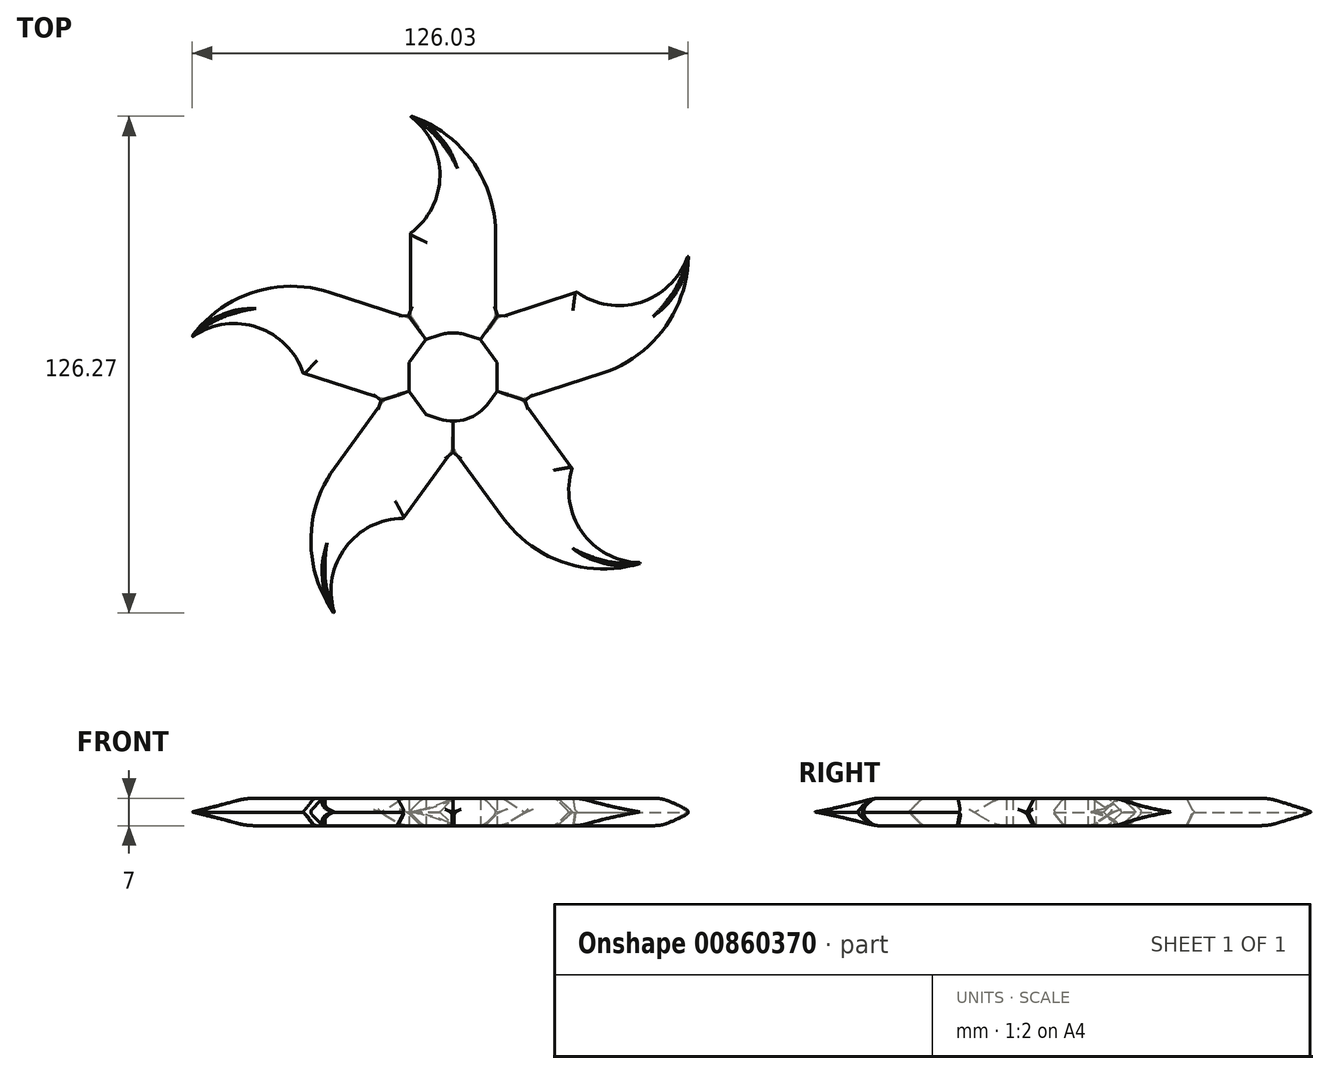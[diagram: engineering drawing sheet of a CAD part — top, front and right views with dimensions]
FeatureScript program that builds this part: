
annotation { "Feature Type Name" : "Feature", "Feature Type Description" : "" }
export const myFeature = defineFeature(function(context is Context, id is Id, definition is map)
    precondition{}
    {
        {
            var Q0;
            Q0=qCreatedBy(makeId("Top.planeOp"),FACE);
            var sketch = newSketch(context, id + "F0", { "sketchPlane" : qUnion([Q0])});
            skCircle(sketch, "E0", {"center": v(0, 0) * mm, "radius": 11.2 * mm});
            skLineSegment(sketch, "E1", {"start": v(-11.2, 36.37) * mm, "end": v(-11.2, 15.42) * mm});
            skLineSegment(sketch, "E2", {"start": v(11.2, 36.37) * mm, "end": v(11.2, 15.42) * mm});
            skLineSegment(sketch, "E3.1.0", {"start": v(-38.05, 0.59) * mm, "end": v(-18.12, -5.89) * mm});
            skLineSegment(sketch, "E3.2.0", {"start": v(-12.32, -36) * mm, "end": v(0, -19.05) * mm});
            skLineSegment(sketch, "E3.3.0", {"start": v(30.44, -22.84) * mm, "end": v(18.12, -5.89) * mm});
            skLineSegment(sketch, "E3.4.0", {"start": v(31.13, 21.9) * mm, "end": v(11.2, 15.42) * mm});
            skLineSegment(sketch, "E4.1.0", {"start": v(-31.13, 21.9) * mm, "end": v(-11.2, 15.42) * mm});
            skLineSegment(sketch, "E4.2.0", {"start": v(-30.44, -22.84) * mm, "end": v(-18.12, -5.89) * mm});
            skLineSegment(sketch, "E4.3.0", {"start": v(12.32, -36) * mm, "end": v(0, -19.05) * mm});
            skLineSegment(sketch, "E4.4.0", {"start": v(38.05, 0.59) * mm, "end": v(18.12, -5.89) * mm});
            skArc(sketch, "E5", {"start": v(11.2, 36.37) * mm, "mid": v(4.51, 55.95) * mm, "end": v(-12.75, 67.34) * mm});
            skArc(sketch, "E6", {"start": v(-11.2, 36.37) * mm, "mid": v(-3.43, 52.28) * mm, "end": v(-12.75, 67.34) * mm});
            skArc(sketch, "E7.1.0", {"start": v(-38.05, 0.59) * mm, "mid": v(-50.78, 12.9) * mm, "end": v(-67.98, 8.68) * mm});
            skArc(sketch, "E7.1.1", {"start": v(-31.13, 21.9) * mm, "mid": v(-51.81, 21.58) * mm, "end": v(-67.98, 8.68) * mm});
            skArc(sketch, "E7.2.0", {"start": v(-12.32, -36) * mm, "mid": v(-27.95, -44.32) * mm, "end": v(-29.26, -61.97) * mm});
            skArc(sketch, "E7.2.1", {"start": v(-30.44, -22.84) * mm, "mid": v(-36.53, -42.6) * mm, "end": v(-29.26, -61.97) * mm});
            skArc(sketch, "E7.3.0", {"start": v(30.44, -22.84) * mm, "mid": v(33.5, -40.28) * mm, "end": v(49.9, -46.98) * mm});
            skArc(sketch, "E7.3.1", {"start": v(12.32, -36) * mm, "mid": v(29.23, -47.91) * mm, "end": v(49.9, -46.98) * mm});
            skArc(sketch, "E7.4.0", {"start": v(31.13, 21.9) * mm, "mid": v(48.66, 19.42) * mm, "end": v(60.1, 32.94) * mm});
            skArc(sketch, "E7.4.1", {"start": v(38.05, 0.59) * mm, "mid": v(54.6, 13) * mm, "end": v(60.1, 32.94) * mm});
            skLineSegment(sketch, "E8.trimOffspring", {"start": v(11.2, 3.64) * mm, "end": v(11.2, -3.64) * mm});
            skLineSegment(sketch, "E9.trimOffspring", {"start": v(-6.92, -9.53) * mm, "end": v(-3.46, -10.65) * mm});
            skLineSegment(sketch, "E10.trimOffspring", {"start": v(0, 11.78) * mm, "end": v(-6.92, 9.53) * mm});
            skLineSegment(sketch, "E11.trimOffspring", {"start": v(3.46, 10.65) * mm, "end": v(6.92, 9.53) * mm});
            skLineSegment(sketch, "E12.trimOffspring", {"start": v(-11.2, 3.64) * mm, "end": v(-11.2, -3.64) * mm});
            skLineSegment(sketch, "E13.trimOffspring", {"start": v(-11.2, 3.64) * mm, "end": v(-6.92, 9.53) * mm});
            skLineSegment(sketch, "E14.trimOffspring", {"start": v(-6.92, -9.53) * mm, "end": v(-11.2, -3.64) * mm});
            skLineSegment(sketch, "E15.trimOffspring", {"start": v(11.2, 3.64) * mm, "end": v(6.92, 9.53) * mm});
            skLineSegment(sketch, "E16.trimOffspring", {"start": v(9.06, -6.58) * mm, "end": v(11.2, -3.64) * mm});
            skSolve(sketch);
        }
        {
            var Q0;
            Q0=makeQuery(id+"F0.imprint","IMPRINT",FACE,{"disambiguationData":[TD([[makeQuery(id+"F0.imprint","IMPRINT",EDGE,{"derivedFrom":sQuery(id+"F0.wireOp",EDGE,"E1")}),1.0]])]});
            extrude(context, id + "F1", {"entities" : qUnion([Q0]), "depth" : 7 * mm, "offsetDistance" : 25 * mm});
        }
        {
            var Q0;
            Q0=makeQuery(id+"F1.opExtrude","CAP_EDGE",EDGE,{"disambiguationData":[OSD([sQuery(id+"F0.wireOp",EDGE,"E5")])],"isStart":false});
            var Q1;
            Q1=makeQuery(id+"F1.opExtrude","CAP_EDGE",EDGE,{"disambiguationData":[OSD([sQuery(id+"F0.wireOp",EDGE,"E2")])],"isStart":false});
            var Q2;
            Q2=makeQuery(id+"F1.opExtrude","CAP_EDGE",EDGE,{"disambiguationData":[OSD([sQuery(id+"F0.wireOp",EDGE,"E6")])],"isStart":false});
            var Q3;
            Q3=makeQuery(id+"F1.opExtrude","CAP_EDGE",EDGE,{"disambiguationData":[OSD([sQuery(id+"F0.wireOp",EDGE,"E1")])],"isStart":false});
            var Q4;
            Q4=makeQuery(id+"F1.opExtrude","CAP_EDGE",EDGE,{"disambiguationData":[OSD([sQuery(id+"F0.wireOp",EDGE,"E3.4.0")])],"isStart":false});
            var Q5;
            Q5=makeQuery(id+"F1.opExtrude","CAP_EDGE",EDGE,{"disambiguationData":[OSD([sQuery(id+"F0.wireOp",EDGE,"E7.4.0")])],"isStart":false});
            var Q6;
            Q6=makeQuery(id+"F1.opExtrude","CAP_EDGE",EDGE,{"disambiguationData":[OSD([sQuery(id+"F0.wireOp",EDGE,"E7.4.1")])],"isStart":false});
            var Q7;
            Q7=makeQuery(id+"F1.opExtrude","CAP_EDGE",EDGE,{"disambiguationData":[OSD([sQuery(id+"F0.wireOp",EDGE,"E4.4.0")])],"isStart":false});
            var Q8;
            Q8=makeQuery(id+"F1.opExtrude","CAP_EDGE",EDGE,{"disambiguationData":[OSD([sQuery(id+"F0.wireOp",EDGE,"E3.3.0")])],"isStart":false});
            var Q9;
            Q9=makeQuery(id+"F1.opExtrude","CAP_EDGE",EDGE,{"disambiguationData":[OSD([sQuery(id+"F0.wireOp",EDGE,"E7.3.0")])],"isStart":false});
            var Q10;
            Q10=makeQuery(id+"F1.opExtrude","CAP_EDGE",EDGE,{"disambiguationData":[OSD([sQuery(id+"F0.wireOp",EDGE,"E7.3.1")])],"isStart":false});
            var Q11;
            Q11=makeQuery(id+"F1.opExtrude","CAP_EDGE",EDGE,{"disambiguationData":[OSD([sQuery(id+"F0.wireOp",EDGE,"E4.3.0")])],"isStart":false});
            var Q12;
            Q12=makeQuery(id+"F1.opExtrude","CAP_EDGE",EDGE,{"disambiguationData":[OSD([sQuery(id+"F0.wireOp",EDGE,"E4.1.0")])],"isStart":false});
            var Q13;
            Q13=makeQuery(id+"F1.opExtrude","CAP_EDGE",EDGE,{"disambiguationData":[OSD([sQuery(id+"F0.wireOp",EDGE,"E7.1.1")])],"isStart":false});
            var Q14;
            Q14=makeQuery(id+"F1.opExtrude","CAP_EDGE",EDGE,{"disambiguationData":[OSD([sQuery(id+"F0.wireOp",EDGE,"E7.1.0")])],"isStart":false});
            var Q15;
            Q15=makeQuery(id+"F1.opExtrude","CAP_EDGE",EDGE,{"disambiguationData":[OSD([sQuery(id+"F0.wireOp",EDGE,"E3.1.0")])],"isStart":false});
            var Q16;
            Q16=makeQuery(id+"F1.opExtrude","CAP_EDGE",EDGE,{"disambiguationData":[OSD([sQuery(id+"F0.wireOp",EDGE,"E4.2.0")])],"isStart":false});
            var Q17;
            Q17=makeQuery(id+"F1.opExtrude","CAP_EDGE",EDGE,{"disambiguationData":[OSD([sQuery(id+"F0.wireOp",EDGE,"E7.2.1")])],"isStart":false});
            var Q18;
            Q18=makeQuery(id+"F1.opExtrude","CAP_EDGE",EDGE,{"disambiguationData":[OSD([sQuery(id+"F0.wireOp",EDGE,"E3.2.0")])],"isStart":false});
            var Q19;
            Q19=makeQuery(id+"F1.opExtrude","CAP_EDGE",EDGE,{"disambiguationData":[OSD([sQuery(id+"F0.wireOp",EDGE,"E7.2.0")])],"isStart":false});
            chamfer(context, id + "F2", {"entities" : qUnion([Q0, Q1, Q2, Q3, Q4, Q5, Q6, Q7, Q8, Q9, Q10, Q11, Q12, Q13, Q14, Q15, Q16, Q17, Q18, Q19]), "width" : 3.5 * mm, "tangentPropagation" : true});
        }
        {
            var Q0;
            Q0=makeQuery(id+"F1.opExtrude","CAP_EDGE",EDGE,{"disambiguationData":[OSD([sQuery(id+"F0.wireOp",EDGE,"E7.2.0")])],"isStart":true});
            var Q1;
            Q1=makeQuery(id+"F1.opExtrude","CAP_EDGE",EDGE,{"disambiguationData":[OSD([sQuery(id+"F0.wireOp",EDGE,"E7.2.1")])],"isStart":true});
            var Q2;
            Q2=makeQuery(id+"F1.opExtrude","CAP_EDGE",EDGE,{"disambiguationData":[OSD([sQuery(id+"F0.wireOp",EDGE,"E4.2.0")])],"isStart":true});
            var Q3;
            Q3=makeQuery(id+"F1.opExtrude","CAP_EDGE",EDGE,{"disambiguationData":[OSD([sQuery(id+"F0.wireOp",EDGE,"E3.2.0")])],"isStart":true});
            var Q4;
            Q4=makeQuery(id+"F1.opExtrude","CAP_EDGE",EDGE,{"disambiguationData":[OSD([sQuery(id+"F0.wireOp",EDGE,"E7.3.1")])],"isStart":true});
            var Q5;
            Q5=makeQuery(id+"F1.opExtrude","CAP_EDGE",EDGE,{"disambiguationData":[OSD([sQuery(id+"F0.wireOp",EDGE,"E4.3.0")])],"isStart":true});
            var Q6;
            Q6=makeQuery(id+"F1.opExtrude","CAP_EDGE",EDGE,{"disambiguationData":[OSD([sQuery(id+"F0.wireOp",EDGE,"E7.3.0")])],"isStart":true});
            var Q7;
            Q7=makeQuery(id+"F1.opExtrude","CAP_EDGE",EDGE,{"disambiguationData":[OSD([sQuery(id+"F0.wireOp",EDGE,"E3.3.0")])],"isStart":true});
            var Q8;
            Q8=makeQuery(id+"F1.opExtrude","CAP_EDGE",EDGE,{"disambiguationData":[OSD([sQuery(id+"F0.wireOp",EDGE,"E3.1.0")])],"isStart":true});
            var Q9;
            Q9=makeQuery(id+"F1.opExtrude","CAP_EDGE",EDGE,{"disambiguationData":[OSD([sQuery(id+"F0.wireOp",EDGE,"E7.1.0")])],"isStart":true});
            var Q10;
            Q10=makeQuery(id+"F1.opExtrude","CAP_EDGE",EDGE,{"disambiguationData":[OSD([sQuery(id+"F0.wireOp",EDGE,"E7.1.1")])],"isStart":true});
            var Q11;
            Q11=makeQuery(id+"F1.opExtrude","CAP_EDGE",EDGE,{"disambiguationData":[OSD([sQuery(id+"F0.wireOp",EDGE,"E4.1.0")])],"isStart":true});
            var Q12;
            Q12=makeQuery(id+"F1.opExtrude","CAP_EDGE",EDGE,{"disambiguationData":[OSD([sQuery(id+"F0.wireOp",EDGE,"E1")])],"isStart":true});
            var Q13;
            Q13=makeQuery(id+"F1.opExtrude","CAP_EDGE",EDGE,{"disambiguationData":[OSD([sQuery(id+"F0.wireOp",EDGE,"E6")])],"isStart":true});
            var Q14;
            Q14=makeQuery(id+"F1.opExtrude","CAP_EDGE",EDGE,{"disambiguationData":[OSD([sQuery(id+"F0.wireOp",EDGE,"E5")])],"isStart":true});
            var Q15;
            Q15=makeQuery(id+"F1.opExtrude","CAP_EDGE",EDGE,{"disambiguationData":[OSD([sQuery(id+"F0.wireOp",EDGE,"E2")])],"isStart":true});
            var Q16;
            Q16=makeQuery(id+"F1.opExtrude","CAP_EDGE",EDGE,{"disambiguationData":[OSD([sQuery(id+"F0.wireOp",EDGE,"E3.4.0")])],"isStart":true});
            var Q17;
            Q17=makeQuery(id+"F1.opExtrude","CAP_EDGE",EDGE,{"disambiguationData":[OSD([sQuery(id+"F0.wireOp",EDGE,"E7.4.0")])],"isStart":true});
            var Q18;
            Q18=makeQuery(id+"F1.opExtrude","CAP_EDGE",EDGE,{"disambiguationData":[OSD([sQuery(id+"F0.wireOp",EDGE,"E7.4.1")])],"isStart":true});
            var Q19;
            Q19=makeQuery(id+"F1.opExtrude","CAP_EDGE",EDGE,{"disambiguationData":[OSD([sQuery(id+"F0.wireOp",EDGE,"E4.4.0")])],"isStart":true});
            chamfer(context, id + "F3", {"entities" : qUnion([Q0, Q1, Q2, Q3, Q4, Q5, Q6, Q7, Q8, Q9, Q10, Q11, Q12, Q13, Q14, Q15, Q16, Q17, Q18, Q19]), "width" : 3.5 * mm, "tangentPropagation" : true});
        }
        {
            var Q0;
            {var subQ0=sQuery(id+"F0.wireOp",EDGE,"E7.2.0");Q0=makeQuery(id+"F3.opChamfer","BLEND_EDGE",EDGE,{"blendedFrom":[makeQuery(id+"F1.opExtrude","CAP_EDGE",EDGE,{"disambiguationData":[OSD([subQ0])],"isStart":true}),makeQuery(id+"F1.opExtrude","CAP_FACE",FACE,{"disambiguationData":[OSD([sQuery(id+"F0.wireOp",EDGE,"E0"),sQuery(id+"F0.wireOp",EDGE,"E1"),sQuery(id+"F0.wireOp",EDGE,"E2"),sQuery(id+"F0.wireOp",EDGE,"E3.1.0"),sQuery(id+"F0.wireOp",EDGE,"E3.2.0"),sQuery(id+"F0.wireOp",EDGE,"E3.3.0"),sQuery(id+"F0.wireOp",EDGE,"E3.4.0"),sQuery(id+"F0.wireOp",EDGE,"E4.1.0"),sQuery(id+"F0.wireOp",EDGE,"E4.2.0"),sQuery(id+"F0.wireOp",EDGE,"E4.3.0"),sQuery(id+"F0.wireOp",EDGE,"E4.4.0"),sQuery(id+"F0.wireOp",EDGE,"E5"),sQuery(id+"F0.wireOp",EDGE,"E6"),sQuery(id+"F0.wireOp",EDGE,"E7.1.0"),sQuery(id+"F0.wireOp",EDGE,"E7.1.1"),subQ0,sQuery(id+"F0.wireOp",EDGE,"E7.2.1"),sQuery(id+"F0.wireOp",EDGE,"E7.3.0"),sQuery(id+"F0.wireOp",EDGE,"E7.3.1"),sQuery(id+"F0.wireOp",EDGE,"E7.4.0"),sQuery(id+"F0.wireOp",EDGE,"E7.4.1"),sQuery(id+"F0.wireOp",EDGE,"E8.trimOffspring"),sQuery(id+"F0.wireOp",EDGE,"E9.trimOffspring"),sQuery(id+"F0.wireOp",EDGE,"E10.trimOffspring"),sQuery(id+"F0.wireOp",EDGE,"E11.trimOffspring"),sQuery(id+"F0.wireOp",EDGE,"E12.trimOffspring"),sQuery(id+"F0.wireOp",EDGE,"E13.trimOffspring"),sQuery(id+"F0.wireOp",EDGE,"E14.trimOffspring"),sQuery(id+"F0.wireOp",EDGE,"E15.trimOffspring"),sQuery(id+"F0.wireOp",EDGE,"E16.trimOffspring")])],"isStart":true})],"blendedInto":[makeQuery(id+"F1.opExtrude","CAP_FACE",FACE,{"disambiguationData":[OSD([sQuery(id+"F0.wireOp",EDGE,"E0"),sQuery(id+"F0.wireOp",EDGE,"E1"),sQuery(id+"F0.wireOp",EDGE,"E2"),sQuery(id+"F0.wireOp",EDGE,"E3.1.0"),sQuery(id+"F0.wireOp",EDGE,"E3.2.0"),sQuery(id+"F0.wireOp",EDGE,"E3.3.0"),sQuery(id+"F0.wireOp",EDGE,"E3.4.0"),sQuery(id+"F0.wireOp",EDGE,"E4.1.0"),sQuery(id+"F0.wireOp",EDGE,"E4.2.0"),sQuery(id+"F0.wireOp",EDGE,"E4.3.0"),sQuery(id+"F0.wireOp",EDGE,"E4.4.0"),sQuery(id+"F0.wireOp",EDGE,"E5"),sQuery(id+"F0.wireOp",EDGE,"E6"),sQuery(id+"F0.wireOp",EDGE,"E7.1.0"),sQuery(id+"F0.wireOp",EDGE,"E7.1.1"),subQ0,sQuery(id+"F0.wireOp",EDGE,"E7.2.1"),sQuery(id+"F0.wireOp",EDGE,"E7.3.0"),sQuery(id+"F0.wireOp",EDGE,"E7.3.1"),sQuery(id+"F0.wireOp",EDGE,"E7.4.0"),sQuery(id+"F0.wireOp",EDGE,"E7.4.1"),sQuery(id+"F0.wireOp",EDGE,"E8.trimOffspring"),sQuery(id+"F0.wireOp",EDGE,"E9.trimOffspring"),sQuery(id+"F0.wireOp",EDGE,"E10.trimOffspring"),sQuery(id+"F0.wireOp",EDGE,"E11.trimOffspring"),sQuery(id+"F0.wireOp",EDGE,"E12.trimOffspring"),sQuery(id+"F0.wireOp",EDGE,"E13.trimOffspring"),sQuery(id+"F0.wireOp",EDGE,"E14.trimOffspring"),sQuery(id+"F0.wireOp",EDGE,"E15.trimOffspring"),sQuery(id+"F0.wireOp",EDGE,"E16.trimOffspring")])],"isStart":true})]});}
            var Q1;
            {var subQ0=sQuery(id+"F0.wireOp",EDGE,"E7.2.1");Q1=makeQuery(id+"F3.opChamfer","BLEND_EDGE",EDGE,{"blendedFrom":[makeQuery(id+"F1.opExtrude","CAP_EDGE",EDGE,{"disambiguationData":[OSD([subQ0])],"isStart":true}),makeQuery(id+"F1.opExtrude","CAP_FACE",FACE,{"disambiguationData":[OSD([sQuery(id+"F0.wireOp",EDGE,"E0"),sQuery(id+"F0.wireOp",EDGE,"E1"),sQuery(id+"F0.wireOp",EDGE,"E2"),sQuery(id+"F0.wireOp",EDGE,"E3.1.0"),sQuery(id+"F0.wireOp",EDGE,"E3.2.0"),sQuery(id+"F0.wireOp",EDGE,"E3.3.0"),sQuery(id+"F0.wireOp",EDGE,"E3.4.0"),sQuery(id+"F0.wireOp",EDGE,"E4.1.0"),sQuery(id+"F0.wireOp",EDGE,"E4.2.0"),sQuery(id+"F0.wireOp",EDGE,"E4.3.0"),sQuery(id+"F0.wireOp",EDGE,"E4.4.0"),sQuery(id+"F0.wireOp",EDGE,"E5"),sQuery(id+"F0.wireOp",EDGE,"E6"),sQuery(id+"F0.wireOp",EDGE,"E7.1.0"),sQuery(id+"F0.wireOp",EDGE,"E7.1.1"),sQuery(id+"F0.wireOp",EDGE,"E7.2.0"),subQ0,sQuery(id+"F0.wireOp",EDGE,"E7.3.0"),sQuery(id+"F0.wireOp",EDGE,"E7.3.1"),sQuery(id+"F0.wireOp",EDGE,"E7.4.0"),sQuery(id+"F0.wireOp",EDGE,"E7.4.1"),sQuery(id+"F0.wireOp",EDGE,"E8.trimOffspring"),sQuery(id+"F0.wireOp",EDGE,"E9.trimOffspring"),sQuery(id+"F0.wireOp",EDGE,"E10.trimOffspring"),sQuery(id+"F0.wireOp",EDGE,"E11.trimOffspring"),sQuery(id+"F0.wireOp",EDGE,"E12.trimOffspring"),sQuery(id+"F0.wireOp",EDGE,"E13.trimOffspring"),sQuery(id+"F0.wireOp",EDGE,"E14.trimOffspring"),sQuery(id+"F0.wireOp",EDGE,"E15.trimOffspring"),sQuery(id+"F0.wireOp",EDGE,"E16.trimOffspring")])],"isStart":true})],"blendedInto":[makeQuery(id+"F1.opExtrude","CAP_FACE",FACE,{"disambiguationData":[OSD([sQuery(id+"F0.wireOp",EDGE,"E0"),sQuery(id+"F0.wireOp",EDGE,"E1"),sQuery(id+"F0.wireOp",EDGE,"E2"),sQuery(id+"F0.wireOp",EDGE,"E3.1.0"),sQuery(id+"F0.wireOp",EDGE,"E3.2.0"),sQuery(id+"F0.wireOp",EDGE,"E3.3.0"),sQuery(id+"F0.wireOp",EDGE,"E3.4.0"),sQuery(id+"F0.wireOp",EDGE,"E4.1.0"),sQuery(id+"F0.wireOp",EDGE,"E4.2.0"),sQuery(id+"F0.wireOp",EDGE,"E4.3.0"),sQuery(id+"F0.wireOp",EDGE,"E4.4.0"),sQuery(id+"F0.wireOp",EDGE,"E5"),sQuery(id+"F0.wireOp",EDGE,"E6"),sQuery(id+"F0.wireOp",EDGE,"E7.1.0"),sQuery(id+"F0.wireOp",EDGE,"E7.1.1"),sQuery(id+"F0.wireOp",EDGE,"E7.2.0"),subQ0,sQuery(id+"F0.wireOp",EDGE,"E7.3.0"),sQuery(id+"F0.wireOp",EDGE,"E7.3.1"),sQuery(id+"F0.wireOp",EDGE,"E7.4.0"),sQuery(id+"F0.wireOp",EDGE,"E7.4.1"),sQuery(id+"F0.wireOp",EDGE,"E8.trimOffspring"),sQuery(id+"F0.wireOp",EDGE,"E9.trimOffspring"),sQuery(id+"F0.wireOp",EDGE,"E10.trimOffspring"),sQuery(id+"F0.wireOp",EDGE,"E11.trimOffspring"),sQuery(id+"F0.wireOp",EDGE,"E12.trimOffspring"),sQuery(id+"F0.wireOp",EDGE,"E13.trimOffspring"),sQuery(id+"F0.wireOp",EDGE,"E14.trimOffspring"),sQuery(id+"F0.wireOp",EDGE,"E15.trimOffspring"),sQuery(id+"F0.wireOp",EDGE,"E16.trimOffspring")])],"isStart":true})]});}
            var Q2;
            {var subQ0=sQuery(id+"F0.wireOp",EDGE,"E4.2.0");Q2=makeQuery(id+"F3.opChamfer","BLEND_EDGE",EDGE,{"blendedFrom":[makeQuery(id+"F1.opExtrude","CAP_EDGE",EDGE,{"disambiguationData":[OSD([subQ0])],"isStart":true}),makeQuery(id+"F1.opExtrude","CAP_FACE",FACE,{"disambiguationData":[OSD([sQuery(id+"F0.wireOp",EDGE,"E0"),sQuery(id+"F0.wireOp",EDGE,"E1"),sQuery(id+"F0.wireOp",EDGE,"E2"),sQuery(id+"F0.wireOp",EDGE,"E3.1.0"),sQuery(id+"F0.wireOp",EDGE,"E3.2.0"),sQuery(id+"F0.wireOp",EDGE,"E3.3.0"),sQuery(id+"F0.wireOp",EDGE,"E3.4.0"),sQuery(id+"F0.wireOp",EDGE,"E4.1.0"),subQ0,sQuery(id+"F0.wireOp",EDGE,"E4.3.0"),sQuery(id+"F0.wireOp",EDGE,"E4.4.0"),sQuery(id+"F0.wireOp",EDGE,"E5"),sQuery(id+"F0.wireOp",EDGE,"E6"),sQuery(id+"F0.wireOp",EDGE,"E7.1.0"),sQuery(id+"F0.wireOp",EDGE,"E7.1.1"),sQuery(id+"F0.wireOp",EDGE,"E7.2.0"),sQuery(id+"F0.wireOp",EDGE,"E7.2.1"),sQuery(id+"F0.wireOp",EDGE,"E7.3.0"),sQuery(id+"F0.wireOp",EDGE,"E7.3.1"),sQuery(id+"F0.wireOp",EDGE,"E7.4.0"),sQuery(id+"F0.wireOp",EDGE,"E7.4.1"),sQuery(id+"F0.wireOp",EDGE,"E8.trimOffspring"),sQuery(id+"F0.wireOp",EDGE,"E9.trimOffspring"),sQuery(id+"F0.wireOp",EDGE,"E10.trimOffspring"),sQuery(id+"F0.wireOp",EDGE,"E11.trimOffspring"),sQuery(id+"F0.wireOp",EDGE,"E12.trimOffspring"),sQuery(id+"F0.wireOp",EDGE,"E13.trimOffspring"),sQuery(id+"F0.wireOp",EDGE,"E14.trimOffspring"),sQuery(id+"F0.wireOp",EDGE,"E15.trimOffspring"),sQuery(id+"F0.wireOp",EDGE,"E16.trimOffspring")])],"isStart":true})],"blendedInto":[makeQuery(id+"F1.opExtrude","CAP_FACE",FACE,{"disambiguationData":[OSD([sQuery(id+"F0.wireOp",EDGE,"E0"),sQuery(id+"F0.wireOp",EDGE,"E1"),sQuery(id+"F0.wireOp",EDGE,"E2"),sQuery(id+"F0.wireOp",EDGE,"E3.1.0"),sQuery(id+"F0.wireOp",EDGE,"E3.2.0"),sQuery(id+"F0.wireOp",EDGE,"E3.3.0"),sQuery(id+"F0.wireOp",EDGE,"E3.4.0"),sQuery(id+"F0.wireOp",EDGE,"E4.1.0"),subQ0,sQuery(id+"F0.wireOp",EDGE,"E4.3.0"),sQuery(id+"F0.wireOp",EDGE,"E4.4.0"),sQuery(id+"F0.wireOp",EDGE,"E5"),sQuery(id+"F0.wireOp",EDGE,"E6"),sQuery(id+"F0.wireOp",EDGE,"E7.1.0"),sQuery(id+"F0.wireOp",EDGE,"E7.1.1"),sQuery(id+"F0.wireOp",EDGE,"E7.2.0"),sQuery(id+"F0.wireOp",EDGE,"E7.2.1"),sQuery(id+"F0.wireOp",EDGE,"E7.3.0"),sQuery(id+"F0.wireOp",EDGE,"E7.3.1"),sQuery(id+"F0.wireOp",EDGE,"E7.4.0"),sQuery(id+"F0.wireOp",EDGE,"E7.4.1"),sQuery(id+"F0.wireOp",EDGE,"E8.trimOffspring"),sQuery(id+"F0.wireOp",EDGE,"E9.trimOffspring"),sQuery(id+"F0.wireOp",EDGE,"E10.trimOffspring"),sQuery(id+"F0.wireOp",EDGE,"E11.trimOffspring"),sQuery(id+"F0.wireOp",EDGE,"E12.trimOffspring"),sQuery(id+"F0.wireOp",EDGE,"E13.trimOffspring"),sQuery(id+"F0.wireOp",EDGE,"E14.trimOffspring"),sQuery(id+"F0.wireOp",EDGE,"E15.trimOffspring"),sQuery(id+"F0.wireOp",EDGE,"E16.trimOffspring")])],"isStart":true})]});}
            var Q3;
            {var subQ0=sQuery(id+"F0.wireOp",EDGE,"E3.2.0");Q3=makeQuery(id+"F3.opChamfer","BLEND_EDGE",EDGE,{"blendedFrom":[makeQuery(id+"F1.opExtrude","CAP_EDGE",EDGE,{"disambiguationData":[OSD([subQ0])],"isStart":true}),makeQuery(id+"F1.opExtrude","CAP_FACE",FACE,{"disambiguationData":[OSD([sQuery(id+"F0.wireOp",EDGE,"E0"),sQuery(id+"F0.wireOp",EDGE,"E1"),sQuery(id+"F0.wireOp",EDGE,"E2"),sQuery(id+"F0.wireOp",EDGE,"E3.1.0"),subQ0,sQuery(id+"F0.wireOp",EDGE,"E3.3.0"),sQuery(id+"F0.wireOp",EDGE,"E3.4.0"),sQuery(id+"F0.wireOp",EDGE,"E4.1.0"),sQuery(id+"F0.wireOp",EDGE,"E4.2.0"),sQuery(id+"F0.wireOp",EDGE,"E4.3.0"),sQuery(id+"F0.wireOp",EDGE,"E4.4.0"),sQuery(id+"F0.wireOp",EDGE,"E5"),sQuery(id+"F0.wireOp",EDGE,"E6"),sQuery(id+"F0.wireOp",EDGE,"E7.1.0"),sQuery(id+"F0.wireOp",EDGE,"E7.1.1"),sQuery(id+"F0.wireOp",EDGE,"E7.2.0"),sQuery(id+"F0.wireOp",EDGE,"E7.2.1"),sQuery(id+"F0.wireOp",EDGE,"E7.3.0"),sQuery(id+"F0.wireOp",EDGE,"E7.3.1"),sQuery(id+"F0.wireOp",EDGE,"E7.4.0"),sQuery(id+"F0.wireOp",EDGE,"E7.4.1"),sQuery(id+"F0.wireOp",EDGE,"E8.trimOffspring"),sQuery(id+"F0.wireOp",EDGE,"E9.trimOffspring"),sQuery(id+"F0.wireOp",EDGE,"E10.trimOffspring"),sQuery(id+"F0.wireOp",EDGE,"E11.trimOffspring"),sQuery(id+"F0.wireOp",EDGE,"E12.trimOffspring"),sQuery(id+"F0.wireOp",EDGE,"E13.trimOffspring"),sQuery(id+"F0.wireOp",EDGE,"E14.trimOffspring"),sQuery(id+"F0.wireOp",EDGE,"E15.trimOffspring"),sQuery(id+"F0.wireOp",EDGE,"E16.trimOffspring")])],"isStart":true})],"blendedInto":[makeQuery(id+"F1.opExtrude","CAP_FACE",FACE,{"disambiguationData":[OSD([sQuery(id+"F0.wireOp",EDGE,"E0"),sQuery(id+"F0.wireOp",EDGE,"E1"),sQuery(id+"F0.wireOp",EDGE,"E2"),sQuery(id+"F0.wireOp",EDGE,"E3.1.0"),subQ0,sQuery(id+"F0.wireOp",EDGE,"E3.3.0"),sQuery(id+"F0.wireOp",EDGE,"E3.4.0"),sQuery(id+"F0.wireOp",EDGE,"E4.1.0"),sQuery(id+"F0.wireOp",EDGE,"E4.2.0"),sQuery(id+"F0.wireOp",EDGE,"E4.3.0"),sQuery(id+"F0.wireOp",EDGE,"E4.4.0"),sQuery(id+"F0.wireOp",EDGE,"E5"),sQuery(id+"F0.wireOp",EDGE,"E6"),sQuery(id+"F0.wireOp",EDGE,"E7.1.0"),sQuery(id+"F0.wireOp",EDGE,"E7.1.1"),sQuery(id+"F0.wireOp",EDGE,"E7.2.0"),sQuery(id+"F0.wireOp",EDGE,"E7.2.1"),sQuery(id+"F0.wireOp",EDGE,"E7.3.0"),sQuery(id+"F0.wireOp",EDGE,"E7.3.1"),sQuery(id+"F0.wireOp",EDGE,"E7.4.0"),sQuery(id+"F0.wireOp",EDGE,"E7.4.1"),sQuery(id+"F0.wireOp",EDGE,"E8.trimOffspring"),sQuery(id+"F0.wireOp",EDGE,"E9.trimOffspring"),sQuery(id+"F0.wireOp",EDGE,"E10.trimOffspring"),sQuery(id+"F0.wireOp",EDGE,"E11.trimOffspring"),sQuery(id+"F0.wireOp",EDGE,"E12.trimOffspring"),sQuery(id+"F0.wireOp",EDGE,"E13.trimOffspring"),sQuery(id+"F0.wireOp",EDGE,"E14.trimOffspring"),sQuery(id+"F0.wireOp",EDGE,"E15.trimOffspring"),sQuery(id+"F0.wireOp",EDGE,"E16.trimOffspring")])],"isStart":true})]});}
            var Q4;
            {var subQ0=sQuery(id+"F0.wireOp",EDGE,"E4.3.0");Q4=makeQuery(id+"F3.opChamfer","BLEND_EDGE",EDGE,{"blendedFrom":[makeQuery(id+"F1.opExtrude","CAP_EDGE",EDGE,{"disambiguationData":[OSD([subQ0])],"isStart":true}),makeQuery(id+"F1.opExtrude","CAP_FACE",FACE,{"disambiguationData":[OSD([sQuery(id+"F0.wireOp",EDGE,"E0"),sQuery(id+"F0.wireOp",EDGE,"E1"),sQuery(id+"F0.wireOp",EDGE,"E2"),sQuery(id+"F0.wireOp",EDGE,"E3.1.0"),sQuery(id+"F0.wireOp",EDGE,"E3.2.0"),sQuery(id+"F0.wireOp",EDGE,"E3.3.0"),sQuery(id+"F0.wireOp",EDGE,"E3.4.0"),sQuery(id+"F0.wireOp",EDGE,"E4.1.0"),sQuery(id+"F0.wireOp",EDGE,"E4.2.0"),subQ0,sQuery(id+"F0.wireOp",EDGE,"E4.4.0"),sQuery(id+"F0.wireOp",EDGE,"E5"),sQuery(id+"F0.wireOp",EDGE,"E6"),sQuery(id+"F0.wireOp",EDGE,"E7.1.0"),sQuery(id+"F0.wireOp",EDGE,"E7.1.1"),sQuery(id+"F0.wireOp",EDGE,"E7.2.0"),sQuery(id+"F0.wireOp",EDGE,"E7.2.1"),sQuery(id+"F0.wireOp",EDGE,"E7.3.0"),sQuery(id+"F0.wireOp",EDGE,"E7.3.1"),sQuery(id+"F0.wireOp",EDGE,"E7.4.0"),sQuery(id+"F0.wireOp",EDGE,"E7.4.1"),sQuery(id+"F0.wireOp",EDGE,"E8.trimOffspring"),sQuery(id+"F0.wireOp",EDGE,"E9.trimOffspring"),sQuery(id+"F0.wireOp",EDGE,"E10.trimOffspring"),sQuery(id+"F0.wireOp",EDGE,"E11.trimOffspring"),sQuery(id+"F0.wireOp",EDGE,"E12.trimOffspring"),sQuery(id+"F0.wireOp",EDGE,"E13.trimOffspring"),sQuery(id+"F0.wireOp",EDGE,"E14.trimOffspring"),sQuery(id+"F0.wireOp",EDGE,"E15.trimOffspring"),sQuery(id+"F0.wireOp",EDGE,"E16.trimOffspring")])],"isStart":true})],"blendedInto":[makeQuery(id+"F1.opExtrude","CAP_FACE",FACE,{"disambiguationData":[OSD([sQuery(id+"F0.wireOp",EDGE,"E0"),sQuery(id+"F0.wireOp",EDGE,"E1"),sQuery(id+"F0.wireOp",EDGE,"E2"),sQuery(id+"F0.wireOp",EDGE,"E3.1.0"),sQuery(id+"F0.wireOp",EDGE,"E3.2.0"),sQuery(id+"F0.wireOp",EDGE,"E3.3.0"),sQuery(id+"F0.wireOp",EDGE,"E3.4.0"),sQuery(id+"F0.wireOp",EDGE,"E4.1.0"),sQuery(id+"F0.wireOp",EDGE,"E4.2.0"),subQ0,sQuery(id+"F0.wireOp",EDGE,"E4.4.0"),sQuery(id+"F0.wireOp",EDGE,"E5"),sQuery(id+"F0.wireOp",EDGE,"E6"),sQuery(id+"F0.wireOp",EDGE,"E7.1.0"),sQuery(id+"F0.wireOp",EDGE,"E7.1.1"),sQuery(id+"F0.wireOp",EDGE,"E7.2.0"),sQuery(id+"F0.wireOp",EDGE,"E7.2.1"),sQuery(id+"F0.wireOp",EDGE,"E7.3.0"),sQuery(id+"F0.wireOp",EDGE,"E7.3.1"),sQuery(id+"F0.wireOp",EDGE,"E7.4.0"),sQuery(id+"F0.wireOp",EDGE,"E7.4.1"),sQuery(id+"F0.wireOp",EDGE,"E8.trimOffspring"),sQuery(id+"F0.wireOp",EDGE,"E9.trimOffspring"),sQuery(id+"F0.wireOp",EDGE,"E10.trimOffspring"),sQuery(id+"F0.wireOp",EDGE,"E11.trimOffspring"),sQuery(id+"F0.wireOp",EDGE,"E12.trimOffspring"),sQuery(id+"F0.wireOp",EDGE,"E13.trimOffspring"),sQuery(id+"F0.wireOp",EDGE,"E14.trimOffspring"),sQuery(id+"F0.wireOp",EDGE,"E15.trimOffspring"),sQuery(id+"F0.wireOp",EDGE,"E16.trimOffspring")])],"isStart":true})]});}
            var Q5;
            {var subQ0=sQuery(id+"F0.wireOp",EDGE,"E7.3.1");Q5=makeQuery(id+"F3.opChamfer","BLEND_EDGE",EDGE,{"blendedFrom":[makeQuery(id+"F1.opExtrude","CAP_EDGE",EDGE,{"disambiguationData":[OSD([subQ0])],"isStart":true}),makeQuery(id+"F1.opExtrude","CAP_FACE",FACE,{"disambiguationData":[OSD([sQuery(id+"F0.wireOp",EDGE,"E0"),sQuery(id+"F0.wireOp",EDGE,"E1"),sQuery(id+"F0.wireOp",EDGE,"E2"),sQuery(id+"F0.wireOp",EDGE,"E3.1.0"),sQuery(id+"F0.wireOp",EDGE,"E3.2.0"),sQuery(id+"F0.wireOp",EDGE,"E3.3.0"),sQuery(id+"F0.wireOp",EDGE,"E3.4.0"),sQuery(id+"F0.wireOp",EDGE,"E4.1.0"),sQuery(id+"F0.wireOp",EDGE,"E4.2.0"),sQuery(id+"F0.wireOp",EDGE,"E4.3.0"),sQuery(id+"F0.wireOp",EDGE,"E4.4.0"),sQuery(id+"F0.wireOp",EDGE,"E5"),sQuery(id+"F0.wireOp",EDGE,"E6"),sQuery(id+"F0.wireOp",EDGE,"E7.1.0"),sQuery(id+"F0.wireOp",EDGE,"E7.1.1"),sQuery(id+"F0.wireOp",EDGE,"E7.2.0"),sQuery(id+"F0.wireOp",EDGE,"E7.2.1"),sQuery(id+"F0.wireOp",EDGE,"E7.3.0"),subQ0,sQuery(id+"F0.wireOp",EDGE,"E7.4.0"),sQuery(id+"F0.wireOp",EDGE,"E7.4.1"),sQuery(id+"F0.wireOp",EDGE,"E8.trimOffspring"),sQuery(id+"F0.wireOp",EDGE,"E9.trimOffspring"),sQuery(id+"F0.wireOp",EDGE,"E10.trimOffspring"),sQuery(id+"F0.wireOp",EDGE,"E11.trimOffspring"),sQuery(id+"F0.wireOp",EDGE,"E12.trimOffspring"),sQuery(id+"F0.wireOp",EDGE,"E13.trimOffspring"),sQuery(id+"F0.wireOp",EDGE,"E14.trimOffspring"),sQuery(id+"F0.wireOp",EDGE,"E15.trimOffspring"),sQuery(id+"F0.wireOp",EDGE,"E16.trimOffspring")])],"isStart":true})],"blendedInto":[makeQuery(id+"F1.opExtrude","CAP_FACE",FACE,{"disambiguationData":[OSD([sQuery(id+"F0.wireOp",EDGE,"E0"),sQuery(id+"F0.wireOp",EDGE,"E1"),sQuery(id+"F0.wireOp",EDGE,"E2"),sQuery(id+"F0.wireOp",EDGE,"E3.1.0"),sQuery(id+"F0.wireOp",EDGE,"E3.2.0"),sQuery(id+"F0.wireOp",EDGE,"E3.3.0"),sQuery(id+"F0.wireOp",EDGE,"E3.4.0"),sQuery(id+"F0.wireOp",EDGE,"E4.1.0"),sQuery(id+"F0.wireOp",EDGE,"E4.2.0"),sQuery(id+"F0.wireOp",EDGE,"E4.3.0"),sQuery(id+"F0.wireOp",EDGE,"E4.4.0"),sQuery(id+"F0.wireOp",EDGE,"E5"),sQuery(id+"F0.wireOp",EDGE,"E6"),sQuery(id+"F0.wireOp",EDGE,"E7.1.0"),sQuery(id+"F0.wireOp",EDGE,"E7.1.1"),sQuery(id+"F0.wireOp",EDGE,"E7.2.0"),sQuery(id+"F0.wireOp",EDGE,"E7.2.1"),sQuery(id+"F0.wireOp",EDGE,"E7.3.0"),subQ0,sQuery(id+"F0.wireOp",EDGE,"E7.4.0"),sQuery(id+"F0.wireOp",EDGE,"E7.4.1"),sQuery(id+"F0.wireOp",EDGE,"E8.trimOffspring"),sQuery(id+"F0.wireOp",EDGE,"E9.trimOffspring"),sQuery(id+"F0.wireOp",EDGE,"E10.trimOffspring"),sQuery(id+"F0.wireOp",EDGE,"E11.trimOffspring"),sQuery(id+"F0.wireOp",EDGE,"E12.trimOffspring"),sQuery(id+"F0.wireOp",EDGE,"E13.trimOffspring"),sQuery(id+"F0.wireOp",EDGE,"E14.trimOffspring"),sQuery(id+"F0.wireOp",EDGE,"E15.trimOffspring"),sQuery(id+"F0.wireOp",EDGE,"E16.trimOffspring")])],"isStart":true})]});}
            var Q6;
            {var subQ0=sQuery(id+"F0.wireOp",EDGE,"E7.3.0");Q6=makeQuery(id+"F3.opChamfer","BLEND_EDGE",EDGE,{"blendedFrom":[makeQuery(id+"F1.opExtrude","CAP_EDGE",EDGE,{"disambiguationData":[OSD([subQ0])],"isStart":true}),makeQuery(id+"F1.opExtrude","CAP_FACE",FACE,{"disambiguationData":[OSD([sQuery(id+"F0.wireOp",EDGE,"E0"),sQuery(id+"F0.wireOp",EDGE,"E1"),sQuery(id+"F0.wireOp",EDGE,"E2"),sQuery(id+"F0.wireOp",EDGE,"E3.1.0"),sQuery(id+"F0.wireOp",EDGE,"E3.2.0"),sQuery(id+"F0.wireOp",EDGE,"E3.3.0"),sQuery(id+"F0.wireOp",EDGE,"E3.4.0"),sQuery(id+"F0.wireOp",EDGE,"E4.1.0"),sQuery(id+"F0.wireOp",EDGE,"E4.2.0"),sQuery(id+"F0.wireOp",EDGE,"E4.3.0"),sQuery(id+"F0.wireOp",EDGE,"E4.4.0"),sQuery(id+"F0.wireOp",EDGE,"E5"),sQuery(id+"F0.wireOp",EDGE,"E6"),sQuery(id+"F0.wireOp",EDGE,"E7.1.0"),sQuery(id+"F0.wireOp",EDGE,"E7.1.1"),sQuery(id+"F0.wireOp",EDGE,"E7.2.0"),sQuery(id+"F0.wireOp",EDGE,"E7.2.1"),subQ0,sQuery(id+"F0.wireOp",EDGE,"E7.3.1"),sQuery(id+"F0.wireOp",EDGE,"E7.4.0"),sQuery(id+"F0.wireOp",EDGE,"E7.4.1"),sQuery(id+"F0.wireOp",EDGE,"E8.trimOffspring"),sQuery(id+"F0.wireOp",EDGE,"E9.trimOffspring"),sQuery(id+"F0.wireOp",EDGE,"E10.trimOffspring"),sQuery(id+"F0.wireOp",EDGE,"E11.trimOffspring"),sQuery(id+"F0.wireOp",EDGE,"E12.trimOffspring"),sQuery(id+"F0.wireOp",EDGE,"E13.trimOffspring"),sQuery(id+"F0.wireOp",EDGE,"E14.trimOffspring"),sQuery(id+"F0.wireOp",EDGE,"E15.trimOffspring"),sQuery(id+"F0.wireOp",EDGE,"E16.trimOffspring")])],"isStart":true})],"blendedInto":[makeQuery(id+"F1.opExtrude","CAP_FACE",FACE,{"disambiguationData":[OSD([sQuery(id+"F0.wireOp",EDGE,"E0"),sQuery(id+"F0.wireOp",EDGE,"E1"),sQuery(id+"F0.wireOp",EDGE,"E2"),sQuery(id+"F0.wireOp",EDGE,"E3.1.0"),sQuery(id+"F0.wireOp",EDGE,"E3.2.0"),sQuery(id+"F0.wireOp",EDGE,"E3.3.0"),sQuery(id+"F0.wireOp",EDGE,"E3.4.0"),sQuery(id+"F0.wireOp",EDGE,"E4.1.0"),sQuery(id+"F0.wireOp",EDGE,"E4.2.0"),sQuery(id+"F0.wireOp",EDGE,"E4.3.0"),sQuery(id+"F0.wireOp",EDGE,"E4.4.0"),sQuery(id+"F0.wireOp",EDGE,"E5"),sQuery(id+"F0.wireOp",EDGE,"E6"),sQuery(id+"F0.wireOp",EDGE,"E7.1.0"),sQuery(id+"F0.wireOp",EDGE,"E7.1.1"),sQuery(id+"F0.wireOp",EDGE,"E7.2.0"),sQuery(id+"F0.wireOp",EDGE,"E7.2.1"),subQ0,sQuery(id+"F0.wireOp",EDGE,"E7.3.1"),sQuery(id+"F0.wireOp",EDGE,"E7.4.0"),sQuery(id+"F0.wireOp",EDGE,"E7.4.1"),sQuery(id+"F0.wireOp",EDGE,"E8.trimOffspring"),sQuery(id+"F0.wireOp",EDGE,"E9.trimOffspring"),sQuery(id+"F0.wireOp",EDGE,"E10.trimOffspring"),sQuery(id+"F0.wireOp",EDGE,"E11.trimOffspring"),sQuery(id+"F0.wireOp",EDGE,"E12.trimOffspring"),sQuery(id+"F0.wireOp",EDGE,"E13.trimOffspring"),sQuery(id+"F0.wireOp",EDGE,"E14.trimOffspring"),sQuery(id+"F0.wireOp",EDGE,"E15.trimOffspring"),sQuery(id+"F0.wireOp",EDGE,"E16.trimOffspring")])],"isStart":true})]});}
            var Q7;
            {var subQ0=sQuery(id+"F0.wireOp",EDGE,"E3.3.0");Q7=makeQuery(id+"F3.opChamfer","BLEND_EDGE",EDGE,{"blendedFrom":[makeQuery(id+"F1.opExtrude","CAP_EDGE",EDGE,{"disambiguationData":[OSD([subQ0])],"isStart":true}),makeQuery(id+"F1.opExtrude","CAP_FACE",FACE,{"disambiguationData":[OSD([sQuery(id+"F0.wireOp",EDGE,"E0"),sQuery(id+"F0.wireOp",EDGE,"E1"),sQuery(id+"F0.wireOp",EDGE,"E2"),sQuery(id+"F0.wireOp",EDGE,"E3.1.0"),sQuery(id+"F0.wireOp",EDGE,"E3.2.0"),subQ0,sQuery(id+"F0.wireOp",EDGE,"E3.4.0"),sQuery(id+"F0.wireOp",EDGE,"E4.1.0"),sQuery(id+"F0.wireOp",EDGE,"E4.2.0"),sQuery(id+"F0.wireOp",EDGE,"E4.3.0"),sQuery(id+"F0.wireOp",EDGE,"E4.4.0"),sQuery(id+"F0.wireOp",EDGE,"E5"),sQuery(id+"F0.wireOp",EDGE,"E6"),sQuery(id+"F0.wireOp",EDGE,"E7.1.0"),sQuery(id+"F0.wireOp",EDGE,"E7.1.1"),sQuery(id+"F0.wireOp",EDGE,"E7.2.0"),sQuery(id+"F0.wireOp",EDGE,"E7.2.1"),sQuery(id+"F0.wireOp",EDGE,"E7.3.0"),sQuery(id+"F0.wireOp",EDGE,"E7.3.1"),sQuery(id+"F0.wireOp",EDGE,"E7.4.0"),sQuery(id+"F0.wireOp",EDGE,"E7.4.1"),sQuery(id+"F0.wireOp",EDGE,"E8.trimOffspring"),sQuery(id+"F0.wireOp",EDGE,"E9.trimOffspring"),sQuery(id+"F0.wireOp",EDGE,"E10.trimOffspring"),sQuery(id+"F0.wireOp",EDGE,"E11.trimOffspring"),sQuery(id+"F0.wireOp",EDGE,"E12.trimOffspring"),sQuery(id+"F0.wireOp",EDGE,"E13.trimOffspring"),sQuery(id+"F0.wireOp",EDGE,"E14.trimOffspring"),sQuery(id+"F0.wireOp",EDGE,"E15.trimOffspring"),sQuery(id+"F0.wireOp",EDGE,"E16.trimOffspring")])],"isStart":true})],"blendedInto":[makeQuery(id+"F1.opExtrude","CAP_FACE",FACE,{"disambiguationData":[OSD([sQuery(id+"F0.wireOp",EDGE,"E0"),sQuery(id+"F0.wireOp",EDGE,"E1"),sQuery(id+"F0.wireOp",EDGE,"E2"),sQuery(id+"F0.wireOp",EDGE,"E3.1.0"),sQuery(id+"F0.wireOp",EDGE,"E3.2.0"),subQ0,sQuery(id+"F0.wireOp",EDGE,"E3.4.0"),sQuery(id+"F0.wireOp",EDGE,"E4.1.0"),sQuery(id+"F0.wireOp",EDGE,"E4.2.0"),sQuery(id+"F0.wireOp",EDGE,"E4.3.0"),sQuery(id+"F0.wireOp",EDGE,"E4.4.0"),sQuery(id+"F0.wireOp",EDGE,"E5"),sQuery(id+"F0.wireOp",EDGE,"E6"),sQuery(id+"F0.wireOp",EDGE,"E7.1.0"),sQuery(id+"F0.wireOp",EDGE,"E7.1.1"),sQuery(id+"F0.wireOp",EDGE,"E7.2.0"),sQuery(id+"F0.wireOp",EDGE,"E7.2.1"),sQuery(id+"F0.wireOp",EDGE,"E7.3.0"),sQuery(id+"F0.wireOp",EDGE,"E7.3.1"),sQuery(id+"F0.wireOp",EDGE,"E7.4.0"),sQuery(id+"F0.wireOp",EDGE,"E7.4.1"),sQuery(id+"F0.wireOp",EDGE,"E8.trimOffspring"),sQuery(id+"F0.wireOp",EDGE,"E9.trimOffspring"),sQuery(id+"F0.wireOp",EDGE,"E10.trimOffspring"),sQuery(id+"F0.wireOp",EDGE,"E11.trimOffspring"),sQuery(id+"F0.wireOp",EDGE,"E12.trimOffspring"),sQuery(id+"F0.wireOp",EDGE,"E13.trimOffspring"),sQuery(id+"F0.wireOp",EDGE,"E14.trimOffspring"),sQuery(id+"F0.wireOp",EDGE,"E15.trimOffspring"),sQuery(id+"F0.wireOp",EDGE,"E16.trimOffspring")])],"isStart":true})]});}
            var Q8;
            {var subQ0=sQuery(id+"F0.wireOp",EDGE,"E4.4.0");Q8=makeQuery(id+"F3.opChamfer","BLEND_EDGE",EDGE,{"blendedFrom":[makeQuery(id+"F1.opExtrude","CAP_EDGE",EDGE,{"disambiguationData":[OSD([subQ0])],"isStart":true}),makeQuery(id+"F1.opExtrude","CAP_FACE",FACE,{"disambiguationData":[OSD([sQuery(id+"F0.wireOp",EDGE,"E0"),sQuery(id+"F0.wireOp",EDGE,"E1"),sQuery(id+"F0.wireOp",EDGE,"E2"),sQuery(id+"F0.wireOp",EDGE,"E3.1.0"),sQuery(id+"F0.wireOp",EDGE,"E3.2.0"),sQuery(id+"F0.wireOp",EDGE,"E3.3.0"),sQuery(id+"F0.wireOp",EDGE,"E3.4.0"),sQuery(id+"F0.wireOp",EDGE,"E4.1.0"),sQuery(id+"F0.wireOp",EDGE,"E4.2.0"),sQuery(id+"F0.wireOp",EDGE,"E4.3.0"),subQ0,sQuery(id+"F0.wireOp",EDGE,"E5"),sQuery(id+"F0.wireOp",EDGE,"E6"),sQuery(id+"F0.wireOp",EDGE,"E7.1.0"),sQuery(id+"F0.wireOp",EDGE,"E7.1.1"),sQuery(id+"F0.wireOp",EDGE,"E7.2.0"),sQuery(id+"F0.wireOp",EDGE,"E7.2.1"),sQuery(id+"F0.wireOp",EDGE,"E7.3.0"),sQuery(id+"F0.wireOp",EDGE,"E7.3.1"),sQuery(id+"F0.wireOp",EDGE,"E7.4.0"),sQuery(id+"F0.wireOp",EDGE,"E7.4.1"),sQuery(id+"F0.wireOp",EDGE,"E8.trimOffspring"),sQuery(id+"F0.wireOp",EDGE,"E9.trimOffspring"),sQuery(id+"F0.wireOp",EDGE,"E10.trimOffspring"),sQuery(id+"F0.wireOp",EDGE,"E11.trimOffspring"),sQuery(id+"F0.wireOp",EDGE,"E12.trimOffspring"),sQuery(id+"F0.wireOp",EDGE,"E13.trimOffspring"),sQuery(id+"F0.wireOp",EDGE,"E14.trimOffspring"),sQuery(id+"F0.wireOp",EDGE,"E15.trimOffspring"),sQuery(id+"F0.wireOp",EDGE,"E16.trimOffspring")])],"isStart":true})],"blendedInto":[makeQuery(id+"F1.opExtrude","CAP_FACE",FACE,{"disambiguationData":[OSD([sQuery(id+"F0.wireOp",EDGE,"E0"),sQuery(id+"F0.wireOp",EDGE,"E1"),sQuery(id+"F0.wireOp",EDGE,"E2"),sQuery(id+"F0.wireOp",EDGE,"E3.1.0"),sQuery(id+"F0.wireOp",EDGE,"E3.2.0"),sQuery(id+"F0.wireOp",EDGE,"E3.3.0"),sQuery(id+"F0.wireOp",EDGE,"E3.4.0"),sQuery(id+"F0.wireOp",EDGE,"E4.1.0"),sQuery(id+"F0.wireOp",EDGE,"E4.2.0"),sQuery(id+"F0.wireOp",EDGE,"E4.3.0"),subQ0,sQuery(id+"F0.wireOp",EDGE,"E5"),sQuery(id+"F0.wireOp",EDGE,"E6"),sQuery(id+"F0.wireOp",EDGE,"E7.1.0"),sQuery(id+"F0.wireOp",EDGE,"E7.1.1"),sQuery(id+"F0.wireOp",EDGE,"E7.2.0"),sQuery(id+"F0.wireOp",EDGE,"E7.2.1"),sQuery(id+"F0.wireOp",EDGE,"E7.3.0"),sQuery(id+"F0.wireOp",EDGE,"E7.3.1"),sQuery(id+"F0.wireOp",EDGE,"E7.4.0"),sQuery(id+"F0.wireOp",EDGE,"E7.4.1"),sQuery(id+"F0.wireOp",EDGE,"E8.trimOffspring"),sQuery(id+"F0.wireOp",EDGE,"E9.trimOffspring"),sQuery(id+"F0.wireOp",EDGE,"E10.trimOffspring"),sQuery(id+"F0.wireOp",EDGE,"E11.trimOffspring"),sQuery(id+"F0.wireOp",EDGE,"E12.trimOffspring"),sQuery(id+"F0.wireOp",EDGE,"E13.trimOffspring"),sQuery(id+"F0.wireOp",EDGE,"E14.trimOffspring"),sQuery(id+"F0.wireOp",EDGE,"E15.trimOffspring"),sQuery(id+"F0.wireOp",EDGE,"E16.trimOffspring")])],"isStart":true})]});}
            var Q9;
            {var subQ0=sQuery(id+"F0.wireOp",EDGE,"E7.4.1");Q9=makeQuery(id+"F3.opChamfer","BLEND_EDGE",EDGE,{"blendedFrom":[makeQuery(id+"F1.opExtrude","CAP_EDGE",EDGE,{"disambiguationData":[OSD([subQ0])],"isStart":true}),makeQuery(id+"F1.opExtrude","CAP_FACE",FACE,{"disambiguationData":[OSD([sQuery(id+"F0.wireOp",EDGE,"E0"),sQuery(id+"F0.wireOp",EDGE,"E1"),sQuery(id+"F0.wireOp",EDGE,"E2"),sQuery(id+"F0.wireOp",EDGE,"E3.1.0"),sQuery(id+"F0.wireOp",EDGE,"E3.2.0"),sQuery(id+"F0.wireOp",EDGE,"E3.3.0"),sQuery(id+"F0.wireOp",EDGE,"E3.4.0"),sQuery(id+"F0.wireOp",EDGE,"E4.1.0"),sQuery(id+"F0.wireOp",EDGE,"E4.2.0"),sQuery(id+"F0.wireOp",EDGE,"E4.3.0"),sQuery(id+"F0.wireOp",EDGE,"E4.4.0"),sQuery(id+"F0.wireOp",EDGE,"E5"),sQuery(id+"F0.wireOp",EDGE,"E6"),sQuery(id+"F0.wireOp",EDGE,"E7.1.0"),sQuery(id+"F0.wireOp",EDGE,"E7.1.1"),sQuery(id+"F0.wireOp",EDGE,"E7.2.0"),sQuery(id+"F0.wireOp",EDGE,"E7.2.1"),sQuery(id+"F0.wireOp",EDGE,"E7.3.0"),sQuery(id+"F0.wireOp",EDGE,"E7.3.1"),sQuery(id+"F0.wireOp",EDGE,"E7.4.0"),subQ0,sQuery(id+"F0.wireOp",EDGE,"E8.trimOffspring"),sQuery(id+"F0.wireOp",EDGE,"E9.trimOffspring"),sQuery(id+"F0.wireOp",EDGE,"E10.trimOffspring"),sQuery(id+"F0.wireOp",EDGE,"E11.trimOffspring"),sQuery(id+"F0.wireOp",EDGE,"E12.trimOffspring"),sQuery(id+"F0.wireOp",EDGE,"E13.trimOffspring"),sQuery(id+"F0.wireOp",EDGE,"E14.trimOffspring"),sQuery(id+"F0.wireOp",EDGE,"E15.trimOffspring"),sQuery(id+"F0.wireOp",EDGE,"E16.trimOffspring")])],"isStart":true})],"blendedInto":[makeQuery(id+"F1.opExtrude","CAP_FACE",FACE,{"disambiguationData":[OSD([sQuery(id+"F0.wireOp",EDGE,"E0"),sQuery(id+"F0.wireOp",EDGE,"E1"),sQuery(id+"F0.wireOp",EDGE,"E2"),sQuery(id+"F0.wireOp",EDGE,"E3.1.0"),sQuery(id+"F0.wireOp",EDGE,"E3.2.0"),sQuery(id+"F0.wireOp",EDGE,"E3.3.0"),sQuery(id+"F0.wireOp",EDGE,"E3.4.0"),sQuery(id+"F0.wireOp",EDGE,"E4.1.0"),sQuery(id+"F0.wireOp",EDGE,"E4.2.0"),sQuery(id+"F0.wireOp",EDGE,"E4.3.0"),sQuery(id+"F0.wireOp",EDGE,"E4.4.0"),sQuery(id+"F0.wireOp",EDGE,"E5"),sQuery(id+"F0.wireOp",EDGE,"E6"),sQuery(id+"F0.wireOp",EDGE,"E7.1.0"),sQuery(id+"F0.wireOp",EDGE,"E7.1.1"),sQuery(id+"F0.wireOp",EDGE,"E7.2.0"),sQuery(id+"F0.wireOp",EDGE,"E7.2.1"),sQuery(id+"F0.wireOp",EDGE,"E7.3.0"),sQuery(id+"F0.wireOp",EDGE,"E7.3.1"),sQuery(id+"F0.wireOp",EDGE,"E7.4.0"),subQ0,sQuery(id+"F0.wireOp",EDGE,"E8.trimOffspring"),sQuery(id+"F0.wireOp",EDGE,"E9.trimOffspring"),sQuery(id+"F0.wireOp",EDGE,"E10.trimOffspring"),sQuery(id+"F0.wireOp",EDGE,"E11.trimOffspring"),sQuery(id+"F0.wireOp",EDGE,"E12.trimOffspring"),sQuery(id+"F0.wireOp",EDGE,"E13.trimOffspring"),sQuery(id+"F0.wireOp",EDGE,"E14.trimOffspring"),sQuery(id+"F0.wireOp",EDGE,"E15.trimOffspring"),sQuery(id+"F0.wireOp",EDGE,"E16.trimOffspring")])],"isStart":true})]});}
            var Q10;
            {var subQ0=sQuery(id+"F0.wireOp",EDGE,"E2");Q10=makeQuery(id+"F3.opChamfer","BLEND_EDGE",EDGE,{"blendedFrom":[makeQuery(id+"F1.opExtrude","CAP_EDGE",EDGE,{"disambiguationData":[OSD([subQ0])],"isStart":true}),makeQuery(id+"F1.opExtrude","CAP_FACE",FACE,{"disambiguationData":[OSD([sQuery(id+"F0.wireOp",EDGE,"E0"),sQuery(id+"F0.wireOp",EDGE,"E1"),subQ0,sQuery(id+"F0.wireOp",EDGE,"E3.1.0"),sQuery(id+"F0.wireOp",EDGE,"E3.2.0"),sQuery(id+"F0.wireOp",EDGE,"E3.3.0"),sQuery(id+"F0.wireOp",EDGE,"E3.4.0"),sQuery(id+"F0.wireOp",EDGE,"E4.1.0"),sQuery(id+"F0.wireOp",EDGE,"E4.2.0"),sQuery(id+"F0.wireOp",EDGE,"E4.3.0"),sQuery(id+"F0.wireOp",EDGE,"E4.4.0"),sQuery(id+"F0.wireOp",EDGE,"E5"),sQuery(id+"F0.wireOp",EDGE,"E6"),sQuery(id+"F0.wireOp",EDGE,"E7.1.0"),sQuery(id+"F0.wireOp",EDGE,"E7.1.1"),sQuery(id+"F0.wireOp",EDGE,"E7.2.0"),sQuery(id+"F0.wireOp",EDGE,"E7.2.1"),sQuery(id+"F0.wireOp",EDGE,"E7.3.0"),sQuery(id+"F0.wireOp",EDGE,"E7.3.1"),sQuery(id+"F0.wireOp",EDGE,"E7.4.0"),sQuery(id+"F0.wireOp",EDGE,"E7.4.1"),sQuery(id+"F0.wireOp",EDGE,"E8.trimOffspring"),sQuery(id+"F0.wireOp",EDGE,"E9.trimOffspring"),sQuery(id+"F0.wireOp",EDGE,"E10.trimOffspring"),sQuery(id+"F0.wireOp",EDGE,"E11.trimOffspring"),sQuery(id+"F0.wireOp",EDGE,"E12.trimOffspring"),sQuery(id+"F0.wireOp",EDGE,"E13.trimOffspring"),sQuery(id+"F0.wireOp",EDGE,"E14.trimOffspring"),sQuery(id+"F0.wireOp",EDGE,"E15.trimOffspring"),sQuery(id+"F0.wireOp",EDGE,"E16.trimOffspring")])],"isStart":true})],"blendedInto":[makeQuery(id+"F1.opExtrude","CAP_FACE",FACE,{"disambiguationData":[OSD([sQuery(id+"F0.wireOp",EDGE,"E0"),sQuery(id+"F0.wireOp",EDGE,"E1"),subQ0,sQuery(id+"F0.wireOp",EDGE,"E3.1.0"),sQuery(id+"F0.wireOp",EDGE,"E3.2.0"),sQuery(id+"F0.wireOp",EDGE,"E3.3.0"),sQuery(id+"F0.wireOp",EDGE,"E3.4.0"),sQuery(id+"F0.wireOp",EDGE,"E4.1.0"),sQuery(id+"F0.wireOp",EDGE,"E4.2.0"),sQuery(id+"F0.wireOp",EDGE,"E4.3.0"),sQuery(id+"F0.wireOp",EDGE,"E4.4.0"),sQuery(id+"F0.wireOp",EDGE,"E5"),sQuery(id+"F0.wireOp",EDGE,"E6"),sQuery(id+"F0.wireOp",EDGE,"E7.1.0"),sQuery(id+"F0.wireOp",EDGE,"E7.1.1"),sQuery(id+"F0.wireOp",EDGE,"E7.2.0"),sQuery(id+"F0.wireOp",EDGE,"E7.2.1"),sQuery(id+"F0.wireOp",EDGE,"E7.3.0"),sQuery(id+"F0.wireOp",EDGE,"E7.3.1"),sQuery(id+"F0.wireOp",EDGE,"E7.4.0"),sQuery(id+"F0.wireOp",EDGE,"E7.4.1"),sQuery(id+"F0.wireOp",EDGE,"E8.trimOffspring"),sQuery(id+"F0.wireOp",EDGE,"E9.trimOffspring"),sQuery(id+"F0.wireOp",EDGE,"E10.trimOffspring"),sQuery(id+"F0.wireOp",EDGE,"E11.trimOffspring"),sQuery(id+"F0.wireOp",EDGE,"E12.trimOffspring"),sQuery(id+"F0.wireOp",EDGE,"E13.trimOffspring"),sQuery(id+"F0.wireOp",EDGE,"E14.trimOffspring"),sQuery(id+"F0.wireOp",EDGE,"E15.trimOffspring"),sQuery(id+"F0.wireOp",EDGE,"E16.trimOffspring")])],"isStart":true})]});}
            var Q11;
            {var subQ0=sQuery(id+"F0.wireOp",EDGE,"E1");Q11=makeQuery(id+"F3.opChamfer","BLEND_EDGE",EDGE,{"blendedFrom":[makeQuery(id+"F1.opExtrude","CAP_EDGE",EDGE,{"disambiguationData":[OSD([subQ0])],"isStart":true}),makeQuery(id+"F1.opExtrude","CAP_FACE",FACE,{"disambiguationData":[OSD([sQuery(id+"F0.wireOp",EDGE,"E0"),subQ0,sQuery(id+"F0.wireOp",EDGE,"E2"),sQuery(id+"F0.wireOp",EDGE,"E3.1.0"),sQuery(id+"F0.wireOp",EDGE,"E3.2.0"),sQuery(id+"F0.wireOp",EDGE,"E3.3.0"),sQuery(id+"F0.wireOp",EDGE,"E3.4.0"),sQuery(id+"F0.wireOp",EDGE,"E4.1.0"),sQuery(id+"F0.wireOp",EDGE,"E4.2.0"),sQuery(id+"F0.wireOp",EDGE,"E4.3.0"),sQuery(id+"F0.wireOp",EDGE,"E4.4.0"),sQuery(id+"F0.wireOp",EDGE,"E5"),sQuery(id+"F0.wireOp",EDGE,"E6"),sQuery(id+"F0.wireOp",EDGE,"E7.1.0"),sQuery(id+"F0.wireOp",EDGE,"E7.1.1"),sQuery(id+"F0.wireOp",EDGE,"E7.2.0"),sQuery(id+"F0.wireOp",EDGE,"E7.2.1"),sQuery(id+"F0.wireOp",EDGE,"E7.3.0"),sQuery(id+"F0.wireOp",EDGE,"E7.3.1"),sQuery(id+"F0.wireOp",EDGE,"E7.4.0"),sQuery(id+"F0.wireOp",EDGE,"E7.4.1"),sQuery(id+"F0.wireOp",EDGE,"E8.trimOffspring"),sQuery(id+"F0.wireOp",EDGE,"E9.trimOffspring"),sQuery(id+"F0.wireOp",EDGE,"E10.trimOffspring"),sQuery(id+"F0.wireOp",EDGE,"E11.trimOffspring"),sQuery(id+"F0.wireOp",EDGE,"E12.trimOffspring"),sQuery(id+"F0.wireOp",EDGE,"E13.trimOffspring"),sQuery(id+"F0.wireOp",EDGE,"E14.trimOffspring"),sQuery(id+"F0.wireOp",EDGE,"E15.trimOffspring"),sQuery(id+"F0.wireOp",EDGE,"E16.trimOffspring")])],"isStart":true})],"blendedInto":[makeQuery(id+"F1.opExtrude","CAP_FACE",FACE,{"disambiguationData":[OSD([sQuery(id+"F0.wireOp",EDGE,"E0"),subQ0,sQuery(id+"F0.wireOp",EDGE,"E2"),sQuery(id+"F0.wireOp",EDGE,"E3.1.0"),sQuery(id+"F0.wireOp",EDGE,"E3.2.0"),sQuery(id+"F0.wireOp",EDGE,"E3.3.0"),sQuery(id+"F0.wireOp",EDGE,"E3.4.0"),sQuery(id+"F0.wireOp",EDGE,"E4.1.0"),sQuery(id+"F0.wireOp",EDGE,"E4.2.0"),sQuery(id+"F0.wireOp",EDGE,"E4.3.0"),sQuery(id+"F0.wireOp",EDGE,"E4.4.0"),sQuery(id+"F0.wireOp",EDGE,"E5"),sQuery(id+"F0.wireOp",EDGE,"E6"),sQuery(id+"F0.wireOp",EDGE,"E7.1.0"),sQuery(id+"F0.wireOp",EDGE,"E7.1.1"),sQuery(id+"F0.wireOp",EDGE,"E7.2.0"),sQuery(id+"F0.wireOp",EDGE,"E7.2.1"),sQuery(id+"F0.wireOp",EDGE,"E7.3.0"),sQuery(id+"F0.wireOp",EDGE,"E7.3.1"),sQuery(id+"F0.wireOp",EDGE,"E7.4.0"),sQuery(id+"F0.wireOp",EDGE,"E7.4.1"),sQuery(id+"F0.wireOp",EDGE,"E8.trimOffspring"),sQuery(id+"F0.wireOp",EDGE,"E9.trimOffspring"),sQuery(id+"F0.wireOp",EDGE,"E10.trimOffspring"),sQuery(id+"F0.wireOp",EDGE,"E11.trimOffspring"),sQuery(id+"F0.wireOp",EDGE,"E12.trimOffspring"),sQuery(id+"F0.wireOp",EDGE,"E13.trimOffspring"),sQuery(id+"F0.wireOp",EDGE,"E14.trimOffspring"),sQuery(id+"F0.wireOp",EDGE,"E15.trimOffspring"),sQuery(id+"F0.wireOp",EDGE,"E16.trimOffspring")])],"isStart":true})]});}
            var Q12;
            {var subQ0=sQuery(id+"F0.wireOp",EDGE,"E4.1.0");Q12=makeQuery(id+"F3.opChamfer","BLEND_EDGE",EDGE,{"blendedFrom":[makeQuery(id+"F1.opExtrude","CAP_EDGE",EDGE,{"disambiguationData":[OSD([subQ0])],"isStart":true}),makeQuery(id+"F1.opExtrude","CAP_FACE",FACE,{"disambiguationData":[OSD([sQuery(id+"F0.wireOp",EDGE,"E0"),sQuery(id+"F0.wireOp",EDGE,"E1"),sQuery(id+"F0.wireOp",EDGE,"E2"),sQuery(id+"F0.wireOp",EDGE,"E3.1.0"),sQuery(id+"F0.wireOp",EDGE,"E3.2.0"),sQuery(id+"F0.wireOp",EDGE,"E3.3.0"),sQuery(id+"F0.wireOp",EDGE,"E3.4.0"),subQ0,sQuery(id+"F0.wireOp",EDGE,"E4.2.0"),sQuery(id+"F0.wireOp",EDGE,"E4.3.0"),sQuery(id+"F0.wireOp",EDGE,"E4.4.0"),sQuery(id+"F0.wireOp",EDGE,"E5"),sQuery(id+"F0.wireOp",EDGE,"E6"),sQuery(id+"F0.wireOp",EDGE,"E7.1.0"),sQuery(id+"F0.wireOp",EDGE,"E7.1.1"),sQuery(id+"F0.wireOp",EDGE,"E7.2.0"),sQuery(id+"F0.wireOp",EDGE,"E7.2.1"),sQuery(id+"F0.wireOp",EDGE,"E7.3.0"),sQuery(id+"F0.wireOp",EDGE,"E7.3.1"),sQuery(id+"F0.wireOp",EDGE,"E7.4.0"),sQuery(id+"F0.wireOp",EDGE,"E7.4.1"),sQuery(id+"F0.wireOp",EDGE,"E8.trimOffspring"),sQuery(id+"F0.wireOp",EDGE,"E9.trimOffspring"),sQuery(id+"F0.wireOp",EDGE,"E10.trimOffspring"),sQuery(id+"F0.wireOp",EDGE,"E11.trimOffspring"),sQuery(id+"F0.wireOp",EDGE,"E12.trimOffspring"),sQuery(id+"F0.wireOp",EDGE,"E13.trimOffspring"),sQuery(id+"F0.wireOp",EDGE,"E14.trimOffspring"),sQuery(id+"F0.wireOp",EDGE,"E15.trimOffspring"),sQuery(id+"F0.wireOp",EDGE,"E16.trimOffspring")])],"isStart":true})],"blendedInto":[makeQuery(id+"F1.opExtrude","CAP_FACE",FACE,{"disambiguationData":[OSD([sQuery(id+"F0.wireOp",EDGE,"E0"),sQuery(id+"F0.wireOp",EDGE,"E1"),sQuery(id+"F0.wireOp",EDGE,"E2"),sQuery(id+"F0.wireOp",EDGE,"E3.1.0"),sQuery(id+"F0.wireOp",EDGE,"E3.2.0"),sQuery(id+"F0.wireOp",EDGE,"E3.3.0"),sQuery(id+"F0.wireOp",EDGE,"E3.4.0"),subQ0,sQuery(id+"F0.wireOp",EDGE,"E4.2.0"),sQuery(id+"F0.wireOp",EDGE,"E4.3.0"),sQuery(id+"F0.wireOp",EDGE,"E4.4.0"),sQuery(id+"F0.wireOp",EDGE,"E5"),sQuery(id+"F0.wireOp",EDGE,"E6"),sQuery(id+"F0.wireOp",EDGE,"E7.1.0"),sQuery(id+"F0.wireOp",EDGE,"E7.1.1"),sQuery(id+"F0.wireOp",EDGE,"E7.2.0"),sQuery(id+"F0.wireOp",EDGE,"E7.2.1"),sQuery(id+"F0.wireOp",EDGE,"E7.3.0"),sQuery(id+"F0.wireOp",EDGE,"E7.3.1"),sQuery(id+"F0.wireOp",EDGE,"E7.4.0"),sQuery(id+"F0.wireOp",EDGE,"E7.4.1"),sQuery(id+"F0.wireOp",EDGE,"E8.trimOffspring"),sQuery(id+"F0.wireOp",EDGE,"E9.trimOffspring"),sQuery(id+"F0.wireOp",EDGE,"E10.trimOffspring"),sQuery(id+"F0.wireOp",EDGE,"E11.trimOffspring"),sQuery(id+"F0.wireOp",EDGE,"E12.trimOffspring"),sQuery(id+"F0.wireOp",EDGE,"E13.trimOffspring"),sQuery(id+"F0.wireOp",EDGE,"E14.trimOffspring"),sQuery(id+"F0.wireOp",EDGE,"E15.trimOffspring"),sQuery(id+"F0.wireOp",EDGE,"E16.trimOffspring")])],"isStart":true})]});}
            var Q13;
            {var subQ0=sQuery(id+"F0.wireOp",EDGE,"E3.1.0");Q13=makeQuery(id+"F3.opChamfer","BLEND_EDGE",EDGE,{"blendedFrom":[makeQuery(id+"F1.opExtrude","CAP_EDGE",EDGE,{"disambiguationData":[OSD([subQ0])],"isStart":true}),makeQuery(id+"F1.opExtrude","CAP_FACE",FACE,{"disambiguationData":[OSD([sQuery(id+"F0.wireOp",EDGE,"E0"),sQuery(id+"F0.wireOp",EDGE,"E1"),sQuery(id+"F0.wireOp",EDGE,"E2"),subQ0,sQuery(id+"F0.wireOp",EDGE,"E3.2.0"),sQuery(id+"F0.wireOp",EDGE,"E3.3.0"),sQuery(id+"F0.wireOp",EDGE,"E3.4.0"),sQuery(id+"F0.wireOp",EDGE,"E4.1.0"),sQuery(id+"F0.wireOp",EDGE,"E4.2.0"),sQuery(id+"F0.wireOp",EDGE,"E4.3.0"),sQuery(id+"F0.wireOp",EDGE,"E4.4.0"),sQuery(id+"F0.wireOp",EDGE,"E5"),sQuery(id+"F0.wireOp",EDGE,"E6"),sQuery(id+"F0.wireOp",EDGE,"E7.1.0"),sQuery(id+"F0.wireOp",EDGE,"E7.1.1"),sQuery(id+"F0.wireOp",EDGE,"E7.2.0"),sQuery(id+"F0.wireOp",EDGE,"E7.2.1"),sQuery(id+"F0.wireOp",EDGE,"E7.3.0"),sQuery(id+"F0.wireOp",EDGE,"E7.3.1"),sQuery(id+"F0.wireOp",EDGE,"E7.4.0"),sQuery(id+"F0.wireOp",EDGE,"E7.4.1"),sQuery(id+"F0.wireOp",EDGE,"E8.trimOffspring"),sQuery(id+"F0.wireOp",EDGE,"E9.trimOffspring"),sQuery(id+"F0.wireOp",EDGE,"E10.trimOffspring"),sQuery(id+"F0.wireOp",EDGE,"E11.trimOffspring"),sQuery(id+"F0.wireOp",EDGE,"E12.trimOffspring"),sQuery(id+"F0.wireOp",EDGE,"E13.trimOffspring"),sQuery(id+"F0.wireOp",EDGE,"E14.trimOffspring"),sQuery(id+"F0.wireOp",EDGE,"E15.trimOffspring"),sQuery(id+"F0.wireOp",EDGE,"E16.trimOffspring")])],"isStart":true})],"blendedInto":[makeQuery(id+"F1.opExtrude","CAP_FACE",FACE,{"disambiguationData":[OSD([sQuery(id+"F0.wireOp",EDGE,"E0"),sQuery(id+"F0.wireOp",EDGE,"E1"),sQuery(id+"F0.wireOp",EDGE,"E2"),subQ0,sQuery(id+"F0.wireOp",EDGE,"E3.2.0"),sQuery(id+"F0.wireOp",EDGE,"E3.3.0"),sQuery(id+"F0.wireOp",EDGE,"E3.4.0"),sQuery(id+"F0.wireOp",EDGE,"E4.1.0"),sQuery(id+"F0.wireOp",EDGE,"E4.2.0"),sQuery(id+"F0.wireOp",EDGE,"E4.3.0"),sQuery(id+"F0.wireOp",EDGE,"E4.4.0"),sQuery(id+"F0.wireOp",EDGE,"E5"),sQuery(id+"F0.wireOp",EDGE,"E6"),sQuery(id+"F0.wireOp",EDGE,"E7.1.0"),sQuery(id+"F0.wireOp",EDGE,"E7.1.1"),sQuery(id+"F0.wireOp",EDGE,"E7.2.0"),sQuery(id+"F0.wireOp",EDGE,"E7.2.1"),sQuery(id+"F0.wireOp",EDGE,"E7.3.0"),sQuery(id+"F0.wireOp",EDGE,"E7.3.1"),sQuery(id+"F0.wireOp",EDGE,"E7.4.0"),sQuery(id+"F0.wireOp",EDGE,"E7.4.1"),sQuery(id+"F0.wireOp",EDGE,"E8.trimOffspring"),sQuery(id+"F0.wireOp",EDGE,"E9.trimOffspring"),sQuery(id+"F0.wireOp",EDGE,"E10.trimOffspring"),sQuery(id+"F0.wireOp",EDGE,"E11.trimOffspring"),sQuery(id+"F0.wireOp",EDGE,"E12.trimOffspring"),sQuery(id+"F0.wireOp",EDGE,"E13.trimOffspring"),sQuery(id+"F0.wireOp",EDGE,"E14.trimOffspring"),sQuery(id+"F0.wireOp",EDGE,"E15.trimOffspring"),sQuery(id+"F0.wireOp",EDGE,"E16.trimOffspring")])],"isStart":true})]});}
            var Q14;
            {var subQ0=sQuery(id+"F0.wireOp",EDGE,"E7.1.1");Q14=makeQuery(id+"F3.opChamfer","BLEND_EDGE",EDGE,{"blendedFrom":[makeQuery(id+"F1.opExtrude","CAP_EDGE",EDGE,{"disambiguationData":[OSD([subQ0])],"isStart":true}),makeQuery(id+"F1.opExtrude","CAP_FACE",FACE,{"disambiguationData":[OSD([sQuery(id+"F0.wireOp",EDGE,"E0"),sQuery(id+"F0.wireOp",EDGE,"E1"),sQuery(id+"F0.wireOp",EDGE,"E2"),sQuery(id+"F0.wireOp",EDGE,"E3.1.0"),sQuery(id+"F0.wireOp",EDGE,"E3.2.0"),sQuery(id+"F0.wireOp",EDGE,"E3.3.0"),sQuery(id+"F0.wireOp",EDGE,"E3.4.0"),sQuery(id+"F0.wireOp",EDGE,"E4.1.0"),sQuery(id+"F0.wireOp",EDGE,"E4.2.0"),sQuery(id+"F0.wireOp",EDGE,"E4.3.0"),sQuery(id+"F0.wireOp",EDGE,"E4.4.0"),sQuery(id+"F0.wireOp",EDGE,"E5"),sQuery(id+"F0.wireOp",EDGE,"E6"),sQuery(id+"F0.wireOp",EDGE,"E7.1.0"),subQ0,sQuery(id+"F0.wireOp",EDGE,"E7.2.0"),sQuery(id+"F0.wireOp",EDGE,"E7.2.1"),sQuery(id+"F0.wireOp",EDGE,"E7.3.0"),sQuery(id+"F0.wireOp",EDGE,"E7.3.1"),sQuery(id+"F0.wireOp",EDGE,"E7.4.0"),sQuery(id+"F0.wireOp",EDGE,"E7.4.1"),sQuery(id+"F0.wireOp",EDGE,"E8.trimOffspring"),sQuery(id+"F0.wireOp",EDGE,"E9.trimOffspring"),sQuery(id+"F0.wireOp",EDGE,"E10.trimOffspring"),sQuery(id+"F0.wireOp",EDGE,"E11.trimOffspring"),sQuery(id+"F0.wireOp",EDGE,"E12.trimOffspring"),sQuery(id+"F0.wireOp",EDGE,"E13.trimOffspring"),sQuery(id+"F0.wireOp",EDGE,"E14.trimOffspring"),sQuery(id+"F0.wireOp",EDGE,"E15.trimOffspring"),sQuery(id+"F0.wireOp",EDGE,"E16.trimOffspring")])],"isStart":true})],"blendedInto":[makeQuery(id+"F1.opExtrude","CAP_FACE",FACE,{"disambiguationData":[OSD([sQuery(id+"F0.wireOp",EDGE,"E0"),sQuery(id+"F0.wireOp",EDGE,"E1"),sQuery(id+"F0.wireOp",EDGE,"E2"),sQuery(id+"F0.wireOp",EDGE,"E3.1.0"),sQuery(id+"F0.wireOp",EDGE,"E3.2.0"),sQuery(id+"F0.wireOp",EDGE,"E3.3.0"),sQuery(id+"F0.wireOp",EDGE,"E3.4.0"),sQuery(id+"F0.wireOp",EDGE,"E4.1.0"),sQuery(id+"F0.wireOp",EDGE,"E4.2.0"),sQuery(id+"F0.wireOp",EDGE,"E4.3.0"),sQuery(id+"F0.wireOp",EDGE,"E4.4.0"),sQuery(id+"F0.wireOp",EDGE,"E5"),sQuery(id+"F0.wireOp",EDGE,"E6"),sQuery(id+"F0.wireOp",EDGE,"E7.1.0"),subQ0,sQuery(id+"F0.wireOp",EDGE,"E7.2.0"),sQuery(id+"F0.wireOp",EDGE,"E7.2.1"),sQuery(id+"F0.wireOp",EDGE,"E7.3.0"),sQuery(id+"F0.wireOp",EDGE,"E7.3.1"),sQuery(id+"F0.wireOp",EDGE,"E7.4.0"),sQuery(id+"F0.wireOp",EDGE,"E7.4.1"),sQuery(id+"F0.wireOp",EDGE,"E8.trimOffspring"),sQuery(id+"F0.wireOp",EDGE,"E9.trimOffspring"),sQuery(id+"F0.wireOp",EDGE,"E10.trimOffspring"),sQuery(id+"F0.wireOp",EDGE,"E11.trimOffspring"),sQuery(id+"F0.wireOp",EDGE,"E12.trimOffspring"),sQuery(id+"F0.wireOp",EDGE,"E13.trimOffspring"),sQuery(id+"F0.wireOp",EDGE,"E14.trimOffspring"),sQuery(id+"F0.wireOp",EDGE,"E15.trimOffspring"),sQuery(id+"F0.wireOp",EDGE,"E16.trimOffspring")])],"isStart":true})]});}
            var Q15;
            {var subQ0=sQuery(id+"F0.wireOp",EDGE,"E6");Q15=makeQuery(id+"F3.opChamfer","BLEND_EDGE",EDGE,{"blendedFrom":[makeQuery(id+"F1.opExtrude","CAP_EDGE",EDGE,{"disambiguationData":[OSD([subQ0])],"isStart":true}),makeQuery(id+"F1.opExtrude","CAP_FACE",FACE,{"disambiguationData":[OSD([sQuery(id+"F0.wireOp",EDGE,"E0"),sQuery(id+"F0.wireOp",EDGE,"E1"),sQuery(id+"F0.wireOp",EDGE,"E2"),sQuery(id+"F0.wireOp",EDGE,"E3.1.0"),sQuery(id+"F0.wireOp",EDGE,"E3.2.0"),sQuery(id+"F0.wireOp",EDGE,"E3.3.0"),sQuery(id+"F0.wireOp",EDGE,"E3.4.0"),sQuery(id+"F0.wireOp",EDGE,"E4.1.0"),sQuery(id+"F0.wireOp",EDGE,"E4.2.0"),sQuery(id+"F0.wireOp",EDGE,"E4.3.0"),sQuery(id+"F0.wireOp",EDGE,"E4.4.0"),sQuery(id+"F0.wireOp",EDGE,"E5"),subQ0,sQuery(id+"F0.wireOp",EDGE,"E7.1.0"),sQuery(id+"F0.wireOp",EDGE,"E7.1.1"),sQuery(id+"F0.wireOp",EDGE,"E7.2.0"),sQuery(id+"F0.wireOp",EDGE,"E7.2.1"),sQuery(id+"F0.wireOp",EDGE,"E7.3.0"),sQuery(id+"F0.wireOp",EDGE,"E7.3.1"),sQuery(id+"F0.wireOp",EDGE,"E7.4.0"),sQuery(id+"F0.wireOp",EDGE,"E7.4.1"),sQuery(id+"F0.wireOp",EDGE,"E8.trimOffspring"),sQuery(id+"F0.wireOp",EDGE,"E9.trimOffspring"),sQuery(id+"F0.wireOp",EDGE,"E10.trimOffspring"),sQuery(id+"F0.wireOp",EDGE,"E11.trimOffspring"),sQuery(id+"F0.wireOp",EDGE,"E12.trimOffspring"),sQuery(id+"F0.wireOp",EDGE,"E13.trimOffspring"),sQuery(id+"F0.wireOp",EDGE,"E14.trimOffspring"),sQuery(id+"F0.wireOp",EDGE,"E15.trimOffspring"),sQuery(id+"F0.wireOp",EDGE,"E16.trimOffspring")])],"isStart":true})],"blendedInto":[makeQuery(id+"F1.opExtrude","CAP_FACE",FACE,{"disambiguationData":[OSD([sQuery(id+"F0.wireOp",EDGE,"E0"),sQuery(id+"F0.wireOp",EDGE,"E1"),sQuery(id+"F0.wireOp",EDGE,"E2"),sQuery(id+"F0.wireOp",EDGE,"E3.1.0"),sQuery(id+"F0.wireOp",EDGE,"E3.2.0"),sQuery(id+"F0.wireOp",EDGE,"E3.3.0"),sQuery(id+"F0.wireOp",EDGE,"E3.4.0"),sQuery(id+"F0.wireOp",EDGE,"E4.1.0"),sQuery(id+"F0.wireOp",EDGE,"E4.2.0"),sQuery(id+"F0.wireOp",EDGE,"E4.3.0"),sQuery(id+"F0.wireOp",EDGE,"E4.4.0"),sQuery(id+"F0.wireOp",EDGE,"E5"),subQ0,sQuery(id+"F0.wireOp",EDGE,"E7.1.0"),sQuery(id+"F0.wireOp",EDGE,"E7.1.1"),sQuery(id+"F0.wireOp",EDGE,"E7.2.0"),sQuery(id+"F0.wireOp",EDGE,"E7.2.1"),sQuery(id+"F0.wireOp",EDGE,"E7.3.0"),sQuery(id+"F0.wireOp",EDGE,"E7.3.1"),sQuery(id+"F0.wireOp",EDGE,"E7.4.0"),sQuery(id+"F0.wireOp",EDGE,"E7.4.1"),sQuery(id+"F0.wireOp",EDGE,"E8.trimOffspring"),sQuery(id+"F0.wireOp",EDGE,"E9.trimOffspring"),sQuery(id+"F0.wireOp",EDGE,"E10.trimOffspring"),sQuery(id+"F0.wireOp",EDGE,"E11.trimOffspring"),sQuery(id+"F0.wireOp",EDGE,"E12.trimOffspring"),sQuery(id+"F0.wireOp",EDGE,"E13.trimOffspring"),sQuery(id+"F0.wireOp",EDGE,"E14.trimOffspring"),sQuery(id+"F0.wireOp",EDGE,"E15.trimOffspring"),sQuery(id+"F0.wireOp",EDGE,"E16.trimOffspring")])],"isStart":true})]});}
            var Q16;
            {var subQ0=sQuery(id+"F0.wireOp",EDGE,"E7.1.0");Q16=makeQuery(id+"F3.opChamfer","BLEND_EDGE",EDGE,{"blendedFrom":[makeQuery(id+"F1.opExtrude","CAP_EDGE",EDGE,{"disambiguationData":[OSD([subQ0])],"isStart":true}),makeQuery(id+"F1.opExtrude","CAP_FACE",FACE,{"disambiguationData":[OSD([sQuery(id+"F0.wireOp",EDGE,"E0"),sQuery(id+"F0.wireOp",EDGE,"E1"),sQuery(id+"F0.wireOp",EDGE,"E2"),sQuery(id+"F0.wireOp",EDGE,"E3.1.0"),sQuery(id+"F0.wireOp",EDGE,"E3.2.0"),sQuery(id+"F0.wireOp",EDGE,"E3.3.0"),sQuery(id+"F0.wireOp",EDGE,"E3.4.0"),sQuery(id+"F0.wireOp",EDGE,"E4.1.0"),sQuery(id+"F0.wireOp",EDGE,"E4.2.0"),sQuery(id+"F0.wireOp",EDGE,"E4.3.0"),sQuery(id+"F0.wireOp",EDGE,"E4.4.0"),sQuery(id+"F0.wireOp",EDGE,"E5"),sQuery(id+"F0.wireOp",EDGE,"E6"),subQ0,sQuery(id+"F0.wireOp",EDGE,"E7.1.1"),sQuery(id+"F0.wireOp",EDGE,"E7.2.0"),sQuery(id+"F0.wireOp",EDGE,"E7.2.1"),sQuery(id+"F0.wireOp",EDGE,"E7.3.0"),sQuery(id+"F0.wireOp",EDGE,"E7.3.1"),sQuery(id+"F0.wireOp",EDGE,"E7.4.0"),sQuery(id+"F0.wireOp",EDGE,"E7.4.1"),sQuery(id+"F0.wireOp",EDGE,"E8.trimOffspring"),sQuery(id+"F0.wireOp",EDGE,"E9.trimOffspring"),sQuery(id+"F0.wireOp",EDGE,"E10.trimOffspring"),sQuery(id+"F0.wireOp",EDGE,"E11.trimOffspring"),sQuery(id+"F0.wireOp",EDGE,"E12.trimOffspring"),sQuery(id+"F0.wireOp",EDGE,"E13.trimOffspring"),sQuery(id+"F0.wireOp",EDGE,"E14.trimOffspring"),sQuery(id+"F0.wireOp",EDGE,"E15.trimOffspring"),sQuery(id+"F0.wireOp",EDGE,"E16.trimOffspring")])],"isStart":true})],"blendedInto":[makeQuery(id+"F1.opExtrude","CAP_FACE",FACE,{"disambiguationData":[OSD([sQuery(id+"F0.wireOp",EDGE,"E0"),sQuery(id+"F0.wireOp",EDGE,"E1"),sQuery(id+"F0.wireOp",EDGE,"E2"),sQuery(id+"F0.wireOp",EDGE,"E3.1.0"),sQuery(id+"F0.wireOp",EDGE,"E3.2.0"),sQuery(id+"F0.wireOp",EDGE,"E3.3.0"),sQuery(id+"F0.wireOp",EDGE,"E3.4.0"),sQuery(id+"F0.wireOp",EDGE,"E4.1.0"),sQuery(id+"F0.wireOp",EDGE,"E4.2.0"),sQuery(id+"F0.wireOp",EDGE,"E4.3.0"),sQuery(id+"F0.wireOp",EDGE,"E4.4.0"),sQuery(id+"F0.wireOp",EDGE,"E5"),sQuery(id+"F0.wireOp",EDGE,"E6"),subQ0,sQuery(id+"F0.wireOp",EDGE,"E7.1.1"),sQuery(id+"F0.wireOp",EDGE,"E7.2.0"),sQuery(id+"F0.wireOp",EDGE,"E7.2.1"),sQuery(id+"F0.wireOp",EDGE,"E7.3.0"),sQuery(id+"F0.wireOp",EDGE,"E7.3.1"),sQuery(id+"F0.wireOp",EDGE,"E7.4.0"),sQuery(id+"F0.wireOp",EDGE,"E7.4.1"),sQuery(id+"F0.wireOp",EDGE,"E8.trimOffspring"),sQuery(id+"F0.wireOp",EDGE,"E9.trimOffspring"),sQuery(id+"F0.wireOp",EDGE,"E10.trimOffspring"),sQuery(id+"F0.wireOp",EDGE,"E11.trimOffspring"),sQuery(id+"F0.wireOp",EDGE,"E12.trimOffspring"),sQuery(id+"F0.wireOp",EDGE,"E13.trimOffspring"),sQuery(id+"F0.wireOp",EDGE,"E14.trimOffspring"),sQuery(id+"F0.wireOp",EDGE,"E15.trimOffspring"),sQuery(id+"F0.wireOp",EDGE,"E16.trimOffspring")])],"isStart":true})]});}
            var Q17;
            {var subQ0=sQuery(id+"F0.wireOp",EDGE,"E7.4.0");Q17=makeQuery(id+"F3.opChamfer","BLEND_EDGE",EDGE,{"blendedFrom":[makeQuery(id+"F1.opExtrude","CAP_EDGE",EDGE,{"disambiguationData":[OSD([subQ0])],"isStart":true}),makeQuery(id+"F1.opExtrude","CAP_FACE",FACE,{"disambiguationData":[OSD([sQuery(id+"F0.wireOp",EDGE,"E0"),sQuery(id+"F0.wireOp",EDGE,"E1"),sQuery(id+"F0.wireOp",EDGE,"E2"),sQuery(id+"F0.wireOp",EDGE,"E3.1.0"),sQuery(id+"F0.wireOp",EDGE,"E3.2.0"),sQuery(id+"F0.wireOp",EDGE,"E3.3.0"),sQuery(id+"F0.wireOp",EDGE,"E3.4.0"),sQuery(id+"F0.wireOp",EDGE,"E4.1.0"),sQuery(id+"F0.wireOp",EDGE,"E4.2.0"),sQuery(id+"F0.wireOp",EDGE,"E4.3.0"),sQuery(id+"F0.wireOp",EDGE,"E4.4.0"),sQuery(id+"F0.wireOp",EDGE,"E5"),sQuery(id+"F0.wireOp",EDGE,"E6"),sQuery(id+"F0.wireOp",EDGE,"E7.1.0"),sQuery(id+"F0.wireOp",EDGE,"E7.1.1"),sQuery(id+"F0.wireOp",EDGE,"E7.2.0"),sQuery(id+"F0.wireOp",EDGE,"E7.2.1"),sQuery(id+"F0.wireOp",EDGE,"E7.3.0"),sQuery(id+"F0.wireOp",EDGE,"E7.3.1"),subQ0,sQuery(id+"F0.wireOp",EDGE,"E7.4.1"),sQuery(id+"F0.wireOp",EDGE,"E8.trimOffspring"),sQuery(id+"F0.wireOp",EDGE,"E9.trimOffspring"),sQuery(id+"F0.wireOp",EDGE,"E10.trimOffspring"),sQuery(id+"F0.wireOp",EDGE,"E11.trimOffspring"),sQuery(id+"F0.wireOp",EDGE,"E12.trimOffspring"),sQuery(id+"F0.wireOp",EDGE,"E13.trimOffspring"),sQuery(id+"F0.wireOp",EDGE,"E14.trimOffspring"),sQuery(id+"F0.wireOp",EDGE,"E15.trimOffspring"),sQuery(id+"F0.wireOp",EDGE,"E16.trimOffspring")])],"isStart":true})],"blendedInto":[makeQuery(id+"F1.opExtrude","CAP_FACE",FACE,{"disambiguationData":[OSD([sQuery(id+"F0.wireOp",EDGE,"E0"),sQuery(id+"F0.wireOp",EDGE,"E1"),sQuery(id+"F0.wireOp",EDGE,"E2"),sQuery(id+"F0.wireOp",EDGE,"E3.1.0"),sQuery(id+"F0.wireOp",EDGE,"E3.2.0"),sQuery(id+"F0.wireOp",EDGE,"E3.3.0"),sQuery(id+"F0.wireOp",EDGE,"E3.4.0"),sQuery(id+"F0.wireOp",EDGE,"E4.1.0"),sQuery(id+"F0.wireOp",EDGE,"E4.2.0"),sQuery(id+"F0.wireOp",EDGE,"E4.3.0"),sQuery(id+"F0.wireOp",EDGE,"E4.4.0"),sQuery(id+"F0.wireOp",EDGE,"E5"),sQuery(id+"F0.wireOp",EDGE,"E6"),sQuery(id+"F0.wireOp",EDGE,"E7.1.0"),sQuery(id+"F0.wireOp",EDGE,"E7.1.1"),sQuery(id+"F0.wireOp",EDGE,"E7.2.0"),sQuery(id+"F0.wireOp",EDGE,"E7.2.1"),sQuery(id+"F0.wireOp",EDGE,"E7.3.0"),sQuery(id+"F0.wireOp",EDGE,"E7.3.1"),subQ0,sQuery(id+"F0.wireOp",EDGE,"E7.4.1"),sQuery(id+"F0.wireOp",EDGE,"E8.trimOffspring"),sQuery(id+"F0.wireOp",EDGE,"E9.trimOffspring"),sQuery(id+"F0.wireOp",EDGE,"E10.trimOffspring"),sQuery(id+"F0.wireOp",EDGE,"E11.trimOffspring"),sQuery(id+"F0.wireOp",EDGE,"E12.trimOffspring"),sQuery(id+"F0.wireOp",EDGE,"E13.trimOffspring"),sQuery(id+"F0.wireOp",EDGE,"E14.trimOffspring"),sQuery(id+"F0.wireOp",EDGE,"E15.trimOffspring"),sQuery(id+"F0.wireOp",EDGE,"E16.trimOffspring")])],"isStart":true})]});}
            var Q18;
            {var subQ0=sQuery(id+"F0.wireOp",EDGE,"E3.4.0");Q18=makeQuery(id+"F3.opChamfer","BLEND_EDGE",EDGE,{"blendedFrom":[makeQuery(id+"F1.opExtrude","CAP_EDGE",EDGE,{"disambiguationData":[OSD([subQ0])],"isStart":true}),makeQuery(id+"F1.opExtrude","CAP_FACE",FACE,{"disambiguationData":[OSD([sQuery(id+"F0.wireOp",EDGE,"E0"),sQuery(id+"F0.wireOp",EDGE,"E1"),sQuery(id+"F0.wireOp",EDGE,"E2"),sQuery(id+"F0.wireOp",EDGE,"E3.1.0"),sQuery(id+"F0.wireOp",EDGE,"E3.2.0"),sQuery(id+"F0.wireOp",EDGE,"E3.3.0"),subQ0,sQuery(id+"F0.wireOp",EDGE,"E4.1.0"),sQuery(id+"F0.wireOp",EDGE,"E4.2.0"),sQuery(id+"F0.wireOp",EDGE,"E4.3.0"),sQuery(id+"F0.wireOp",EDGE,"E4.4.0"),sQuery(id+"F0.wireOp",EDGE,"E5"),sQuery(id+"F0.wireOp",EDGE,"E6"),sQuery(id+"F0.wireOp",EDGE,"E7.1.0"),sQuery(id+"F0.wireOp",EDGE,"E7.1.1"),sQuery(id+"F0.wireOp",EDGE,"E7.2.0"),sQuery(id+"F0.wireOp",EDGE,"E7.2.1"),sQuery(id+"F0.wireOp",EDGE,"E7.3.0"),sQuery(id+"F0.wireOp",EDGE,"E7.3.1"),sQuery(id+"F0.wireOp",EDGE,"E7.4.0"),sQuery(id+"F0.wireOp",EDGE,"E7.4.1"),sQuery(id+"F0.wireOp",EDGE,"E8.trimOffspring"),sQuery(id+"F0.wireOp",EDGE,"E9.trimOffspring"),sQuery(id+"F0.wireOp",EDGE,"E10.trimOffspring"),sQuery(id+"F0.wireOp",EDGE,"E11.trimOffspring"),sQuery(id+"F0.wireOp",EDGE,"E12.trimOffspring"),sQuery(id+"F0.wireOp",EDGE,"E13.trimOffspring"),sQuery(id+"F0.wireOp",EDGE,"E14.trimOffspring"),sQuery(id+"F0.wireOp",EDGE,"E15.trimOffspring"),sQuery(id+"F0.wireOp",EDGE,"E16.trimOffspring")])],"isStart":true})],"blendedInto":[makeQuery(id+"F1.opExtrude","CAP_FACE",FACE,{"disambiguationData":[OSD([sQuery(id+"F0.wireOp",EDGE,"E0"),sQuery(id+"F0.wireOp",EDGE,"E1"),sQuery(id+"F0.wireOp",EDGE,"E2"),sQuery(id+"F0.wireOp",EDGE,"E3.1.0"),sQuery(id+"F0.wireOp",EDGE,"E3.2.0"),sQuery(id+"F0.wireOp",EDGE,"E3.3.0"),subQ0,sQuery(id+"F0.wireOp",EDGE,"E4.1.0"),sQuery(id+"F0.wireOp",EDGE,"E4.2.0"),sQuery(id+"F0.wireOp",EDGE,"E4.3.0"),sQuery(id+"F0.wireOp",EDGE,"E4.4.0"),sQuery(id+"F0.wireOp",EDGE,"E5"),sQuery(id+"F0.wireOp",EDGE,"E6"),sQuery(id+"F0.wireOp",EDGE,"E7.1.0"),sQuery(id+"F0.wireOp",EDGE,"E7.1.1"),sQuery(id+"F0.wireOp",EDGE,"E7.2.0"),sQuery(id+"F0.wireOp",EDGE,"E7.2.1"),sQuery(id+"F0.wireOp",EDGE,"E7.3.0"),sQuery(id+"F0.wireOp",EDGE,"E7.3.1"),sQuery(id+"F0.wireOp",EDGE,"E7.4.0"),sQuery(id+"F0.wireOp",EDGE,"E7.4.1"),sQuery(id+"F0.wireOp",EDGE,"E8.trimOffspring"),sQuery(id+"F0.wireOp",EDGE,"E9.trimOffspring"),sQuery(id+"F0.wireOp",EDGE,"E10.trimOffspring"),sQuery(id+"F0.wireOp",EDGE,"E11.trimOffspring"),sQuery(id+"F0.wireOp",EDGE,"E12.trimOffspring"),sQuery(id+"F0.wireOp",EDGE,"E13.trimOffspring"),sQuery(id+"F0.wireOp",EDGE,"E14.trimOffspring"),sQuery(id+"F0.wireOp",EDGE,"E15.trimOffspring"),sQuery(id+"F0.wireOp",EDGE,"E16.trimOffspring")])],"isStart":true})]});}
            var Q19;
            {var subQ0=sQuery(id+"F0.wireOp",EDGE,"E5");Q19=makeQuery(id+"F3.opChamfer","BLEND_EDGE",EDGE,{"blendedFrom":[makeQuery(id+"F1.opExtrude","CAP_EDGE",EDGE,{"disambiguationData":[OSD([subQ0])],"isStart":true}),makeQuery(id+"F1.opExtrude","CAP_FACE",FACE,{"disambiguationData":[OSD([sQuery(id+"F0.wireOp",EDGE,"E0"),sQuery(id+"F0.wireOp",EDGE,"E1"),sQuery(id+"F0.wireOp",EDGE,"E2"),sQuery(id+"F0.wireOp",EDGE,"E3.1.0"),sQuery(id+"F0.wireOp",EDGE,"E3.2.0"),sQuery(id+"F0.wireOp",EDGE,"E3.3.0"),sQuery(id+"F0.wireOp",EDGE,"E3.4.0"),sQuery(id+"F0.wireOp",EDGE,"E4.1.0"),sQuery(id+"F0.wireOp",EDGE,"E4.2.0"),sQuery(id+"F0.wireOp",EDGE,"E4.3.0"),sQuery(id+"F0.wireOp",EDGE,"E4.4.0"),subQ0,sQuery(id+"F0.wireOp",EDGE,"E6"),sQuery(id+"F0.wireOp",EDGE,"E7.1.0"),sQuery(id+"F0.wireOp",EDGE,"E7.1.1"),sQuery(id+"F0.wireOp",EDGE,"E7.2.0"),sQuery(id+"F0.wireOp",EDGE,"E7.2.1"),sQuery(id+"F0.wireOp",EDGE,"E7.3.0"),sQuery(id+"F0.wireOp",EDGE,"E7.3.1"),sQuery(id+"F0.wireOp",EDGE,"E7.4.0"),sQuery(id+"F0.wireOp",EDGE,"E7.4.1"),sQuery(id+"F0.wireOp",EDGE,"E8.trimOffspring"),sQuery(id+"F0.wireOp",EDGE,"E9.trimOffspring"),sQuery(id+"F0.wireOp",EDGE,"E10.trimOffspring"),sQuery(id+"F0.wireOp",EDGE,"E11.trimOffspring"),sQuery(id+"F0.wireOp",EDGE,"E12.trimOffspring"),sQuery(id+"F0.wireOp",EDGE,"E13.trimOffspring"),sQuery(id+"F0.wireOp",EDGE,"E14.trimOffspring"),sQuery(id+"F0.wireOp",EDGE,"E15.trimOffspring"),sQuery(id+"F0.wireOp",EDGE,"E16.trimOffspring")])],"isStart":true})],"blendedInto":[makeQuery(id+"F1.opExtrude","CAP_FACE",FACE,{"disambiguationData":[OSD([sQuery(id+"F0.wireOp",EDGE,"E0"),sQuery(id+"F0.wireOp",EDGE,"E1"),sQuery(id+"F0.wireOp",EDGE,"E2"),sQuery(id+"F0.wireOp",EDGE,"E3.1.0"),sQuery(id+"F0.wireOp",EDGE,"E3.2.0"),sQuery(id+"F0.wireOp",EDGE,"E3.3.0"),sQuery(id+"F0.wireOp",EDGE,"E3.4.0"),sQuery(id+"F0.wireOp",EDGE,"E4.1.0"),sQuery(id+"F0.wireOp",EDGE,"E4.2.0"),sQuery(id+"F0.wireOp",EDGE,"E4.3.0"),sQuery(id+"F0.wireOp",EDGE,"E4.4.0"),subQ0,sQuery(id+"F0.wireOp",EDGE,"E6"),sQuery(id+"F0.wireOp",EDGE,"E7.1.0"),sQuery(id+"F0.wireOp",EDGE,"E7.1.1"),sQuery(id+"F0.wireOp",EDGE,"E7.2.0"),sQuery(id+"F0.wireOp",EDGE,"E7.2.1"),sQuery(id+"F0.wireOp",EDGE,"E7.3.0"),sQuery(id+"F0.wireOp",EDGE,"E7.3.1"),sQuery(id+"F0.wireOp",EDGE,"E7.4.0"),sQuery(id+"F0.wireOp",EDGE,"E7.4.1"),sQuery(id+"F0.wireOp",EDGE,"E8.trimOffspring"),sQuery(id+"F0.wireOp",EDGE,"E9.trimOffspring"),sQuery(id+"F0.wireOp",EDGE,"E10.trimOffspring"),sQuery(id+"F0.wireOp",EDGE,"E11.trimOffspring"),sQuery(id+"F0.wireOp",EDGE,"E12.trimOffspring"),sQuery(id+"F0.wireOp",EDGE,"E13.trimOffspring"),sQuery(id+"F0.wireOp",EDGE,"E14.trimOffspring"),sQuery(id+"F0.wireOp",EDGE,"E15.trimOffspring"),sQuery(id+"F0.wireOp",EDGE,"E16.trimOffspring")])],"isStart":true})]});}
            fillet(context, id + "F4", {"entities" : qUnion([Q0, Q1, Q2, Q3, Q4, Q5, Q6, Q7, Q8, Q9, Q10, Q11, Q12, Q13, Q14, Q15, Q16, Q17, Q18, Q19]), "radius" : 2.5 * mm, "tangentPropagation" : true, "allowEdgeOverflow" : false});
        }
        {
            var Q0;
            {var subQ0=sQuery(id+"F0.wireOp",EDGE,"E7.1.1");Q0=makeQuery(id+"F2.opChamfer","BLEND_EDGE",EDGE,{"blendedFrom":[makeQuery(id+"F1.opExtrude","CAP_EDGE",EDGE,{"disambiguationData":[OSD([subQ0])],"isStart":false}),makeQuery(id+"F1.opExtrude","CAP_FACE",FACE,{"disambiguationData":[OSD([sQuery(id+"F0.wireOp",EDGE,"E0"),sQuery(id+"F0.wireOp",EDGE,"E1"),sQuery(id+"F0.wireOp",EDGE,"E2"),sQuery(id+"F0.wireOp",EDGE,"E3.1.0"),sQuery(id+"F0.wireOp",EDGE,"E3.2.0"),sQuery(id+"F0.wireOp",EDGE,"E3.3.0"),sQuery(id+"F0.wireOp",EDGE,"E3.4.0"),sQuery(id+"F0.wireOp",EDGE,"E4.1.0"),sQuery(id+"F0.wireOp",EDGE,"E4.2.0"),sQuery(id+"F0.wireOp",EDGE,"E4.3.0"),sQuery(id+"F0.wireOp",EDGE,"E4.4.0"),sQuery(id+"F0.wireOp",EDGE,"E5"),sQuery(id+"F0.wireOp",EDGE,"E6"),sQuery(id+"F0.wireOp",EDGE,"E7.1.0"),subQ0,sQuery(id+"F0.wireOp",EDGE,"E7.2.0"),sQuery(id+"F0.wireOp",EDGE,"E7.2.1"),sQuery(id+"F0.wireOp",EDGE,"E7.3.0"),sQuery(id+"F0.wireOp",EDGE,"E7.3.1"),sQuery(id+"F0.wireOp",EDGE,"E7.4.0"),sQuery(id+"F0.wireOp",EDGE,"E7.4.1"),sQuery(id+"F0.wireOp",EDGE,"E8.trimOffspring"),sQuery(id+"F0.wireOp",EDGE,"E9.trimOffspring"),sQuery(id+"F0.wireOp",EDGE,"E10.trimOffspring"),sQuery(id+"F0.wireOp",EDGE,"E11.trimOffspring"),sQuery(id+"F0.wireOp",EDGE,"E12.trimOffspring"),sQuery(id+"F0.wireOp",EDGE,"E13.trimOffspring"),sQuery(id+"F0.wireOp",EDGE,"E14.trimOffspring"),sQuery(id+"F0.wireOp",EDGE,"E15.trimOffspring"),sQuery(id+"F0.wireOp",EDGE,"E16.trimOffspring")])],"isStart":false})],"blendedInto":[makeQuery(id+"F1.opExtrude","CAP_FACE",FACE,{"disambiguationData":[OSD([sQuery(id+"F0.wireOp",EDGE,"E0"),sQuery(id+"F0.wireOp",EDGE,"E1"),sQuery(id+"F0.wireOp",EDGE,"E2"),sQuery(id+"F0.wireOp",EDGE,"E3.1.0"),sQuery(id+"F0.wireOp",EDGE,"E3.2.0"),sQuery(id+"F0.wireOp",EDGE,"E3.3.0"),sQuery(id+"F0.wireOp",EDGE,"E3.4.0"),sQuery(id+"F0.wireOp",EDGE,"E4.1.0"),sQuery(id+"F0.wireOp",EDGE,"E4.2.0"),sQuery(id+"F0.wireOp",EDGE,"E4.3.0"),sQuery(id+"F0.wireOp",EDGE,"E4.4.0"),sQuery(id+"F0.wireOp",EDGE,"E5"),sQuery(id+"F0.wireOp",EDGE,"E6"),sQuery(id+"F0.wireOp",EDGE,"E7.1.0"),subQ0,sQuery(id+"F0.wireOp",EDGE,"E7.2.0"),sQuery(id+"F0.wireOp",EDGE,"E7.2.1"),sQuery(id+"F0.wireOp",EDGE,"E7.3.0"),sQuery(id+"F0.wireOp",EDGE,"E7.3.1"),sQuery(id+"F0.wireOp",EDGE,"E7.4.0"),sQuery(id+"F0.wireOp",EDGE,"E7.4.1"),sQuery(id+"F0.wireOp",EDGE,"E8.trimOffspring"),sQuery(id+"F0.wireOp",EDGE,"E9.trimOffspring"),sQuery(id+"F0.wireOp",EDGE,"E10.trimOffspring"),sQuery(id+"F0.wireOp",EDGE,"E11.trimOffspring"),sQuery(id+"F0.wireOp",EDGE,"E12.trimOffspring"),sQuery(id+"F0.wireOp",EDGE,"E13.trimOffspring"),sQuery(id+"F0.wireOp",EDGE,"E14.trimOffspring"),sQuery(id+"F0.wireOp",EDGE,"E15.trimOffspring"),sQuery(id+"F0.wireOp",EDGE,"E16.trimOffspring")])],"isStart":false})]});}
            var Q1;
            {var subQ0=sQuery(id+"F0.wireOp",EDGE,"E7.1.0");Q1=makeQuery(id+"F2.opChamfer","BLEND_EDGE",EDGE,{"blendedFrom":[makeQuery(id+"F1.opExtrude","CAP_EDGE",EDGE,{"disambiguationData":[OSD([subQ0])],"isStart":false}),makeQuery(id+"F1.opExtrude","CAP_FACE",FACE,{"disambiguationData":[OSD([sQuery(id+"F0.wireOp",EDGE,"E0"),sQuery(id+"F0.wireOp",EDGE,"E1"),sQuery(id+"F0.wireOp",EDGE,"E2"),sQuery(id+"F0.wireOp",EDGE,"E3.1.0"),sQuery(id+"F0.wireOp",EDGE,"E3.2.0"),sQuery(id+"F0.wireOp",EDGE,"E3.3.0"),sQuery(id+"F0.wireOp",EDGE,"E3.4.0"),sQuery(id+"F0.wireOp",EDGE,"E4.1.0"),sQuery(id+"F0.wireOp",EDGE,"E4.2.0"),sQuery(id+"F0.wireOp",EDGE,"E4.3.0"),sQuery(id+"F0.wireOp",EDGE,"E4.4.0"),sQuery(id+"F0.wireOp",EDGE,"E5"),sQuery(id+"F0.wireOp",EDGE,"E6"),subQ0,sQuery(id+"F0.wireOp",EDGE,"E7.1.1"),sQuery(id+"F0.wireOp",EDGE,"E7.2.0"),sQuery(id+"F0.wireOp",EDGE,"E7.2.1"),sQuery(id+"F0.wireOp",EDGE,"E7.3.0"),sQuery(id+"F0.wireOp",EDGE,"E7.3.1"),sQuery(id+"F0.wireOp",EDGE,"E7.4.0"),sQuery(id+"F0.wireOp",EDGE,"E7.4.1"),sQuery(id+"F0.wireOp",EDGE,"E8.trimOffspring"),sQuery(id+"F0.wireOp",EDGE,"E9.trimOffspring"),sQuery(id+"F0.wireOp",EDGE,"E10.trimOffspring"),sQuery(id+"F0.wireOp",EDGE,"E11.trimOffspring"),sQuery(id+"F0.wireOp",EDGE,"E12.trimOffspring"),sQuery(id+"F0.wireOp",EDGE,"E13.trimOffspring"),sQuery(id+"F0.wireOp",EDGE,"E14.trimOffspring"),sQuery(id+"F0.wireOp",EDGE,"E15.trimOffspring"),sQuery(id+"F0.wireOp",EDGE,"E16.trimOffspring")])],"isStart":false})],"blendedInto":[makeQuery(id+"F1.opExtrude","CAP_FACE",FACE,{"disambiguationData":[OSD([sQuery(id+"F0.wireOp",EDGE,"E0"),sQuery(id+"F0.wireOp",EDGE,"E1"),sQuery(id+"F0.wireOp",EDGE,"E2"),sQuery(id+"F0.wireOp",EDGE,"E3.1.0"),sQuery(id+"F0.wireOp",EDGE,"E3.2.0"),sQuery(id+"F0.wireOp",EDGE,"E3.3.0"),sQuery(id+"F0.wireOp",EDGE,"E3.4.0"),sQuery(id+"F0.wireOp",EDGE,"E4.1.0"),sQuery(id+"F0.wireOp",EDGE,"E4.2.0"),sQuery(id+"F0.wireOp",EDGE,"E4.3.0"),sQuery(id+"F0.wireOp",EDGE,"E4.4.0"),sQuery(id+"F0.wireOp",EDGE,"E5"),sQuery(id+"F0.wireOp",EDGE,"E6"),subQ0,sQuery(id+"F0.wireOp",EDGE,"E7.1.1"),sQuery(id+"F0.wireOp",EDGE,"E7.2.0"),sQuery(id+"F0.wireOp",EDGE,"E7.2.1"),sQuery(id+"F0.wireOp",EDGE,"E7.3.0"),sQuery(id+"F0.wireOp",EDGE,"E7.3.1"),sQuery(id+"F0.wireOp",EDGE,"E7.4.0"),sQuery(id+"F0.wireOp",EDGE,"E7.4.1"),sQuery(id+"F0.wireOp",EDGE,"E8.trimOffspring"),sQuery(id+"F0.wireOp",EDGE,"E9.trimOffspring"),sQuery(id+"F0.wireOp",EDGE,"E10.trimOffspring"),sQuery(id+"F0.wireOp",EDGE,"E11.trimOffspring"),sQuery(id+"F0.wireOp",EDGE,"E12.trimOffspring"),sQuery(id+"F0.wireOp",EDGE,"E13.trimOffspring"),sQuery(id+"F0.wireOp",EDGE,"E14.trimOffspring"),sQuery(id+"F0.wireOp",EDGE,"E15.trimOffspring"),sQuery(id+"F0.wireOp",EDGE,"E16.trimOffspring")])],"isStart":false})]});}
            var Q2;
            {var subQ0=sQuery(id+"F0.wireOp",EDGE,"E3.1.0");Q2=makeQuery(id+"F2.opChamfer","BLEND_EDGE",EDGE,{"blendedFrom":[makeQuery(id+"F1.opExtrude","CAP_EDGE",EDGE,{"disambiguationData":[OSD([subQ0])],"isStart":false}),makeQuery(id+"F1.opExtrude","CAP_FACE",FACE,{"disambiguationData":[OSD([sQuery(id+"F0.wireOp",EDGE,"E0"),sQuery(id+"F0.wireOp",EDGE,"E1"),sQuery(id+"F0.wireOp",EDGE,"E2"),subQ0,sQuery(id+"F0.wireOp",EDGE,"E3.2.0"),sQuery(id+"F0.wireOp",EDGE,"E3.3.0"),sQuery(id+"F0.wireOp",EDGE,"E3.4.0"),sQuery(id+"F0.wireOp",EDGE,"E4.1.0"),sQuery(id+"F0.wireOp",EDGE,"E4.2.0"),sQuery(id+"F0.wireOp",EDGE,"E4.3.0"),sQuery(id+"F0.wireOp",EDGE,"E4.4.0"),sQuery(id+"F0.wireOp",EDGE,"E5"),sQuery(id+"F0.wireOp",EDGE,"E6"),sQuery(id+"F0.wireOp",EDGE,"E7.1.0"),sQuery(id+"F0.wireOp",EDGE,"E7.1.1"),sQuery(id+"F0.wireOp",EDGE,"E7.2.0"),sQuery(id+"F0.wireOp",EDGE,"E7.2.1"),sQuery(id+"F0.wireOp",EDGE,"E7.3.0"),sQuery(id+"F0.wireOp",EDGE,"E7.3.1"),sQuery(id+"F0.wireOp",EDGE,"E7.4.0"),sQuery(id+"F0.wireOp",EDGE,"E7.4.1"),sQuery(id+"F0.wireOp",EDGE,"E8.trimOffspring"),sQuery(id+"F0.wireOp",EDGE,"E9.trimOffspring"),sQuery(id+"F0.wireOp",EDGE,"E10.trimOffspring"),sQuery(id+"F0.wireOp",EDGE,"E11.trimOffspring"),sQuery(id+"F0.wireOp",EDGE,"E12.trimOffspring"),sQuery(id+"F0.wireOp",EDGE,"E13.trimOffspring"),sQuery(id+"F0.wireOp",EDGE,"E14.trimOffspring"),sQuery(id+"F0.wireOp",EDGE,"E15.trimOffspring"),sQuery(id+"F0.wireOp",EDGE,"E16.trimOffspring")])],"isStart":false})],"blendedInto":[makeQuery(id+"F1.opExtrude","CAP_FACE",FACE,{"disambiguationData":[OSD([sQuery(id+"F0.wireOp",EDGE,"E0"),sQuery(id+"F0.wireOp",EDGE,"E1"),sQuery(id+"F0.wireOp",EDGE,"E2"),subQ0,sQuery(id+"F0.wireOp",EDGE,"E3.2.0"),sQuery(id+"F0.wireOp",EDGE,"E3.3.0"),sQuery(id+"F0.wireOp",EDGE,"E3.4.0"),sQuery(id+"F0.wireOp",EDGE,"E4.1.0"),sQuery(id+"F0.wireOp",EDGE,"E4.2.0"),sQuery(id+"F0.wireOp",EDGE,"E4.3.0"),sQuery(id+"F0.wireOp",EDGE,"E4.4.0"),sQuery(id+"F0.wireOp",EDGE,"E5"),sQuery(id+"F0.wireOp",EDGE,"E6"),sQuery(id+"F0.wireOp",EDGE,"E7.1.0"),sQuery(id+"F0.wireOp",EDGE,"E7.1.1"),sQuery(id+"F0.wireOp",EDGE,"E7.2.0"),sQuery(id+"F0.wireOp",EDGE,"E7.2.1"),sQuery(id+"F0.wireOp",EDGE,"E7.3.0"),sQuery(id+"F0.wireOp",EDGE,"E7.3.1"),sQuery(id+"F0.wireOp",EDGE,"E7.4.0"),sQuery(id+"F0.wireOp",EDGE,"E7.4.1"),sQuery(id+"F0.wireOp",EDGE,"E8.trimOffspring"),sQuery(id+"F0.wireOp",EDGE,"E9.trimOffspring"),sQuery(id+"F0.wireOp",EDGE,"E10.trimOffspring"),sQuery(id+"F0.wireOp",EDGE,"E11.trimOffspring"),sQuery(id+"F0.wireOp",EDGE,"E12.trimOffspring"),sQuery(id+"F0.wireOp",EDGE,"E13.trimOffspring"),sQuery(id+"F0.wireOp",EDGE,"E14.trimOffspring"),sQuery(id+"F0.wireOp",EDGE,"E15.trimOffspring"),sQuery(id+"F0.wireOp",EDGE,"E16.trimOffspring")])],"isStart":false})]});}
            var Q3;
            {var subQ0=sQuery(id+"F0.wireOp",EDGE,"E4.1.0");Q3=makeQuery(id+"F2.opChamfer","BLEND_EDGE",EDGE,{"blendedFrom":[makeQuery(id+"F1.opExtrude","CAP_EDGE",EDGE,{"disambiguationData":[OSD([subQ0])],"isStart":false}),makeQuery(id+"F1.opExtrude","CAP_FACE",FACE,{"disambiguationData":[OSD([sQuery(id+"F0.wireOp",EDGE,"E0"),sQuery(id+"F0.wireOp",EDGE,"E1"),sQuery(id+"F0.wireOp",EDGE,"E2"),sQuery(id+"F0.wireOp",EDGE,"E3.1.0"),sQuery(id+"F0.wireOp",EDGE,"E3.2.0"),sQuery(id+"F0.wireOp",EDGE,"E3.3.0"),sQuery(id+"F0.wireOp",EDGE,"E3.4.0"),subQ0,sQuery(id+"F0.wireOp",EDGE,"E4.2.0"),sQuery(id+"F0.wireOp",EDGE,"E4.3.0"),sQuery(id+"F0.wireOp",EDGE,"E4.4.0"),sQuery(id+"F0.wireOp",EDGE,"E5"),sQuery(id+"F0.wireOp",EDGE,"E6"),sQuery(id+"F0.wireOp",EDGE,"E7.1.0"),sQuery(id+"F0.wireOp",EDGE,"E7.1.1"),sQuery(id+"F0.wireOp",EDGE,"E7.2.0"),sQuery(id+"F0.wireOp",EDGE,"E7.2.1"),sQuery(id+"F0.wireOp",EDGE,"E7.3.0"),sQuery(id+"F0.wireOp",EDGE,"E7.3.1"),sQuery(id+"F0.wireOp",EDGE,"E7.4.0"),sQuery(id+"F0.wireOp",EDGE,"E7.4.1"),sQuery(id+"F0.wireOp",EDGE,"E8.trimOffspring"),sQuery(id+"F0.wireOp",EDGE,"E9.trimOffspring"),sQuery(id+"F0.wireOp",EDGE,"E10.trimOffspring"),sQuery(id+"F0.wireOp",EDGE,"E11.trimOffspring"),sQuery(id+"F0.wireOp",EDGE,"E12.trimOffspring"),sQuery(id+"F0.wireOp",EDGE,"E13.trimOffspring"),sQuery(id+"F0.wireOp",EDGE,"E14.trimOffspring"),sQuery(id+"F0.wireOp",EDGE,"E15.trimOffspring"),sQuery(id+"F0.wireOp",EDGE,"E16.trimOffspring")])],"isStart":false})],"blendedInto":[makeQuery(id+"F1.opExtrude","CAP_FACE",FACE,{"disambiguationData":[OSD([sQuery(id+"F0.wireOp",EDGE,"E0"),sQuery(id+"F0.wireOp",EDGE,"E1"),sQuery(id+"F0.wireOp",EDGE,"E2"),sQuery(id+"F0.wireOp",EDGE,"E3.1.0"),sQuery(id+"F0.wireOp",EDGE,"E3.2.0"),sQuery(id+"F0.wireOp",EDGE,"E3.3.0"),sQuery(id+"F0.wireOp",EDGE,"E3.4.0"),subQ0,sQuery(id+"F0.wireOp",EDGE,"E4.2.0"),sQuery(id+"F0.wireOp",EDGE,"E4.3.0"),sQuery(id+"F0.wireOp",EDGE,"E4.4.0"),sQuery(id+"F0.wireOp",EDGE,"E5"),sQuery(id+"F0.wireOp",EDGE,"E6"),sQuery(id+"F0.wireOp",EDGE,"E7.1.0"),sQuery(id+"F0.wireOp",EDGE,"E7.1.1"),sQuery(id+"F0.wireOp",EDGE,"E7.2.0"),sQuery(id+"F0.wireOp",EDGE,"E7.2.1"),sQuery(id+"F0.wireOp",EDGE,"E7.3.0"),sQuery(id+"F0.wireOp",EDGE,"E7.3.1"),sQuery(id+"F0.wireOp",EDGE,"E7.4.0"),sQuery(id+"F0.wireOp",EDGE,"E7.4.1"),sQuery(id+"F0.wireOp",EDGE,"E8.trimOffspring"),sQuery(id+"F0.wireOp",EDGE,"E9.trimOffspring"),sQuery(id+"F0.wireOp",EDGE,"E10.trimOffspring"),sQuery(id+"F0.wireOp",EDGE,"E11.trimOffspring"),sQuery(id+"F0.wireOp",EDGE,"E12.trimOffspring"),sQuery(id+"F0.wireOp",EDGE,"E13.trimOffspring"),sQuery(id+"F0.wireOp",EDGE,"E14.trimOffspring"),sQuery(id+"F0.wireOp",EDGE,"E15.trimOffspring"),sQuery(id+"F0.wireOp",EDGE,"E16.trimOffspring")])],"isStart":false})]});}
            var Q4;
            {var subQ0=sQuery(id+"F0.wireOp",EDGE,"E1");Q4=makeQuery(id+"F2.opChamfer","BLEND_EDGE",EDGE,{"blendedFrom":[makeQuery(id+"F1.opExtrude","CAP_EDGE",EDGE,{"disambiguationData":[OSD([subQ0])],"isStart":false}),makeQuery(id+"F1.opExtrude","CAP_FACE",FACE,{"disambiguationData":[OSD([sQuery(id+"F0.wireOp",EDGE,"E0"),subQ0,sQuery(id+"F0.wireOp",EDGE,"E2"),sQuery(id+"F0.wireOp",EDGE,"E3.1.0"),sQuery(id+"F0.wireOp",EDGE,"E3.2.0"),sQuery(id+"F0.wireOp",EDGE,"E3.3.0"),sQuery(id+"F0.wireOp",EDGE,"E3.4.0"),sQuery(id+"F0.wireOp",EDGE,"E4.1.0"),sQuery(id+"F0.wireOp",EDGE,"E4.2.0"),sQuery(id+"F0.wireOp",EDGE,"E4.3.0"),sQuery(id+"F0.wireOp",EDGE,"E4.4.0"),sQuery(id+"F0.wireOp",EDGE,"E5"),sQuery(id+"F0.wireOp",EDGE,"E6"),sQuery(id+"F0.wireOp",EDGE,"E7.1.0"),sQuery(id+"F0.wireOp",EDGE,"E7.1.1"),sQuery(id+"F0.wireOp",EDGE,"E7.2.0"),sQuery(id+"F0.wireOp",EDGE,"E7.2.1"),sQuery(id+"F0.wireOp",EDGE,"E7.3.0"),sQuery(id+"F0.wireOp",EDGE,"E7.3.1"),sQuery(id+"F0.wireOp",EDGE,"E7.4.0"),sQuery(id+"F0.wireOp",EDGE,"E7.4.1"),sQuery(id+"F0.wireOp",EDGE,"E8.trimOffspring"),sQuery(id+"F0.wireOp",EDGE,"E9.trimOffspring"),sQuery(id+"F0.wireOp",EDGE,"E10.trimOffspring"),sQuery(id+"F0.wireOp",EDGE,"E11.trimOffspring"),sQuery(id+"F0.wireOp",EDGE,"E12.trimOffspring"),sQuery(id+"F0.wireOp",EDGE,"E13.trimOffspring"),sQuery(id+"F0.wireOp",EDGE,"E14.trimOffspring"),sQuery(id+"F0.wireOp",EDGE,"E15.trimOffspring"),sQuery(id+"F0.wireOp",EDGE,"E16.trimOffspring")])],"isStart":false})],"blendedInto":[makeQuery(id+"F1.opExtrude","CAP_FACE",FACE,{"disambiguationData":[OSD([sQuery(id+"F0.wireOp",EDGE,"E0"),subQ0,sQuery(id+"F0.wireOp",EDGE,"E2"),sQuery(id+"F0.wireOp",EDGE,"E3.1.0"),sQuery(id+"F0.wireOp",EDGE,"E3.2.0"),sQuery(id+"F0.wireOp",EDGE,"E3.3.0"),sQuery(id+"F0.wireOp",EDGE,"E3.4.0"),sQuery(id+"F0.wireOp",EDGE,"E4.1.0"),sQuery(id+"F0.wireOp",EDGE,"E4.2.0"),sQuery(id+"F0.wireOp",EDGE,"E4.3.0"),sQuery(id+"F0.wireOp",EDGE,"E4.4.0"),sQuery(id+"F0.wireOp",EDGE,"E5"),sQuery(id+"F0.wireOp",EDGE,"E6"),sQuery(id+"F0.wireOp",EDGE,"E7.1.0"),sQuery(id+"F0.wireOp",EDGE,"E7.1.1"),sQuery(id+"F0.wireOp",EDGE,"E7.2.0"),sQuery(id+"F0.wireOp",EDGE,"E7.2.1"),sQuery(id+"F0.wireOp",EDGE,"E7.3.0"),sQuery(id+"F0.wireOp",EDGE,"E7.3.1"),sQuery(id+"F0.wireOp",EDGE,"E7.4.0"),sQuery(id+"F0.wireOp",EDGE,"E7.4.1"),sQuery(id+"F0.wireOp",EDGE,"E8.trimOffspring"),sQuery(id+"F0.wireOp",EDGE,"E9.trimOffspring"),sQuery(id+"F0.wireOp",EDGE,"E10.trimOffspring"),sQuery(id+"F0.wireOp",EDGE,"E11.trimOffspring"),sQuery(id+"F0.wireOp",EDGE,"E12.trimOffspring"),sQuery(id+"F0.wireOp",EDGE,"E13.trimOffspring"),sQuery(id+"F0.wireOp",EDGE,"E14.trimOffspring"),sQuery(id+"F0.wireOp",EDGE,"E15.trimOffspring"),sQuery(id+"F0.wireOp",EDGE,"E16.trimOffspring")])],"isStart":false})]});}
            var Q5;
            {var subQ0=sQuery(id+"F0.wireOp",EDGE,"E6");Q5=makeQuery(id+"F2.opChamfer","BLEND_EDGE",EDGE,{"blendedFrom":[makeQuery(id+"F1.opExtrude","CAP_EDGE",EDGE,{"disambiguationData":[OSD([subQ0])],"isStart":false}),makeQuery(id+"F1.opExtrude","CAP_FACE",FACE,{"disambiguationData":[OSD([sQuery(id+"F0.wireOp",EDGE,"E0"),sQuery(id+"F0.wireOp",EDGE,"E1"),sQuery(id+"F0.wireOp",EDGE,"E2"),sQuery(id+"F0.wireOp",EDGE,"E3.1.0"),sQuery(id+"F0.wireOp",EDGE,"E3.2.0"),sQuery(id+"F0.wireOp",EDGE,"E3.3.0"),sQuery(id+"F0.wireOp",EDGE,"E3.4.0"),sQuery(id+"F0.wireOp",EDGE,"E4.1.0"),sQuery(id+"F0.wireOp",EDGE,"E4.2.0"),sQuery(id+"F0.wireOp",EDGE,"E4.3.0"),sQuery(id+"F0.wireOp",EDGE,"E4.4.0"),sQuery(id+"F0.wireOp",EDGE,"E5"),subQ0,sQuery(id+"F0.wireOp",EDGE,"E7.1.0"),sQuery(id+"F0.wireOp",EDGE,"E7.1.1"),sQuery(id+"F0.wireOp",EDGE,"E7.2.0"),sQuery(id+"F0.wireOp",EDGE,"E7.2.1"),sQuery(id+"F0.wireOp",EDGE,"E7.3.0"),sQuery(id+"F0.wireOp",EDGE,"E7.3.1"),sQuery(id+"F0.wireOp",EDGE,"E7.4.0"),sQuery(id+"F0.wireOp",EDGE,"E7.4.1"),sQuery(id+"F0.wireOp",EDGE,"E8.trimOffspring"),sQuery(id+"F0.wireOp",EDGE,"E9.trimOffspring"),sQuery(id+"F0.wireOp",EDGE,"E10.trimOffspring"),sQuery(id+"F0.wireOp",EDGE,"E11.trimOffspring"),sQuery(id+"F0.wireOp",EDGE,"E12.trimOffspring"),sQuery(id+"F0.wireOp",EDGE,"E13.trimOffspring"),sQuery(id+"F0.wireOp",EDGE,"E14.trimOffspring"),sQuery(id+"F0.wireOp",EDGE,"E15.trimOffspring"),sQuery(id+"F0.wireOp",EDGE,"E16.trimOffspring")])],"isStart":false})],"blendedInto":[makeQuery(id+"F1.opExtrude","CAP_FACE",FACE,{"disambiguationData":[OSD([sQuery(id+"F0.wireOp",EDGE,"E0"),sQuery(id+"F0.wireOp",EDGE,"E1"),sQuery(id+"F0.wireOp",EDGE,"E2"),sQuery(id+"F0.wireOp",EDGE,"E3.1.0"),sQuery(id+"F0.wireOp",EDGE,"E3.2.0"),sQuery(id+"F0.wireOp",EDGE,"E3.3.0"),sQuery(id+"F0.wireOp",EDGE,"E3.4.0"),sQuery(id+"F0.wireOp",EDGE,"E4.1.0"),sQuery(id+"F0.wireOp",EDGE,"E4.2.0"),sQuery(id+"F0.wireOp",EDGE,"E4.3.0"),sQuery(id+"F0.wireOp",EDGE,"E4.4.0"),sQuery(id+"F0.wireOp",EDGE,"E5"),subQ0,sQuery(id+"F0.wireOp",EDGE,"E7.1.0"),sQuery(id+"F0.wireOp",EDGE,"E7.1.1"),sQuery(id+"F0.wireOp",EDGE,"E7.2.0"),sQuery(id+"F0.wireOp",EDGE,"E7.2.1"),sQuery(id+"F0.wireOp",EDGE,"E7.3.0"),sQuery(id+"F0.wireOp",EDGE,"E7.3.1"),sQuery(id+"F0.wireOp",EDGE,"E7.4.0"),sQuery(id+"F0.wireOp",EDGE,"E7.4.1"),sQuery(id+"F0.wireOp",EDGE,"E8.trimOffspring"),sQuery(id+"F0.wireOp",EDGE,"E9.trimOffspring"),sQuery(id+"F0.wireOp",EDGE,"E10.trimOffspring"),sQuery(id+"F0.wireOp",EDGE,"E11.trimOffspring"),sQuery(id+"F0.wireOp",EDGE,"E12.trimOffspring"),sQuery(id+"F0.wireOp",EDGE,"E13.trimOffspring"),sQuery(id+"F0.wireOp",EDGE,"E14.trimOffspring"),sQuery(id+"F0.wireOp",EDGE,"E15.trimOffspring"),sQuery(id+"F0.wireOp",EDGE,"E16.trimOffspring")])],"isStart":false})]});}
            var Q6;
            {var subQ0=sQuery(id+"F0.wireOp",EDGE,"E2");Q6=makeQuery(id+"F2.opChamfer","BLEND_EDGE",EDGE,{"blendedFrom":[makeQuery(id+"F1.opExtrude","CAP_EDGE",EDGE,{"disambiguationData":[OSD([subQ0])],"isStart":false}),makeQuery(id+"F1.opExtrude","CAP_FACE",FACE,{"disambiguationData":[OSD([sQuery(id+"F0.wireOp",EDGE,"E0"),sQuery(id+"F0.wireOp",EDGE,"E1"),subQ0,sQuery(id+"F0.wireOp",EDGE,"E3.1.0"),sQuery(id+"F0.wireOp",EDGE,"E3.2.0"),sQuery(id+"F0.wireOp",EDGE,"E3.3.0"),sQuery(id+"F0.wireOp",EDGE,"E3.4.0"),sQuery(id+"F0.wireOp",EDGE,"E4.1.0"),sQuery(id+"F0.wireOp",EDGE,"E4.2.0"),sQuery(id+"F0.wireOp",EDGE,"E4.3.0"),sQuery(id+"F0.wireOp",EDGE,"E4.4.0"),sQuery(id+"F0.wireOp",EDGE,"E5"),sQuery(id+"F0.wireOp",EDGE,"E6"),sQuery(id+"F0.wireOp",EDGE,"E7.1.0"),sQuery(id+"F0.wireOp",EDGE,"E7.1.1"),sQuery(id+"F0.wireOp",EDGE,"E7.2.0"),sQuery(id+"F0.wireOp",EDGE,"E7.2.1"),sQuery(id+"F0.wireOp",EDGE,"E7.3.0"),sQuery(id+"F0.wireOp",EDGE,"E7.3.1"),sQuery(id+"F0.wireOp",EDGE,"E7.4.0"),sQuery(id+"F0.wireOp",EDGE,"E7.4.1"),sQuery(id+"F0.wireOp",EDGE,"E8.trimOffspring"),sQuery(id+"F0.wireOp",EDGE,"E9.trimOffspring"),sQuery(id+"F0.wireOp",EDGE,"E10.trimOffspring"),sQuery(id+"F0.wireOp",EDGE,"E11.trimOffspring"),sQuery(id+"F0.wireOp",EDGE,"E12.trimOffspring"),sQuery(id+"F0.wireOp",EDGE,"E13.trimOffspring"),sQuery(id+"F0.wireOp",EDGE,"E14.trimOffspring"),sQuery(id+"F0.wireOp",EDGE,"E15.trimOffspring"),sQuery(id+"F0.wireOp",EDGE,"E16.trimOffspring")])],"isStart":false})],"blendedInto":[makeQuery(id+"F1.opExtrude","CAP_FACE",FACE,{"disambiguationData":[OSD([sQuery(id+"F0.wireOp",EDGE,"E0"),sQuery(id+"F0.wireOp",EDGE,"E1"),subQ0,sQuery(id+"F0.wireOp",EDGE,"E3.1.0"),sQuery(id+"F0.wireOp",EDGE,"E3.2.0"),sQuery(id+"F0.wireOp",EDGE,"E3.3.0"),sQuery(id+"F0.wireOp",EDGE,"E3.4.0"),sQuery(id+"F0.wireOp",EDGE,"E4.1.0"),sQuery(id+"F0.wireOp",EDGE,"E4.2.0"),sQuery(id+"F0.wireOp",EDGE,"E4.3.0"),sQuery(id+"F0.wireOp",EDGE,"E4.4.0"),sQuery(id+"F0.wireOp",EDGE,"E5"),sQuery(id+"F0.wireOp",EDGE,"E6"),sQuery(id+"F0.wireOp",EDGE,"E7.1.0"),sQuery(id+"F0.wireOp",EDGE,"E7.1.1"),sQuery(id+"F0.wireOp",EDGE,"E7.2.0"),sQuery(id+"F0.wireOp",EDGE,"E7.2.1"),sQuery(id+"F0.wireOp",EDGE,"E7.3.0"),sQuery(id+"F0.wireOp",EDGE,"E7.3.1"),sQuery(id+"F0.wireOp",EDGE,"E7.4.0"),sQuery(id+"F0.wireOp",EDGE,"E7.4.1"),sQuery(id+"F0.wireOp",EDGE,"E8.trimOffspring"),sQuery(id+"F0.wireOp",EDGE,"E9.trimOffspring"),sQuery(id+"F0.wireOp",EDGE,"E10.trimOffspring"),sQuery(id+"F0.wireOp",EDGE,"E11.trimOffspring"),sQuery(id+"F0.wireOp",EDGE,"E12.trimOffspring"),sQuery(id+"F0.wireOp",EDGE,"E13.trimOffspring"),sQuery(id+"F0.wireOp",EDGE,"E14.trimOffspring"),sQuery(id+"F0.wireOp",EDGE,"E15.trimOffspring"),sQuery(id+"F0.wireOp",EDGE,"E16.trimOffspring")])],"isStart":false})]});}
            var Q7;
            {var subQ0=sQuery(id+"F0.wireOp",EDGE,"E5");Q7=makeQuery(id+"F2.opChamfer","BLEND_EDGE",EDGE,{"blendedFrom":[makeQuery(id+"F1.opExtrude","CAP_EDGE",EDGE,{"disambiguationData":[OSD([subQ0])],"isStart":false}),makeQuery(id+"F1.opExtrude","CAP_FACE",FACE,{"disambiguationData":[OSD([sQuery(id+"F0.wireOp",EDGE,"E0"),sQuery(id+"F0.wireOp",EDGE,"E1"),sQuery(id+"F0.wireOp",EDGE,"E2"),sQuery(id+"F0.wireOp",EDGE,"E3.1.0"),sQuery(id+"F0.wireOp",EDGE,"E3.2.0"),sQuery(id+"F0.wireOp",EDGE,"E3.3.0"),sQuery(id+"F0.wireOp",EDGE,"E3.4.0"),sQuery(id+"F0.wireOp",EDGE,"E4.1.0"),sQuery(id+"F0.wireOp",EDGE,"E4.2.0"),sQuery(id+"F0.wireOp",EDGE,"E4.3.0"),sQuery(id+"F0.wireOp",EDGE,"E4.4.0"),subQ0,sQuery(id+"F0.wireOp",EDGE,"E6"),sQuery(id+"F0.wireOp",EDGE,"E7.1.0"),sQuery(id+"F0.wireOp",EDGE,"E7.1.1"),sQuery(id+"F0.wireOp",EDGE,"E7.2.0"),sQuery(id+"F0.wireOp",EDGE,"E7.2.1"),sQuery(id+"F0.wireOp",EDGE,"E7.3.0"),sQuery(id+"F0.wireOp",EDGE,"E7.3.1"),sQuery(id+"F0.wireOp",EDGE,"E7.4.0"),sQuery(id+"F0.wireOp",EDGE,"E7.4.1"),sQuery(id+"F0.wireOp",EDGE,"E8.trimOffspring"),sQuery(id+"F0.wireOp",EDGE,"E9.trimOffspring"),sQuery(id+"F0.wireOp",EDGE,"E10.trimOffspring"),sQuery(id+"F0.wireOp",EDGE,"E11.trimOffspring"),sQuery(id+"F0.wireOp",EDGE,"E12.trimOffspring"),sQuery(id+"F0.wireOp",EDGE,"E13.trimOffspring"),sQuery(id+"F0.wireOp",EDGE,"E14.trimOffspring"),sQuery(id+"F0.wireOp",EDGE,"E15.trimOffspring"),sQuery(id+"F0.wireOp",EDGE,"E16.trimOffspring")])],"isStart":false})],"blendedInto":[makeQuery(id+"F1.opExtrude","CAP_FACE",FACE,{"disambiguationData":[OSD([sQuery(id+"F0.wireOp",EDGE,"E0"),sQuery(id+"F0.wireOp",EDGE,"E1"),sQuery(id+"F0.wireOp",EDGE,"E2"),sQuery(id+"F0.wireOp",EDGE,"E3.1.0"),sQuery(id+"F0.wireOp",EDGE,"E3.2.0"),sQuery(id+"F0.wireOp",EDGE,"E3.3.0"),sQuery(id+"F0.wireOp",EDGE,"E3.4.0"),sQuery(id+"F0.wireOp",EDGE,"E4.1.0"),sQuery(id+"F0.wireOp",EDGE,"E4.2.0"),sQuery(id+"F0.wireOp",EDGE,"E4.3.0"),sQuery(id+"F0.wireOp",EDGE,"E4.4.0"),subQ0,sQuery(id+"F0.wireOp",EDGE,"E6"),sQuery(id+"F0.wireOp",EDGE,"E7.1.0"),sQuery(id+"F0.wireOp",EDGE,"E7.1.1"),sQuery(id+"F0.wireOp",EDGE,"E7.2.0"),sQuery(id+"F0.wireOp",EDGE,"E7.2.1"),sQuery(id+"F0.wireOp",EDGE,"E7.3.0"),sQuery(id+"F0.wireOp",EDGE,"E7.3.1"),sQuery(id+"F0.wireOp",EDGE,"E7.4.0"),sQuery(id+"F0.wireOp",EDGE,"E7.4.1"),sQuery(id+"F0.wireOp",EDGE,"E8.trimOffspring"),sQuery(id+"F0.wireOp",EDGE,"E9.trimOffspring"),sQuery(id+"F0.wireOp",EDGE,"E10.trimOffspring"),sQuery(id+"F0.wireOp",EDGE,"E11.trimOffspring"),sQuery(id+"F0.wireOp",EDGE,"E12.trimOffspring"),sQuery(id+"F0.wireOp",EDGE,"E13.trimOffspring"),sQuery(id+"F0.wireOp",EDGE,"E14.trimOffspring"),sQuery(id+"F0.wireOp",EDGE,"E15.trimOffspring"),sQuery(id+"F0.wireOp",EDGE,"E16.trimOffspring")])],"isStart":false})]});}
            var Q8;
            {var subQ0=sQuery(id+"F0.wireOp",EDGE,"E3.4.0");Q8=makeQuery(id+"F2.opChamfer","BLEND_EDGE",EDGE,{"blendedFrom":[makeQuery(id+"F1.opExtrude","CAP_EDGE",EDGE,{"disambiguationData":[OSD([subQ0])],"isStart":false}),makeQuery(id+"F1.opExtrude","CAP_FACE",FACE,{"disambiguationData":[OSD([sQuery(id+"F0.wireOp",EDGE,"E0"),sQuery(id+"F0.wireOp",EDGE,"E1"),sQuery(id+"F0.wireOp",EDGE,"E2"),sQuery(id+"F0.wireOp",EDGE,"E3.1.0"),sQuery(id+"F0.wireOp",EDGE,"E3.2.0"),sQuery(id+"F0.wireOp",EDGE,"E3.3.0"),subQ0,sQuery(id+"F0.wireOp",EDGE,"E4.1.0"),sQuery(id+"F0.wireOp",EDGE,"E4.2.0"),sQuery(id+"F0.wireOp",EDGE,"E4.3.0"),sQuery(id+"F0.wireOp",EDGE,"E4.4.0"),sQuery(id+"F0.wireOp",EDGE,"E5"),sQuery(id+"F0.wireOp",EDGE,"E6"),sQuery(id+"F0.wireOp",EDGE,"E7.1.0"),sQuery(id+"F0.wireOp",EDGE,"E7.1.1"),sQuery(id+"F0.wireOp",EDGE,"E7.2.0"),sQuery(id+"F0.wireOp",EDGE,"E7.2.1"),sQuery(id+"F0.wireOp",EDGE,"E7.3.0"),sQuery(id+"F0.wireOp",EDGE,"E7.3.1"),sQuery(id+"F0.wireOp",EDGE,"E7.4.0"),sQuery(id+"F0.wireOp",EDGE,"E7.4.1"),sQuery(id+"F0.wireOp",EDGE,"E8.trimOffspring"),sQuery(id+"F0.wireOp",EDGE,"E9.trimOffspring"),sQuery(id+"F0.wireOp",EDGE,"E10.trimOffspring"),sQuery(id+"F0.wireOp",EDGE,"E11.trimOffspring"),sQuery(id+"F0.wireOp",EDGE,"E12.trimOffspring"),sQuery(id+"F0.wireOp",EDGE,"E13.trimOffspring"),sQuery(id+"F0.wireOp",EDGE,"E14.trimOffspring"),sQuery(id+"F0.wireOp",EDGE,"E15.trimOffspring"),sQuery(id+"F0.wireOp",EDGE,"E16.trimOffspring")])],"isStart":false})],"blendedInto":[makeQuery(id+"F1.opExtrude","CAP_FACE",FACE,{"disambiguationData":[OSD([sQuery(id+"F0.wireOp",EDGE,"E0"),sQuery(id+"F0.wireOp",EDGE,"E1"),sQuery(id+"F0.wireOp",EDGE,"E2"),sQuery(id+"F0.wireOp",EDGE,"E3.1.0"),sQuery(id+"F0.wireOp",EDGE,"E3.2.0"),sQuery(id+"F0.wireOp",EDGE,"E3.3.0"),subQ0,sQuery(id+"F0.wireOp",EDGE,"E4.1.0"),sQuery(id+"F0.wireOp",EDGE,"E4.2.0"),sQuery(id+"F0.wireOp",EDGE,"E4.3.0"),sQuery(id+"F0.wireOp",EDGE,"E4.4.0"),sQuery(id+"F0.wireOp",EDGE,"E5"),sQuery(id+"F0.wireOp",EDGE,"E6"),sQuery(id+"F0.wireOp",EDGE,"E7.1.0"),sQuery(id+"F0.wireOp",EDGE,"E7.1.1"),sQuery(id+"F0.wireOp",EDGE,"E7.2.0"),sQuery(id+"F0.wireOp",EDGE,"E7.2.1"),sQuery(id+"F0.wireOp",EDGE,"E7.3.0"),sQuery(id+"F0.wireOp",EDGE,"E7.3.1"),sQuery(id+"F0.wireOp",EDGE,"E7.4.0"),sQuery(id+"F0.wireOp",EDGE,"E7.4.1"),sQuery(id+"F0.wireOp",EDGE,"E8.trimOffspring"),sQuery(id+"F0.wireOp",EDGE,"E9.trimOffspring"),sQuery(id+"F0.wireOp",EDGE,"E10.trimOffspring"),sQuery(id+"F0.wireOp",EDGE,"E11.trimOffspring"),sQuery(id+"F0.wireOp",EDGE,"E12.trimOffspring"),sQuery(id+"F0.wireOp",EDGE,"E13.trimOffspring"),sQuery(id+"F0.wireOp",EDGE,"E14.trimOffspring"),sQuery(id+"F0.wireOp",EDGE,"E15.trimOffspring"),sQuery(id+"F0.wireOp",EDGE,"E16.trimOffspring")])],"isStart":false})]});}
            var Q9;
            {var subQ0=sQuery(id+"F0.wireOp",EDGE,"E7.4.0");Q9=makeQuery(id+"F2.opChamfer","BLEND_EDGE",EDGE,{"blendedFrom":[makeQuery(id+"F1.opExtrude","CAP_EDGE",EDGE,{"disambiguationData":[OSD([subQ0])],"isStart":false}),makeQuery(id+"F1.opExtrude","CAP_FACE",FACE,{"disambiguationData":[OSD([sQuery(id+"F0.wireOp",EDGE,"E0"),sQuery(id+"F0.wireOp",EDGE,"E1"),sQuery(id+"F0.wireOp",EDGE,"E2"),sQuery(id+"F0.wireOp",EDGE,"E3.1.0"),sQuery(id+"F0.wireOp",EDGE,"E3.2.0"),sQuery(id+"F0.wireOp",EDGE,"E3.3.0"),sQuery(id+"F0.wireOp",EDGE,"E3.4.0"),sQuery(id+"F0.wireOp",EDGE,"E4.1.0"),sQuery(id+"F0.wireOp",EDGE,"E4.2.0"),sQuery(id+"F0.wireOp",EDGE,"E4.3.0"),sQuery(id+"F0.wireOp",EDGE,"E4.4.0"),sQuery(id+"F0.wireOp",EDGE,"E5"),sQuery(id+"F0.wireOp",EDGE,"E6"),sQuery(id+"F0.wireOp",EDGE,"E7.1.0"),sQuery(id+"F0.wireOp",EDGE,"E7.1.1"),sQuery(id+"F0.wireOp",EDGE,"E7.2.0"),sQuery(id+"F0.wireOp",EDGE,"E7.2.1"),sQuery(id+"F0.wireOp",EDGE,"E7.3.0"),sQuery(id+"F0.wireOp",EDGE,"E7.3.1"),subQ0,sQuery(id+"F0.wireOp",EDGE,"E7.4.1"),sQuery(id+"F0.wireOp",EDGE,"E8.trimOffspring"),sQuery(id+"F0.wireOp",EDGE,"E9.trimOffspring"),sQuery(id+"F0.wireOp",EDGE,"E10.trimOffspring"),sQuery(id+"F0.wireOp",EDGE,"E11.trimOffspring"),sQuery(id+"F0.wireOp",EDGE,"E12.trimOffspring"),sQuery(id+"F0.wireOp",EDGE,"E13.trimOffspring"),sQuery(id+"F0.wireOp",EDGE,"E14.trimOffspring"),sQuery(id+"F0.wireOp",EDGE,"E15.trimOffspring"),sQuery(id+"F0.wireOp",EDGE,"E16.trimOffspring")])],"isStart":false})],"blendedInto":[makeQuery(id+"F1.opExtrude","CAP_FACE",FACE,{"disambiguationData":[OSD([sQuery(id+"F0.wireOp",EDGE,"E0"),sQuery(id+"F0.wireOp",EDGE,"E1"),sQuery(id+"F0.wireOp",EDGE,"E2"),sQuery(id+"F0.wireOp",EDGE,"E3.1.0"),sQuery(id+"F0.wireOp",EDGE,"E3.2.0"),sQuery(id+"F0.wireOp",EDGE,"E3.3.0"),sQuery(id+"F0.wireOp",EDGE,"E3.4.0"),sQuery(id+"F0.wireOp",EDGE,"E4.1.0"),sQuery(id+"F0.wireOp",EDGE,"E4.2.0"),sQuery(id+"F0.wireOp",EDGE,"E4.3.0"),sQuery(id+"F0.wireOp",EDGE,"E4.4.0"),sQuery(id+"F0.wireOp",EDGE,"E5"),sQuery(id+"F0.wireOp",EDGE,"E6"),sQuery(id+"F0.wireOp",EDGE,"E7.1.0"),sQuery(id+"F0.wireOp",EDGE,"E7.1.1"),sQuery(id+"F0.wireOp",EDGE,"E7.2.0"),sQuery(id+"F0.wireOp",EDGE,"E7.2.1"),sQuery(id+"F0.wireOp",EDGE,"E7.3.0"),sQuery(id+"F0.wireOp",EDGE,"E7.3.1"),subQ0,sQuery(id+"F0.wireOp",EDGE,"E7.4.1"),sQuery(id+"F0.wireOp",EDGE,"E8.trimOffspring"),sQuery(id+"F0.wireOp",EDGE,"E9.trimOffspring"),sQuery(id+"F0.wireOp",EDGE,"E10.trimOffspring"),sQuery(id+"F0.wireOp",EDGE,"E11.trimOffspring"),sQuery(id+"F0.wireOp",EDGE,"E12.trimOffspring"),sQuery(id+"F0.wireOp",EDGE,"E13.trimOffspring"),sQuery(id+"F0.wireOp",EDGE,"E14.trimOffspring"),sQuery(id+"F0.wireOp",EDGE,"E15.trimOffspring"),sQuery(id+"F0.wireOp",EDGE,"E16.trimOffspring")])],"isStart":false})]});}
            var Q10;
            {var subQ0=sQuery(id+"F0.wireOp",EDGE,"E7.4.1");Q10=makeQuery(id+"F2.opChamfer","BLEND_EDGE",EDGE,{"blendedFrom":[makeQuery(id+"F1.opExtrude","CAP_EDGE",EDGE,{"disambiguationData":[OSD([subQ0])],"isStart":false}),makeQuery(id+"F1.opExtrude","CAP_FACE",FACE,{"disambiguationData":[OSD([sQuery(id+"F0.wireOp",EDGE,"E0"),sQuery(id+"F0.wireOp",EDGE,"E1"),sQuery(id+"F0.wireOp",EDGE,"E2"),sQuery(id+"F0.wireOp",EDGE,"E3.1.0"),sQuery(id+"F0.wireOp",EDGE,"E3.2.0"),sQuery(id+"F0.wireOp",EDGE,"E3.3.0"),sQuery(id+"F0.wireOp",EDGE,"E3.4.0"),sQuery(id+"F0.wireOp",EDGE,"E4.1.0"),sQuery(id+"F0.wireOp",EDGE,"E4.2.0"),sQuery(id+"F0.wireOp",EDGE,"E4.3.0"),sQuery(id+"F0.wireOp",EDGE,"E4.4.0"),sQuery(id+"F0.wireOp",EDGE,"E5"),sQuery(id+"F0.wireOp",EDGE,"E6"),sQuery(id+"F0.wireOp",EDGE,"E7.1.0"),sQuery(id+"F0.wireOp",EDGE,"E7.1.1"),sQuery(id+"F0.wireOp",EDGE,"E7.2.0"),sQuery(id+"F0.wireOp",EDGE,"E7.2.1"),sQuery(id+"F0.wireOp",EDGE,"E7.3.0"),sQuery(id+"F0.wireOp",EDGE,"E7.3.1"),sQuery(id+"F0.wireOp",EDGE,"E7.4.0"),subQ0,sQuery(id+"F0.wireOp",EDGE,"E8.trimOffspring"),sQuery(id+"F0.wireOp",EDGE,"E9.trimOffspring"),sQuery(id+"F0.wireOp",EDGE,"E10.trimOffspring"),sQuery(id+"F0.wireOp",EDGE,"E11.trimOffspring"),sQuery(id+"F0.wireOp",EDGE,"E12.trimOffspring"),sQuery(id+"F0.wireOp",EDGE,"E13.trimOffspring"),sQuery(id+"F0.wireOp",EDGE,"E14.trimOffspring"),sQuery(id+"F0.wireOp",EDGE,"E15.trimOffspring"),sQuery(id+"F0.wireOp",EDGE,"E16.trimOffspring")])],"isStart":false})],"blendedInto":[makeQuery(id+"F1.opExtrude","CAP_FACE",FACE,{"disambiguationData":[OSD([sQuery(id+"F0.wireOp",EDGE,"E0"),sQuery(id+"F0.wireOp",EDGE,"E1"),sQuery(id+"F0.wireOp",EDGE,"E2"),sQuery(id+"F0.wireOp",EDGE,"E3.1.0"),sQuery(id+"F0.wireOp",EDGE,"E3.2.0"),sQuery(id+"F0.wireOp",EDGE,"E3.3.0"),sQuery(id+"F0.wireOp",EDGE,"E3.4.0"),sQuery(id+"F0.wireOp",EDGE,"E4.1.0"),sQuery(id+"F0.wireOp",EDGE,"E4.2.0"),sQuery(id+"F0.wireOp",EDGE,"E4.3.0"),sQuery(id+"F0.wireOp",EDGE,"E4.4.0"),sQuery(id+"F0.wireOp",EDGE,"E5"),sQuery(id+"F0.wireOp",EDGE,"E6"),sQuery(id+"F0.wireOp",EDGE,"E7.1.0"),sQuery(id+"F0.wireOp",EDGE,"E7.1.1"),sQuery(id+"F0.wireOp",EDGE,"E7.2.0"),sQuery(id+"F0.wireOp",EDGE,"E7.2.1"),sQuery(id+"F0.wireOp",EDGE,"E7.3.0"),sQuery(id+"F0.wireOp",EDGE,"E7.3.1"),sQuery(id+"F0.wireOp",EDGE,"E7.4.0"),subQ0,sQuery(id+"F0.wireOp",EDGE,"E8.trimOffspring"),sQuery(id+"F0.wireOp",EDGE,"E9.trimOffspring"),sQuery(id+"F0.wireOp",EDGE,"E10.trimOffspring"),sQuery(id+"F0.wireOp",EDGE,"E11.trimOffspring"),sQuery(id+"F0.wireOp",EDGE,"E12.trimOffspring"),sQuery(id+"F0.wireOp",EDGE,"E13.trimOffspring"),sQuery(id+"F0.wireOp",EDGE,"E14.trimOffspring"),sQuery(id+"F0.wireOp",EDGE,"E15.trimOffspring"),sQuery(id+"F0.wireOp",EDGE,"E16.trimOffspring")])],"isStart":false})]});}
            var Q11;
            {var subQ0=sQuery(id+"F0.wireOp",EDGE,"E4.4.0");Q11=makeQuery(id+"F2.opChamfer","BLEND_EDGE",EDGE,{"blendedFrom":[makeQuery(id+"F1.opExtrude","CAP_EDGE",EDGE,{"disambiguationData":[OSD([subQ0])],"isStart":false}),makeQuery(id+"F1.opExtrude","CAP_FACE",FACE,{"disambiguationData":[OSD([sQuery(id+"F0.wireOp",EDGE,"E0"),sQuery(id+"F0.wireOp",EDGE,"E1"),sQuery(id+"F0.wireOp",EDGE,"E2"),sQuery(id+"F0.wireOp",EDGE,"E3.1.0"),sQuery(id+"F0.wireOp",EDGE,"E3.2.0"),sQuery(id+"F0.wireOp",EDGE,"E3.3.0"),sQuery(id+"F0.wireOp",EDGE,"E3.4.0"),sQuery(id+"F0.wireOp",EDGE,"E4.1.0"),sQuery(id+"F0.wireOp",EDGE,"E4.2.0"),sQuery(id+"F0.wireOp",EDGE,"E4.3.0"),subQ0,sQuery(id+"F0.wireOp",EDGE,"E5"),sQuery(id+"F0.wireOp",EDGE,"E6"),sQuery(id+"F0.wireOp",EDGE,"E7.1.0"),sQuery(id+"F0.wireOp",EDGE,"E7.1.1"),sQuery(id+"F0.wireOp",EDGE,"E7.2.0"),sQuery(id+"F0.wireOp",EDGE,"E7.2.1"),sQuery(id+"F0.wireOp",EDGE,"E7.3.0"),sQuery(id+"F0.wireOp",EDGE,"E7.3.1"),sQuery(id+"F0.wireOp",EDGE,"E7.4.0"),sQuery(id+"F0.wireOp",EDGE,"E7.4.1"),sQuery(id+"F0.wireOp",EDGE,"E8.trimOffspring"),sQuery(id+"F0.wireOp",EDGE,"E9.trimOffspring"),sQuery(id+"F0.wireOp",EDGE,"E10.trimOffspring"),sQuery(id+"F0.wireOp",EDGE,"E11.trimOffspring"),sQuery(id+"F0.wireOp",EDGE,"E12.trimOffspring"),sQuery(id+"F0.wireOp",EDGE,"E13.trimOffspring"),sQuery(id+"F0.wireOp",EDGE,"E14.trimOffspring"),sQuery(id+"F0.wireOp",EDGE,"E15.trimOffspring"),sQuery(id+"F0.wireOp",EDGE,"E16.trimOffspring")])],"isStart":false})],"blendedInto":[makeQuery(id+"F1.opExtrude","CAP_FACE",FACE,{"disambiguationData":[OSD([sQuery(id+"F0.wireOp",EDGE,"E0"),sQuery(id+"F0.wireOp",EDGE,"E1"),sQuery(id+"F0.wireOp",EDGE,"E2"),sQuery(id+"F0.wireOp",EDGE,"E3.1.0"),sQuery(id+"F0.wireOp",EDGE,"E3.2.0"),sQuery(id+"F0.wireOp",EDGE,"E3.3.0"),sQuery(id+"F0.wireOp",EDGE,"E3.4.0"),sQuery(id+"F0.wireOp",EDGE,"E4.1.0"),sQuery(id+"F0.wireOp",EDGE,"E4.2.0"),sQuery(id+"F0.wireOp",EDGE,"E4.3.0"),subQ0,sQuery(id+"F0.wireOp",EDGE,"E5"),sQuery(id+"F0.wireOp",EDGE,"E6"),sQuery(id+"F0.wireOp",EDGE,"E7.1.0"),sQuery(id+"F0.wireOp",EDGE,"E7.1.1"),sQuery(id+"F0.wireOp",EDGE,"E7.2.0"),sQuery(id+"F0.wireOp",EDGE,"E7.2.1"),sQuery(id+"F0.wireOp",EDGE,"E7.3.0"),sQuery(id+"F0.wireOp",EDGE,"E7.3.1"),sQuery(id+"F0.wireOp",EDGE,"E7.4.0"),sQuery(id+"F0.wireOp",EDGE,"E7.4.1"),sQuery(id+"F0.wireOp",EDGE,"E8.trimOffspring"),sQuery(id+"F0.wireOp",EDGE,"E9.trimOffspring"),sQuery(id+"F0.wireOp",EDGE,"E10.trimOffspring"),sQuery(id+"F0.wireOp",EDGE,"E11.trimOffspring"),sQuery(id+"F0.wireOp",EDGE,"E12.trimOffspring"),sQuery(id+"F0.wireOp",EDGE,"E13.trimOffspring"),sQuery(id+"F0.wireOp",EDGE,"E14.trimOffspring"),sQuery(id+"F0.wireOp",EDGE,"E15.trimOffspring"),sQuery(id+"F0.wireOp",EDGE,"E16.trimOffspring")])],"isStart":false})]});}
            var Q12;
            {var subQ0=sQuery(id+"F0.wireOp",EDGE,"E3.3.0");Q12=makeQuery(id+"F2.opChamfer","BLEND_EDGE",EDGE,{"blendedFrom":[makeQuery(id+"F1.opExtrude","CAP_EDGE",EDGE,{"disambiguationData":[OSD([subQ0])],"isStart":false}),makeQuery(id+"F1.opExtrude","CAP_FACE",FACE,{"disambiguationData":[OSD([sQuery(id+"F0.wireOp",EDGE,"E0"),sQuery(id+"F0.wireOp",EDGE,"E1"),sQuery(id+"F0.wireOp",EDGE,"E2"),sQuery(id+"F0.wireOp",EDGE,"E3.1.0"),sQuery(id+"F0.wireOp",EDGE,"E3.2.0"),subQ0,sQuery(id+"F0.wireOp",EDGE,"E3.4.0"),sQuery(id+"F0.wireOp",EDGE,"E4.1.0"),sQuery(id+"F0.wireOp",EDGE,"E4.2.0"),sQuery(id+"F0.wireOp",EDGE,"E4.3.0"),sQuery(id+"F0.wireOp",EDGE,"E4.4.0"),sQuery(id+"F0.wireOp",EDGE,"E5"),sQuery(id+"F0.wireOp",EDGE,"E6"),sQuery(id+"F0.wireOp",EDGE,"E7.1.0"),sQuery(id+"F0.wireOp",EDGE,"E7.1.1"),sQuery(id+"F0.wireOp",EDGE,"E7.2.0"),sQuery(id+"F0.wireOp",EDGE,"E7.2.1"),sQuery(id+"F0.wireOp",EDGE,"E7.3.0"),sQuery(id+"F0.wireOp",EDGE,"E7.3.1"),sQuery(id+"F0.wireOp",EDGE,"E7.4.0"),sQuery(id+"F0.wireOp",EDGE,"E7.4.1"),sQuery(id+"F0.wireOp",EDGE,"E8.trimOffspring"),sQuery(id+"F0.wireOp",EDGE,"E9.trimOffspring"),sQuery(id+"F0.wireOp",EDGE,"E10.trimOffspring"),sQuery(id+"F0.wireOp",EDGE,"E11.trimOffspring"),sQuery(id+"F0.wireOp",EDGE,"E12.trimOffspring"),sQuery(id+"F0.wireOp",EDGE,"E13.trimOffspring"),sQuery(id+"F0.wireOp",EDGE,"E14.trimOffspring"),sQuery(id+"F0.wireOp",EDGE,"E15.trimOffspring"),sQuery(id+"F0.wireOp",EDGE,"E16.trimOffspring")])],"isStart":false})],"blendedInto":[makeQuery(id+"F1.opExtrude","CAP_FACE",FACE,{"disambiguationData":[OSD([sQuery(id+"F0.wireOp",EDGE,"E0"),sQuery(id+"F0.wireOp",EDGE,"E1"),sQuery(id+"F0.wireOp",EDGE,"E2"),sQuery(id+"F0.wireOp",EDGE,"E3.1.0"),sQuery(id+"F0.wireOp",EDGE,"E3.2.0"),subQ0,sQuery(id+"F0.wireOp",EDGE,"E3.4.0"),sQuery(id+"F0.wireOp",EDGE,"E4.1.0"),sQuery(id+"F0.wireOp",EDGE,"E4.2.0"),sQuery(id+"F0.wireOp",EDGE,"E4.3.0"),sQuery(id+"F0.wireOp",EDGE,"E4.4.0"),sQuery(id+"F0.wireOp",EDGE,"E5"),sQuery(id+"F0.wireOp",EDGE,"E6"),sQuery(id+"F0.wireOp",EDGE,"E7.1.0"),sQuery(id+"F0.wireOp",EDGE,"E7.1.1"),sQuery(id+"F0.wireOp",EDGE,"E7.2.0"),sQuery(id+"F0.wireOp",EDGE,"E7.2.1"),sQuery(id+"F0.wireOp",EDGE,"E7.3.0"),sQuery(id+"F0.wireOp",EDGE,"E7.3.1"),sQuery(id+"F0.wireOp",EDGE,"E7.4.0"),sQuery(id+"F0.wireOp",EDGE,"E7.4.1"),sQuery(id+"F0.wireOp",EDGE,"E8.trimOffspring"),sQuery(id+"F0.wireOp",EDGE,"E9.trimOffspring"),sQuery(id+"F0.wireOp",EDGE,"E10.trimOffspring"),sQuery(id+"F0.wireOp",EDGE,"E11.trimOffspring"),sQuery(id+"F0.wireOp",EDGE,"E12.trimOffspring"),sQuery(id+"F0.wireOp",EDGE,"E13.trimOffspring"),sQuery(id+"F0.wireOp",EDGE,"E14.trimOffspring"),sQuery(id+"F0.wireOp",EDGE,"E15.trimOffspring"),sQuery(id+"F0.wireOp",EDGE,"E16.trimOffspring")])],"isStart":false})]});}
            var Q13;
            {var subQ0=sQuery(id+"F0.wireOp",EDGE,"E4.2.0");Q13=makeQuery(id+"F2.opChamfer","BLEND_EDGE",EDGE,{"blendedFrom":[makeQuery(id+"F1.opExtrude","CAP_EDGE",EDGE,{"disambiguationData":[OSD([subQ0])],"isStart":false}),makeQuery(id+"F1.opExtrude","CAP_FACE",FACE,{"disambiguationData":[OSD([sQuery(id+"F0.wireOp",EDGE,"E0"),sQuery(id+"F0.wireOp",EDGE,"E1"),sQuery(id+"F0.wireOp",EDGE,"E2"),sQuery(id+"F0.wireOp",EDGE,"E3.1.0"),sQuery(id+"F0.wireOp",EDGE,"E3.2.0"),sQuery(id+"F0.wireOp",EDGE,"E3.3.0"),sQuery(id+"F0.wireOp",EDGE,"E3.4.0"),sQuery(id+"F0.wireOp",EDGE,"E4.1.0"),subQ0,sQuery(id+"F0.wireOp",EDGE,"E4.3.0"),sQuery(id+"F0.wireOp",EDGE,"E4.4.0"),sQuery(id+"F0.wireOp",EDGE,"E5"),sQuery(id+"F0.wireOp",EDGE,"E6"),sQuery(id+"F0.wireOp",EDGE,"E7.1.0"),sQuery(id+"F0.wireOp",EDGE,"E7.1.1"),sQuery(id+"F0.wireOp",EDGE,"E7.2.0"),sQuery(id+"F0.wireOp",EDGE,"E7.2.1"),sQuery(id+"F0.wireOp",EDGE,"E7.3.0"),sQuery(id+"F0.wireOp",EDGE,"E7.3.1"),sQuery(id+"F0.wireOp",EDGE,"E7.4.0"),sQuery(id+"F0.wireOp",EDGE,"E7.4.1"),sQuery(id+"F0.wireOp",EDGE,"E8.trimOffspring"),sQuery(id+"F0.wireOp",EDGE,"E9.trimOffspring"),sQuery(id+"F0.wireOp",EDGE,"E10.trimOffspring"),sQuery(id+"F0.wireOp",EDGE,"E11.trimOffspring"),sQuery(id+"F0.wireOp",EDGE,"E12.trimOffspring"),sQuery(id+"F0.wireOp",EDGE,"E13.trimOffspring"),sQuery(id+"F0.wireOp",EDGE,"E14.trimOffspring"),sQuery(id+"F0.wireOp",EDGE,"E15.trimOffspring"),sQuery(id+"F0.wireOp",EDGE,"E16.trimOffspring")])],"isStart":false})],"blendedInto":[makeQuery(id+"F1.opExtrude","CAP_FACE",FACE,{"disambiguationData":[OSD([sQuery(id+"F0.wireOp",EDGE,"E0"),sQuery(id+"F0.wireOp",EDGE,"E1"),sQuery(id+"F0.wireOp",EDGE,"E2"),sQuery(id+"F0.wireOp",EDGE,"E3.1.0"),sQuery(id+"F0.wireOp",EDGE,"E3.2.0"),sQuery(id+"F0.wireOp",EDGE,"E3.3.0"),sQuery(id+"F0.wireOp",EDGE,"E3.4.0"),sQuery(id+"F0.wireOp",EDGE,"E4.1.0"),subQ0,sQuery(id+"F0.wireOp",EDGE,"E4.3.0"),sQuery(id+"F0.wireOp",EDGE,"E4.4.0"),sQuery(id+"F0.wireOp",EDGE,"E5"),sQuery(id+"F0.wireOp",EDGE,"E6"),sQuery(id+"F0.wireOp",EDGE,"E7.1.0"),sQuery(id+"F0.wireOp",EDGE,"E7.1.1"),sQuery(id+"F0.wireOp",EDGE,"E7.2.0"),sQuery(id+"F0.wireOp",EDGE,"E7.2.1"),sQuery(id+"F0.wireOp",EDGE,"E7.3.0"),sQuery(id+"F0.wireOp",EDGE,"E7.3.1"),sQuery(id+"F0.wireOp",EDGE,"E7.4.0"),sQuery(id+"F0.wireOp",EDGE,"E7.4.1"),sQuery(id+"F0.wireOp",EDGE,"E8.trimOffspring"),sQuery(id+"F0.wireOp",EDGE,"E9.trimOffspring"),sQuery(id+"F0.wireOp",EDGE,"E10.trimOffspring"),sQuery(id+"F0.wireOp",EDGE,"E11.trimOffspring"),sQuery(id+"F0.wireOp",EDGE,"E12.trimOffspring"),sQuery(id+"F0.wireOp",EDGE,"E13.trimOffspring"),sQuery(id+"F0.wireOp",EDGE,"E14.trimOffspring"),sQuery(id+"F0.wireOp",EDGE,"E15.trimOffspring"),sQuery(id+"F0.wireOp",EDGE,"E16.trimOffspring")])],"isStart":false})]});}
            var Q14;
            {var subQ0=sQuery(id+"F0.wireOp",EDGE,"E7.2.1");Q14=makeQuery(id+"F2.opChamfer","BLEND_EDGE",EDGE,{"blendedFrom":[makeQuery(id+"F1.opExtrude","CAP_EDGE",EDGE,{"disambiguationData":[OSD([subQ0])],"isStart":false}),makeQuery(id+"F1.opExtrude","CAP_FACE",FACE,{"disambiguationData":[OSD([sQuery(id+"F0.wireOp",EDGE,"E0"),sQuery(id+"F0.wireOp",EDGE,"E1"),sQuery(id+"F0.wireOp",EDGE,"E2"),sQuery(id+"F0.wireOp",EDGE,"E3.1.0"),sQuery(id+"F0.wireOp",EDGE,"E3.2.0"),sQuery(id+"F0.wireOp",EDGE,"E3.3.0"),sQuery(id+"F0.wireOp",EDGE,"E3.4.0"),sQuery(id+"F0.wireOp",EDGE,"E4.1.0"),sQuery(id+"F0.wireOp",EDGE,"E4.2.0"),sQuery(id+"F0.wireOp",EDGE,"E4.3.0"),sQuery(id+"F0.wireOp",EDGE,"E4.4.0"),sQuery(id+"F0.wireOp",EDGE,"E5"),sQuery(id+"F0.wireOp",EDGE,"E6"),sQuery(id+"F0.wireOp",EDGE,"E7.1.0"),sQuery(id+"F0.wireOp",EDGE,"E7.1.1"),sQuery(id+"F0.wireOp",EDGE,"E7.2.0"),subQ0,sQuery(id+"F0.wireOp",EDGE,"E7.3.0"),sQuery(id+"F0.wireOp",EDGE,"E7.3.1"),sQuery(id+"F0.wireOp",EDGE,"E7.4.0"),sQuery(id+"F0.wireOp",EDGE,"E7.4.1"),sQuery(id+"F0.wireOp",EDGE,"E8.trimOffspring"),sQuery(id+"F0.wireOp",EDGE,"E9.trimOffspring"),sQuery(id+"F0.wireOp",EDGE,"E10.trimOffspring"),sQuery(id+"F0.wireOp",EDGE,"E11.trimOffspring"),sQuery(id+"F0.wireOp",EDGE,"E12.trimOffspring"),sQuery(id+"F0.wireOp",EDGE,"E13.trimOffspring"),sQuery(id+"F0.wireOp",EDGE,"E14.trimOffspring"),sQuery(id+"F0.wireOp",EDGE,"E15.trimOffspring"),sQuery(id+"F0.wireOp",EDGE,"E16.trimOffspring")])],"isStart":false})],"blendedInto":[makeQuery(id+"F1.opExtrude","CAP_FACE",FACE,{"disambiguationData":[OSD([sQuery(id+"F0.wireOp",EDGE,"E0"),sQuery(id+"F0.wireOp",EDGE,"E1"),sQuery(id+"F0.wireOp",EDGE,"E2"),sQuery(id+"F0.wireOp",EDGE,"E3.1.0"),sQuery(id+"F0.wireOp",EDGE,"E3.2.0"),sQuery(id+"F0.wireOp",EDGE,"E3.3.0"),sQuery(id+"F0.wireOp",EDGE,"E3.4.0"),sQuery(id+"F0.wireOp",EDGE,"E4.1.0"),sQuery(id+"F0.wireOp",EDGE,"E4.2.0"),sQuery(id+"F0.wireOp",EDGE,"E4.3.0"),sQuery(id+"F0.wireOp",EDGE,"E4.4.0"),sQuery(id+"F0.wireOp",EDGE,"E5"),sQuery(id+"F0.wireOp",EDGE,"E6"),sQuery(id+"F0.wireOp",EDGE,"E7.1.0"),sQuery(id+"F0.wireOp",EDGE,"E7.1.1"),sQuery(id+"F0.wireOp",EDGE,"E7.2.0"),subQ0,sQuery(id+"F0.wireOp",EDGE,"E7.3.0"),sQuery(id+"F0.wireOp",EDGE,"E7.3.1"),sQuery(id+"F0.wireOp",EDGE,"E7.4.0"),sQuery(id+"F0.wireOp",EDGE,"E7.4.1"),sQuery(id+"F0.wireOp",EDGE,"E8.trimOffspring"),sQuery(id+"F0.wireOp",EDGE,"E9.trimOffspring"),sQuery(id+"F0.wireOp",EDGE,"E10.trimOffspring"),sQuery(id+"F0.wireOp",EDGE,"E11.trimOffspring"),sQuery(id+"F0.wireOp",EDGE,"E12.trimOffspring"),sQuery(id+"F0.wireOp",EDGE,"E13.trimOffspring"),sQuery(id+"F0.wireOp",EDGE,"E14.trimOffspring"),sQuery(id+"F0.wireOp",EDGE,"E15.trimOffspring"),sQuery(id+"F0.wireOp",EDGE,"E16.trimOffspring")])],"isStart":false})]});}
            var Q15;
            {var subQ0=sQuery(id+"F0.wireOp",EDGE,"E3.2.0");Q15=makeQuery(id+"F2.opChamfer","BLEND_EDGE",EDGE,{"blendedFrom":[makeQuery(id+"F1.opExtrude","CAP_EDGE",EDGE,{"disambiguationData":[OSD([subQ0])],"isStart":false}),makeQuery(id+"F1.opExtrude","CAP_FACE",FACE,{"disambiguationData":[OSD([sQuery(id+"F0.wireOp",EDGE,"E0"),sQuery(id+"F0.wireOp",EDGE,"E1"),sQuery(id+"F0.wireOp",EDGE,"E2"),sQuery(id+"F0.wireOp",EDGE,"E3.1.0"),subQ0,sQuery(id+"F0.wireOp",EDGE,"E3.3.0"),sQuery(id+"F0.wireOp",EDGE,"E3.4.0"),sQuery(id+"F0.wireOp",EDGE,"E4.1.0"),sQuery(id+"F0.wireOp",EDGE,"E4.2.0"),sQuery(id+"F0.wireOp",EDGE,"E4.3.0"),sQuery(id+"F0.wireOp",EDGE,"E4.4.0"),sQuery(id+"F0.wireOp",EDGE,"E5"),sQuery(id+"F0.wireOp",EDGE,"E6"),sQuery(id+"F0.wireOp",EDGE,"E7.1.0"),sQuery(id+"F0.wireOp",EDGE,"E7.1.1"),sQuery(id+"F0.wireOp",EDGE,"E7.2.0"),sQuery(id+"F0.wireOp",EDGE,"E7.2.1"),sQuery(id+"F0.wireOp",EDGE,"E7.3.0"),sQuery(id+"F0.wireOp",EDGE,"E7.3.1"),sQuery(id+"F0.wireOp",EDGE,"E7.4.0"),sQuery(id+"F0.wireOp",EDGE,"E7.4.1"),sQuery(id+"F0.wireOp",EDGE,"E8.trimOffspring"),sQuery(id+"F0.wireOp",EDGE,"E9.trimOffspring"),sQuery(id+"F0.wireOp",EDGE,"E10.trimOffspring"),sQuery(id+"F0.wireOp",EDGE,"E11.trimOffspring"),sQuery(id+"F0.wireOp",EDGE,"E12.trimOffspring"),sQuery(id+"F0.wireOp",EDGE,"E13.trimOffspring"),sQuery(id+"F0.wireOp",EDGE,"E14.trimOffspring"),sQuery(id+"F0.wireOp",EDGE,"E15.trimOffspring"),sQuery(id+"F0.wireOp",EDGE,"E16.trimOffspring")])],"isStart":false})],"blendedInto":[makeQuery(id+"F1.opExtrude","CAP_FACE",FACE,{"disambiguationData":[OSD([sQuery(id+"F0.wireOp",EDGE,"E0"),sQuery(id+"F0.wireOp",EDGE,"E1"),sQuery(id+"F0.wireOp",EDGE,"E2"),sQuery(id+"F0.wireOp",EDGE,"E3.1.0"),subQ0,sQuery(id+"F0.wireOp",EDGE,"E3.3.0"),sQuery(id+"F0.wireOp",EDGE,"E3.4.0"),sQuery(id+"F0.wireOp",EDGE,"E4.1.0"),sQuery(id+"F0.wireOp",EDGE,"E4.2.0"),sQuery(id+"F0.wireOp",EDGE,"E4.3.0"),sQuery(id+"F0.wireOp",EDGE,"E4.4.0"),sQuery(id+"F0.wireOp",EDGE,"E5"),sQuery(id+"F0.wireOp",EDGE,"E6"),sQuery(id+"F0.wireOp",EDGE,"E7.1.0"),sQuery(id+"F0.wireOp",EDGE,"E7.1.1"),sQuery(id+"F0.wireOp",EDGE,"E7.2.0"),sQuery(id+"F0.wireOp",EDGE,"E7.2.1"),sQuery(id+"F0.wireOp",EDGE,"E7.3.0"),sQuery(id+"F0.wireOp",EDGE,"E7.3.1"),sQuery(id+"F0.wireOp",EDGE,"E7.4.0"),sQuery(id+"F0.wireOp",EDGE,"E7.4.1"),sQuery(id+"F0.wireOp",EDGE,"E8.trimOffspring"),sQuery(id+"F0.wireOp",EDGE,"E9.trimOffspring"),sQuery(id+"F0.wireOp",EDGE,"E10.trimOffspring"),sQuery(id+"F0.wireOp",EDGE,"E11.trimOffspring"),sQuery(id+"F0.wireOp",EDGE,"E12.trimOffspring"),sQuery(id+"F0.wireOp",EDGE,"E13.trimOffspring"),sQuery(id+"F0.wireOp",EDGE,"E14.trimOffspring"),sQuery(id+"F0.wireOp",EDGE,"E15.trimOffspring"),sQuery(id+"F0.wireOp",EDGE,"E16.trimOffspring")])],"isStart":false})]});}
            var Q16;
            {var subQ0=sQuery(id+"F0.wireOp",EDGE,"E7.2.0");Q16=makeQuery(id+"F2.opChamfer","BLEND_EDGE",EDGE,{"blendedFrom":[makeQuery(id+"F1.opExtrude","CAP_EDGE",EDGE,{"disambiguationData":[OSD([subQ0])],"isStart":false}),makeQuery(id+"F1.opExtrude","CAP_FACE",FACE,{"disambiguationData":[OSD([sQuery(id+"F0.wireOp",EDGE,"E0"),sQuery(id+"F0.wireOp",EDGE,"E1"),sQuery(id+"F0.wireOp",EDGE,"E2"),sQuery(id+"F0.wireOp",EDGE,"E3.1.0"),sQuery(id+"F0.wireOp",EDGE,"E3.2.0"),sQuery(id+"F0.wireOp",EDGE,"E3.3.0"),sQuery(id+"F0.wireOp",EDGE,"E3.4.0"),sQuery(id+"F0.wireOp",EDGE,"E4.1.0"),sQuery(id+"F0.wireOp",EDGE,"E4.2.0"),sQuery(id+"F0.wireOp",EDGE,"E4.3.0"),sQuery(id+"F0.wireOp",EDGE,"E4.4.0"),sQuery(id+"F0.wireOp",EDGE,"E5"),sQuery(id+"F0.wireOp",EDGE,"E6"),sQuery(id+"F0.wireOp",EDGE,"E7.1.0"),sQuery(id+"F0.wireOp",EDGE,"E7.1.1"),subQ0,sQuery(id+"F0.wireOp",EDGE,"E7.2.1"),sQuery(id+"F0.wireOp",EDGE,"E7.3.0"),sQuery(id+"F0.wireOp",EDGE,"E7.3.1"),sQuery(id+"F0.wireOp",EDGE,"E7.4.0"),sQuery(id+"F0.wireOp",EDGE,"E7.4.1"),sQuery(id+"F0.wireOp",EDGE,"E8.trimOffspring"),sQuery(id+"F0.wireOp",EDGE,"E9.trimOffspring"),sQuery(id+"F0.wireOp",EDGE,"E10.trimOffspring"),sQuery(id+"F0.wireOp",EDGE,"E11.trimOffspring"),sQuery(id+"F0.wireOp",EDGE,"E12.trimOffspring"),sQuery(id+"F0.wireOp",EDGE,"E13.trimOffspring"),sQuery(id+"F0.wireOp",EDGE,"E14.trimOffspring"),sQuery(id+"F0.wireOp",EDGE,"E15.trimOffspring"),sQuery(id+"F0.wireOp",EDGE,"E16.trimOffspring")])],"isStart":false})],"blendedInto":[makeQuery(id+"F1.opExtrude","CAP_FACE",FACE,{"disambiguationData":[OSD([sQuery(id+"F0.wireOp",EDGE,"E0"),sQuery(id+"F0.wireOp",EDGE,"E1"),sQuery(id+"F0.wireOp",EDGE,"E2"),sQuery(id+"F0.wireOp",EDGE,"E3.1.0"),sQuery(id+"F0.wireOp",EDGE,"E3.2.0"),sQuery(id+"F0.wireOp",EDGE,"E3.3.0"),sQuery(id+"F0.wireOp",EDGE,"E3.4.0"),sQuery(id+"F0.wireOp",EDGE,"E4.1.0"),sQuery(id+"F0.wireOp",EDGE,"E4.2.0"),sQuery(id+"F0.wireOp",EDGE,"E4.3.0"),sQuery(id+"F0.wireOp",EDGE,"E4.4.0"),sQuery(id+"F0.wireOp",EDGE,"E5"),sQuery(id+"F0.wireOp",EDGE,"E6"),sQuery(id+"F0.wireOp",EDGE,"E7.1.0"),sQuery(id+"F0.wireOp",EDGE,"E7.1.1"),subQ0,sQuery(id+"F0.wireOp",EDGE,"E7.2.1"),sQuery(id+"F0.wireOp",EDGE,"E7.3.0"),sQuery(id+"F0.wireOp",EDGE,"E7.3.1"),sQuery(id+"F0.wireOp",EDGE,"E7.4.0"),sQuery(id+"F0.wireOp",EDGE,"E7.4.1"),sQuery(id+"F0.wireOp",EDGE,"E8.trimOffspring"),sQuery(id+"F0.wireOp",EDGE,"E9.trimOffspring"),sQuery(id+"F0.wireOp",EDGE,"E10.trimOffspring"),sQuery(id+"F0.wireOp",EDGE,"E11.trimOffspring"),sQuery(id+"F0.wireOp",EDGE,"E12.trimOffspring"),sQuery(id+"F0.wireOp",EDGE,"E13.trimOffspring"),sQuery(id+"F0.wireOp",EDGE,"E14.trimOffspring"),sQuery(id+"F0.wireOp",EDGE,"E15.trimOffspring"),sQuery(id+"F0.wireOp",EDGE,"E16.trimOffspring")])],"isStart":false})]});}
            var Q17;
            {var subQ0=sQuery(id+"F0.wireOp",EDGE,"E4.3.0");Q17=makeQuery(id+"F2.opChamfer","BLEND_EDGE",EDGE,{"blendedFrom":[makeQuery(id+"F1.opExtrude","CAP_EDGE",EDGE,{"disambiguationData":[OSD([subQ0])],"isStart":false}),makeQuery(id+"F1.opExtrude","CAP_FACE",FACE,{"disambiguationData":[OSD([sQuery(id+"F0.wireOp",EDGE,"E0"),sQuery(id+"F0.wireOp",EDGE,"E1"),sQuery(id+"F0.wireOp",EDGE,"E2"),sQuery(id+"F0.wireOp",EDGE,"E3.1.0"),sQuery(id+"F0.wireOp",EDGE,"E3.2.0"),sQuery(id+"F0.wireOp",EDGE,"E3.3.0"),sQuery(id+"F0.wireOp",EDGE,"E3.4.0"),sQuery(id+"F0.wireOp",EDGE,"E4.1.0"),sQuery(id+"F0.wireOp",EDGE,"E4.2.0"),subQ0,sQuery(id+"F0.wireOp",EDGE,"E4.4.0"),sQuery(id+"F0.wireOp",EDGE,"E5"),sQuery(id+"F0.wireOp",EDGE,"E6"),sQuery(id+"F0.wireOp",EDGE,"E7.1.0"),sQuery(id+"F0.wireOp",EDGE,"E7.1.1"),sQuery(id+"F0.wireOp",EDGE,"E7.2.0"),sQuery(id+"F0.wireOp",EDGE,"E7.2.1"),sQuery(id+"F0.wireOp",EDGE,"E7.3.0"),sQuery(id+"F0.wireOp",EDGE,"E7.3.1"),sQuery(id+"F0.wireOp",EDGE,"E7.4.0"),sQuery(id+"F0.wireOp",EDGE,"E7.4.1"),sQuery(id+"F0.wireOp",EDGE,"E8.trimOffspring"),sQuery(id+"F0.wireOp",EDGE,"E9.trimOffspring"),sQuery(id+"F0.wireOp",EDGE,"E10.trimOffspring"),sQuery(id+"F0.wireOp",EDGE,"E11.trimOffspring"),sQuery(id+"F0.wireOp",EDGE,"E12.trimOffspring"),sQuery(id+"F0.wireOp",EDGE,"E13.trimOffspring"),sQuery(id+"F0.wireOp",EDGE,"E14.trimOffspring"),sQuery(id+"F0.wireOp",EDGE,"E15.trimOffspring"),sQuery(id+"F0.wireOp",EDGE,"E16.trimOffspring")])],"isStart":false})],"blendedInto":[makeQuery(id+"F1.opExtrude","CAP_FACE",FACE,{"disambiguationData":[OSD([sQuery(id+"F0.wireOp",EDGE,"E0"),sQuery(id+"F0.wireOp",EDGE,"E1"),sQuery(id+"F0.wireOp",EDGE,"E2"),sQuery(id+"F0.wireOp",EDGE,"E3.1.0"),sQuery(id+"F0.wireOp",EDGE,"E3.2.0"),sQuery(id+"F0.wireOp",EDGE,"E3.3.0"),sQuery(id+"F0.wireOp",EDGE,"E3.4.0"),sQuery(id+"F0.wireOp",EDGE,"E4.1.0"),sQuery(id+"F0.wireOp",EDGE,"E4.2.0"),subQ0,sQuery(id+"F0.wireOp",EDGE,"E4.4.0"),sQuery(id+"F0.wireOp",EDGE,"E5"),sQuery(id+"F0.wireOp",EDGE,"E6"),sQuery(id+"F0.wireOp",EDGE,"E7.1.0"),sQuery(id+"F0.wireOp",EDGE,"E7.1.1"),sQuery(id+"F0.wireOp",EDGE,"E7.2.0"),sQuery(id+"F0.wireOp",EDGE,"E7.2.1"),sQuery(id+"F0.wireOp",EDGE,"E7.3.0"),sQuery(id+"F0.wireOp",EDGE,"E7.3.1"),sQuery(id+"F0.wireOp",EDGE,"E7.4.0"),sQuery(id+"F0.wireOp",EDGE,"E7.4.1"),sQuery(id+"F0.wireOp",EDGE,"E8.trimOffspring"),sQuery(id+"F0.wireOp",EDGE,"E9.trimOffspring"),sQuery(id+"F0.wireOp",EDGE,"E10.trimOffspring"),sQuery(id+"F0.wireOp",EDGE,"E11.trimOffspring"),sQuery(id+"F0.wireOp",EDGE,"E12.trimOffspring"),sQuery(id+"F0.wireOp",EDGE,"E13.trimOffspring"),sQuery(id+"F0.wireOp",EDGE,"E14.trimOffspring"),sQuery(id+"F0.wireOp",EDGE,"E15.trimOffspring"),sQuery(id+"F0.wireOp",EDGE,"E16.trimOffspring")])],"isStart":false})]});}
            var Q18;
            {var subQ0=sQuery(id+"F0.wireOp",EDGE,"E7.3.1");Q18=makeQuery(id+"F2.opChamfer","BLEND_EDGE",EDGE,{"blendedFrom":[makeQuery(id+"F1.opExtrude","CAP_EDGE",EDGE,{"disambiguationData":[OSD([subQ0])],"isStart":false}),makeQuery(id+"F1.opExtrude","CAP_FACE",FACE,{"disambiguationData":[OSD([sQuery(id+"F0.wireOp",EDGE,"E0"),sQuery(id+"F0.wireOp",EDGE,"E1"),sQuery(id+"F0.wireOp",EDGE,"E2"),sQuery(id+"F0.wireOp",EDGE,"E3.1.0"),sQuery(id+"F0.wireOp",EDGE,"E3.2.0"),sQuery(id+"F0.wireOp",EDGE,"E3.3.0"),sQuery(id+"F0.wireOp",EDGE,"E3.4.0"),sQuery(id+"F0.wireOp",EDGE,"E4.1.0"),sQuery(id+"F0.wireOp",EDGE,"E4.2.0"),sQuery(id+"F0.wireOp",EDGE,"E4.3.0"),sQuery(id+"F0.wireOp",EDGE,"E4.4.0"),sQuery(id+"F0.wireOp",EDGE,"E5"),sQuery(id+"F0.wireOp",EDGE,"E6"),sQuery(id+"F0.wireOp",EDGE,"E7.1.0"),sQuery(id+"F0.wireOp",EDGE,"E7.1.1"),sQuery(id+"F0.wireOp",EDGE,"E7.2.0"),sQuery(id+"F0.wireOp",EDGE,"E7.2.1"),sQuery(id+"F0.wireOp",EDGE,"E7.3.0"),subQ0,sQuery(id+"F0.wireOp",EDGE,"E7.4.0"),sQuery(id+"F0.wireOp",EDGE,"E7.4.1"),sQuery(id+"F0.wireOp",EDGE,"E8.trimOffspring"),sQuery(id+"F0.wireOp",EDGE,"E9.trimOffspring"),sQuery(id+"F0.wireOp",EDGE,"E10.trimOffspring"),sQuery(id+"F0.wireOp",EDGE,"E11.trimOffspring"),sQuery(id+"F0.wireOp",EDGE,"E12.trimOffspring"),sQuery(id+"F0.wireOp",EDGE,"E13.trimOffspring"),sQuery(id+"F0.wireOp",EDGE,"E14.trimOffspring"),sQuery(id+"F0.wireOp",EDGE,"E15.trimOffspring"),sQuery(id+"F0.wireOp",EDGE,"E16.trimOffspring")])],"isStart":false})],"blendedInto":[makeQuery(id+"F1.opExtrude","CAP_FACE",FACE,{"disambiguationData":[OSD([sQuery(id+"F0.wireOp",EDGE,"E0"),sQuery(id+"F0.wireOp",EDGE,"E1"),sQuery(id+"F0.wireOp",EDGE,"E2"),sQuery(id+"F0.wireOp",EDGE,"E3.1.0"),sQuery(id+"F0.wireOp",EDGE,"E3.2.0"),sQuery(id+"F0.wireOp",EDGE,"E3.3.0"),sQuery(id+"F0.wireOp",EDGE,"E3.4.0"),sQuery(id+"F0.wireOp",EDGE,"E4.1.0"),sQuery(id+"F0.wireOp",EDGE,"E4.2.0"),sQuery(id+"F0.wireOp",EDGE,"E4.3.0"),sQuery(id+"F0.wireOp",EDGE,"E4.4.0"),sQuery(id+"F0.wireOp",EDGE,"E5"),sQuery(id+"F0.wireOp",EDGE,"E6"),sQuery(id+"F0.wireOp",EDGE,"E7.1.0"),sQuery(id+"F0.wireOp",EDGE,"E7.1.1"),sQuery(id+"F0.wireOp",EDGE,"E7.2.0"),sQuery(id+"F0.wireOp",EDGE,"E7.2.1"),sQuery(id+"F0.wireOp",EDGE,"E7.3.0"),subQ0,sQuery(id+"F0.wireOp",EDGE,"E7.4.0"),sQuery(id+"F0.wireOp",EDGE,"E7.4.1"),sQuery(id+"F0.wireOp",EDGE,"E8.trimOffspring"),sQuery(id+"F0.wireOp",EDGE,"E9.trimOffspring"),sQuery(id+"F0.wireOp",EDGE,"E10.trimOffspring"),sQuery(id+"F0.wireOp",EDGE,"E11.trimOffspring"),sQuery(id+"F0.wireOp",EDGE,"E12.trimOffspring"),sQuery(id+"F0.wireOp",EDGE,"E13.trimOffspring"),sQuery(id+"F0.wireOp",EDGE,"E14.trimOffspring"),sQuery(id+"F0.wireOp",EDGE,"E15.trimOffspring"),sQuery(id+"F0.wireOp",EDGE,"E16.trimOffspring")])],"isStart":false})]});}
            var Q19;
            {var subQ0=sQuery(id+"F0.wireOp",EDGE,"E7.3.0");Q19=makeQuery(id+"F2.opChamfer","BLEND_EDGE",EDGE,{"blendedFrom":[makeQuery(id+"F1.opExtrude","CAP_EDGE",EDGE,{"disambiguationData":[OSD([subQ0])],"isStart":false}),makeQuery(id+"F1.opExtrude","CAP_FACE",FACE,{"disambiguationData":[OSD([sQuery(id+"F0.wireOp",EDGE,"E0"),sQuery(id+"F0.wireOp",EDGE,"E1"),sQuery(id+"F0.wireOp",EDGE,"E2"),sQuery(id+"F0.wireOp",EDGE,"E3.1.0"),sQuery(id+"F0.wireOp",EDGE,"E3.2.0"),sQuery(id+"F0.wireOp",EDGE,"E3.3.0"),sQuery(id+"F0.wireOp",EDGE,"E3.4.0"),sQuery(id+"F0.wireOp",EDGE,"E4.1.0"),sQuery(id+"F0.wireOp",EDGE,"E4.2.0"),sQuery(id+"F0.wireOp",EDGE,"E4.3.0"),sQuery(id+"F0.wireOp",EDGE,"E4.4.0"),sQuery(id+"F0.wireOp",EDGE,"E5"),sQuery(id+"F0.wireOp",EDGE,"E6"),sQuery(id+"F0.wireOp",EDGE,"E7.1.0"),sQuery(id+"F0.wireOp",EDGE,"E7.1.1"),sQuery(id+"F0.wireOp",EDGE,"E7.2.0"),sQuery(id+"F0.wireOp",EDGE,"E7.2.1"),subQ0,sQuery(id+"F0.wireOp",EDGE,"E7.3.1"),sQuery(id+"F0.wireOp",EDGE,"E7.4.0"),sQuery(id+"F0.wireOp",EDGE,"E7.4.1"),sQuery(id+"F0.wireOp",EDGE,"E8.trimOffspring"),sQuery(id+"F0.wireOp",EDGE,"E9.trimOffspring"),sQuery(id+"F0.wireOp",EDGE,"E10.trimOffspring"),sQuery(id+"F0.wireOp",EDGE,"E11.trimOffspring"),sQuery(id+"F0.wireOp",EDGE,"E12.trimOffspring"),sQuery(id+"F0.wireOp",EDGE,"E13.trimOffspring"),sQuery(id+"F0.wireOp",EDGE,"E14.trimOffspring"),sQuery(id+"F0.wireOp",EDGE,"E15.trimOffspring"),sQuery(id+"F0.wireOp",EDGE,"E16.trimOffspring")])],"isStart":false})],"blendedInto":[makeQuery(id+"F1.opExtrude","CAP_FACE",FACE,{"disambiguationData":[OSD([sQuery(id+"F0.wireOp",EDGE,"E0"),sQuery(id+"F0.wireOp",EDGE,"E1"),sQuery(id+"F0.wireOp",EDGE,"E2"),sQuery(id+"F0.wireOp",EDGE,"E3.1.0"),sQuery(id+"F0.wireOp",EDGE,"E3.2.0"),sQuery(id+"F0.wireOp",EDGE,"E3.3.0"),sQuery(id+"F0.wireOp",EDGE,"E3.4.0"),sQuery(id+"F0.wireOp",EDGE,"E4.1.0"),sQuery(id+"F0.wireOp",EDGE,"E4.2.0"),sQuery(id+"F0.wireOp",EDGE,"E4.3.0"),sQuery(id+"F0.wireOp",EDGE,"E4.4.0"),sQuery(id+"F0.wireOp",EDGE,"E5"),sQuery(id+"F0.wireOp",EDGE,"E6"),sQuery(id+"F0.wireOp",EDGE,"E7.1.0"),sQuery(id+"F0.wireOp",EDGE,"E7.1.1"),sQuery(id+"F0.wireOp",EDGE,"E7.2.0"),sQuery(id+"F0.wireOp",EDGE,"E7.2.1"),subQ0,sQuery(id+"F0.wireOp",EDGE,"E7.3.1"),sQuery(id+"F0.wireOp",EDGE,"E7.4.0"),sQuery(id+"F0.wireOp",EDGE,"E7.4.1"),sQuery(id+"F0.wireOp",EDGE,"E8.trimOffspring"),sQuery(id+"F0.wireOp",EDGE,"E9.trimOffspring"),sQuery(id+"F0.wireOp",EDGE,"E10.trimOffspring"),sQuery(id+"F0.wireOp",EDGE,"E11.trimOffspring"),sQuery(id+"F0.wireOp",EDGE,"E12.trimOffspring"),sQuery(id+"F0.wireOp",EDGE,"E13.trimOffspring"),sQuery(id+"F0.wireOp",EDGE,"E14.trimOffspring"),sQuery(id+"F0.wireOp",EDGE,"E15.trimOffspring"),sQuery(id+"F0.wireOp",EDGE,"E16.trimOffspring")])],"isStart":false})]});}
            fillet(context, id + "F5", {"entities" : qUnion([Q0, Q1, Q2, Q3, Q4, Q5, Q6, Q7, Q8, Q9, Q10, Q11, Q12, Q13, Q14, Q15, Q16, Q17, Q18, Q19]), "radius" : 2.5 * mm, "tangentPropagation" : true, "allowEdgeOverflow" : false});
        }
        {
            var Q0;
            Q0=makeQuery(id+"F2.opChamfer","BLEND_EDGE",EDGE,{"blendedFrom":[makeQuery(id+"F1.opExtrude","CAP_EDGE",EDGE,{"disambiguationData":[OSD([sQuery(id+"F0.wireOp",EDGE,"E5")])],"isStart":false}),makeQuery(id+"F1.opExtrude","CAP_EDGE",EDGE,{"disambiguationData":[OSD([sQuery(id+"F0.wireOp",EDGE,"E6")])],"isStart":false})],"blendedInto":[]});
            var Q1;
            Q1=makeQuery(id+"F2.opChamfer","BLEND_EDGE",EDGE,{"blendedFrom":[makeQuery(id+"F1.opExtrude","CAP_EDGE",EDGE,{"disambiguationData":[OSD([sQuery(id+"F0.wireOp",EDGE,"E7.1.0")])],"isStart":false}),makeQuery(id+"F1.opExtrude","CAP_EDGE",EDGE,{"disambiguationData":[OSD([sQuery(id+"F0.wireOp",EDGE,"E7.1.1")])],"isStart":false})],"blendedInto":[]});
            var Q2;
            Q2=makeQuery(id+"F2.opChamfer","BLEND_EDGE",EDGE,{"blendedFrom":[makeQuery(id+"F1.opExtrude","CAP_EDGE",EDGE,{"disambiguationData":[OSD([sQuery(id+"F0.wireOp",EDGE,"E7.4.0")])],"isStart":false}),makeQuery(id+"F1.opExtrude","CAP_EDGE",EDGE,{"disambiguationData":[OSD([sQuery(id+"F0.wireOp",EDGE,"E7.4.1")])],"isStart":false})],"blendedInto":[]});
            var Q3;
            Q3=makeQuery(id+"F2.opChamfer","BLEND_EDGE",EDGE,{"blendedFrom":[makeQuery(id+"F1.opExtrude","CAP_EDGE",EDGE,{"disambiguationData":[OSD([sQuery(id+"F0.wireOp",EDGE,"E7.3.0")])],"isStart":false}),makeQuery(id+"F1.opExtrude","CAP_EDGE",EDGE,{"disambiguationData":[OSD([sQuery(id+"F0.wireOp",EDGE,"E7.3.1")])],"isStart":false})],"blendedInto":[]});
            var Q4;
            Q4=makeQuery(id+"F2.opChamfer","BLEND_EDGE",EDGE,{"blendedFrom":[makeQuery(id+"F1.opExtrude","CAP_EDGE",EDGE,{"disambiguationData":[OSD([sQuery(id+"F0.wireOp",EDGE,"E7.2.0")])],"isStart":false}),makeQuery(id+"F1.opExtrude","CAP_EDGE",EDGE,{"disambiguationData":[OSD([sQuery(id+"F0.wireOp",EDGE,"E7.2.1")])],"isStart":false})],"blendedInto":[]});
            chamfer(context, id + "F6", {"entities" : qUnion([Q0, Q1, Q2, Q3, Q4]), "width" : 0.5 * mm, "tangentPropagation" : true});
        }
        {
            var Q0;
            Q0=makeQuery(id+"F3.opChamfer","BLEND_EDGE",EDGE,{"blendedFrom":[makeQuery(id+"F1.opExtrude","CAP_EDGE",EDGE,{"disambiguationData":[OSD([sQuery(id+"F0.wireOp",EDGE,"E5")])],"isStart":true}),makeQuery(id+"F1.opExtrude","CAP_EDGE",EDGE,{"disambiguationData":[OSD([sQuery(id+"F0.wireOp",EDGE,"E6")])],"isStart":true})],"blendedInto":[]});
            var Q1;
            Q1=makeQuery(id+"F3.opChamfer","BLEND_EDGE",EDGE,{"blendedFrom":[makeQuery(id+"F1.opExtrude","CAP_EDGE",EDGE,{"disambiguationData":[OSD([sQuery(id+"F0.wireOp",EDGE,"E7.1.0")])],"isStart":true}),makeQuery(id+"F1.opExtrude","CAP_EDGE",EDGE,{"disambiguationData":[OSD([sQuery(id+"F0.wireOp",EDGE,"E7.1.1")])],"isStart":true})],"blendedInto":[]});
            var Q2;
            Q2=makeQuery(id+"F3.opChamfer","BLEND_EDGE",EDGE,{"blendedFrom":[makeQuery(id+"F1.opExtrude","CAP_EDGE",EDGE,{"disambiguationData":[OSD([sQuery(id+"F0.wireOp",EDGE,"E7.2.0")])],"isStart":true}),makeQuery(id+"F1.opExtrude","CAP_EDGE",EDGE,{"disambiguationData":[OSD([sQuery(id+"F0.wireOp",EDGE,"E7.2.1")])],"isStart":true})],"blendedInto":[]});
            var Q3;
            Q3=makeQuery(id+"F3.opChamfer","BLEND_EDGE",EDGE,{"blendedFrom":[makeQuery(id+"F1.opExtrude","CAP_EDGE",EDGE,{"disambiguationData":[OSD([sQuery(id+"F0.wireOp",EDGE,"E7.3.0")])],"isStart":true}),makeQuery(id+"F1.opExtrude","CAP_EDGE",EDGE,{"disambiguationData":[OSD([sQuery(id+"F0.wireOp",EDGE,"E7.3.1")])],"isStart":true})],"blendedInto":[]});
            var Q4;
            Q4=makeQuery(id+"F3.opChamfer","BLEND_EDGE",EDGE,{"blendedFrom":[makeQuery(id+"F1.opExtrude","CAP_EDGE",EDGE,{"disambiguationData":[OSD([sQuery(id+"F0.wireOp",EDGE,"E7.4.0")])],"isStart":true}),makeQuery(id+"F1.opExtrude","CAP_EDGE",EDGE,{"disambiguationData":[OSD([sQuery(id+"F0.wireOp",EDGE,"E7.4.1")])],"isStart":true})],"blendedInto":[]});
            chamfer(context, id + "F7", {"entities" : qUnion([Q0, Q1, Q2, Q3, Q4]), "width" : 0.5 * mm, "tangentPropagation" : true});
        }
        {
            var Q0;
            {var subQ0=sQuery(id+"F0.wireOp",EDGE,"E7.3.0");Q0=makeQuery(id+"F3.opChamfer","BLEND_EDGE",EDGE,{"blendedFrom":[makeQuery(id+"F1.opExtrude","CAP_EDGE",EDGE,{"disambiguationData":[OSD([subQ0])],"isStart":true}),makeQuery(id+"F2.opChamfer","BLEND_FACE",FACE,{"disambiguationData":[OSD([subQ0])]})],"blendedInto":[makeQuery(id+"F2.opChamfer","BLEND_FACE",FACE,{"disambiguationData":[OSD([subQ0])]})]});}
            var Q1;
            {var subQ0=sQuery(id+"F0.wireOp",EDGE,"E7.4.0");Q1=makeQuery(id+"F3.opChamfer","BLEND_EDGE",EDGE,{"blendedFrom":[makeQuery(id+"F1.opExtrude","CAP_EDGE",EDGE,{"disambiguationData":[OSD([subQ0])],"isStart":true}),makeQuery(id+"F2.opChamfer","BLEND_FACE",FACE,{"disambiguationData":[OSD([subQ0])]})],"blendedInto":[makeQuery(id+"F2.opChamfer","BLEND_FACE",FACE,{"disambiguationData":[OSD([subQ0])]})]});}
            var Q2;
            {var subQ0=sQuery(id+"F0.wireOp",EDGE,"E6");Q2=makeQuery(id+"F3.opChamfer","BLEND_EDGE",EDGE,{"blendedFrom":[makeQuery(id+"F1.opExtrude","CAP_EDGE",EDGE,{"disambiguationData":[OSD([subQ0])],"isStart":true}),makeQuery(id+"F2.opChamfer","BLEND_FACE",FACE,{"disambiguationData":[OSD([subQ0])]})],"blendedInto":[makeQuery(id+"F2.opChamfer","BLEND_FACE",FACE,{"disambiguationData":[OSD([subQ0])]})]});}
            var Q3;
            {var subQ0=sQuery(id+"F0.wireOp",EDGE,"E7.1.0");Q3=makeQuery(id+"F3.opChamfer","BLEND_EDGE",EDGE,{"blendedFrom":[makeQuery(id+"F1.opExtrude","CAP_EDGE",EDGE,{"disambiguationData":[OSD([subQ0])],"isStart":true}),makeQuery(id+"F2.opChamfer","BLEND_FACE",FACE,{"disambiguationData":[OSD([subQ0])]})],"blendedInto":[makeQuery(id+"F2.opChamfer","BLEND_FACE",FACE,{"disambiguationData":[OSD([subQ0])]})]});}
            var Q4;
            {var subQ0=sQuery(id+"F0.wireOp",EDGE,"E7.2.0");Q4=makeQuery(id+"F3.opChamfer","BLEND_EDGE",EDGE,{"blendedFrom":[makeQuery(id+"F1.opExtrude","CAP_EDGE",EDGE,{"disambiguationData":[OSD([subQ0])],"isStart":true}),makeQuery(id+"F2.opChamfer","BLEND_FACE",FACE,{"disambiguationData":[OSD([subQ0])]})],"blendedInto":[makeQuery(id+"F2.opChamfer","BLEND_FACE",FACE,{"disambiguationData":[OSD([subQ0])]})]});}
            chamfer(context, id + "F8", {"entities" : qUnion([Q0, Q1, Q2, Q3, Q4]), "width" : 0.1 * mm, "tangentPropagation" : true});
        }
        {
            var Q0;
            Q0=makeQuery(id+"F3.opChamfer","BLEND_EDGE",EDGE,{"blendedFrom":[makeQuery(id+"F1.opExtrude","CAP_EDGE",EDGE,{"disambiguationData":[OSD([sQuery(id+"F0.wireOp",EDGE,"E3.2.0")])],"isStart":true}),makeQuery(id+"F1.opExtrude","CAP_EDGE",EDGE,{"disambiguationData":[OSD([sQuery(id+"F0.wireOp",EDGE,"E7.2.0")])],"isStart":true})],"blendedInto":[]});
            var Q1;
            Q1=makeQuery(id+"F3.opChamfer","BLEND_EDGE",EDGE,{"blendedFrom":[makeQuery(id+"F1.opExtrude","CAP_EDGE",EDGE,{"disambiguationData":[OSD([sQuery(id+"F0.wireOp",EDGE,"E3.3.0")])],"isStart":true}),makeQuery(id+"F1.opExtrude","CAP_EDGE",EDGE,{"disambiguationData":[OSD([sQuery(id+"F0.wireOp",EDGE,"E7.3.0")])],"isStart":true})],"blendedInto":[]});
            var Q2;
            Q2=makeQuery(id+"F3.opChamfer","BLEND_EDGE",EDGE,{"blendedFrom":[makeQuery(id+"F1.opExtrude","CAP_EDGE",EDGE,{"disambiguationData":[OSD([sQuery(id+"F0.wireOp",EDGE,"E3.4.0")])],"isStart":true}),makeQuery(id+"F1.opExtrude","CAP_EDGE",EDGE,{"disambiguationData":[OSD([sQuery(id+"F0.wireOp",EDGE,"E7.4.0")])],"isStart":true})],"blendedInto":[]});
            var Q3;
            Q3=makeQuery(id+"F3.opChamfer","BLEND_EDGE",EDGE,{"blendedFrom":[makeQuery(id+"F1.opExtrude","CAP_EDGE",EDGE,{"disambiguationData":[OSD([sQuery(id+"F0.wireOp",EDGE,"E1")])],"isStart":true}),makeQuery(id+"F1.opExtrude","CAP_EDGE",EDGE,{"disambiguationData":[OSD([sQuery(id+"F0.wireOp",EDGE,"E6")])],"isStart":true})],"blendedInto":[]});
            var Q4;
            Q4=makeQuery(id+"F3.opChamfer","BLEND_EDGE",EDGE,{"blendedFrom":[makeQuery(id+"F1.opExtrude","CAP_EDGE",EDGE,{"disambiguationData":[OSD([sQuery(id+"F0.wireOp",EDGE,"E3.1.0")])],"isStart":true}),makeQuery(id+"F1.opExtrude","CAP_EDGE",EDGE,{"disambiguationData":[OSD([sQuery(id+"F0.wireOp",EDGE,"E7.1.0")])],"isStart":true})],"blendedInto":[]});
            var Q5;
            Q5=makeQuery(id+"F3.opChamfer","BLEND_EDGE",EDGE,{"blendedFrom":[makeQuery(id+"F1.opExtrude","CAP_EDGE",EDGE,{"disambiguationData":[OSD([sQuery(id+"F0.wireOp",EDGE,"E3.3.0")])],"isStart":true}),makeQuery(id+"F1.opExtrude","CAP_EDGE",EDGE,{"disambiguationData":[OSD([sQuery(id+"F0.wireOp",EDGE,"E4.4.0")])],"isStart":true})],"blendedInto":[]});
            var Q6;
            Q6=makeQuery(id+"F3.opChamfer","BLEND_EDGE",EDGE,{"blendedFrom":[makeQuery(id+"F1.opExtrude","CAP_EDGE",EDGE,{"disambiguationData":[OSD([sQuery(id+"F0.wireOp",EDGE,"E3.2.0")])],"isStart":true}),makeQuery(id+"F1.opExtrude","CAP_EDGE",EDGE,{"disambiguationData":[OSD([sQuery(id+"F0.wireOp",EDGE,"E4.3.0")])],"isStart":true})],"blendedInto":[]});
            var Q7;
            Q7=makeQuery(id+"F3.opChamfer","BLEND_EDGE",EDGE,{"blendedFrom":[makeQuery(id+"F1.opExtrude","CAP_EDGE",EDGE,{"disambiguationData":[OSD([sQuery(id+"F0.wireOp",EDGE,"E3.1.0")])],"isStart":true}),makeQuery(id+"F1.opExtrude","CAP_EDGE",EDGE,{"disambiguationData":[OSD([sQuery(id+"F0.wireOp",EDGE,"E4.2.0")])],"isStart":true})],"blendedInto":[]});
            var Q8;
            Q8=makeQuery(id+"F3.opChamfer","BLEND_EDGE",EDGE,{"blendedFrom":[makeQuery(id+"F1.opExtrude","CAP_EDGE",EDGE,{"disambiguationData":[OSD([sQuery(id+"F0.wireOp",EDGE,"E2")])],"isStart":true}),makeQuery(id+"F1.opExtrude","CAP_EDGE",EDGE,{"disambiguationData":[OSD([sQuery(id+"F0.wireOp",EDGE,"E3.4.0")])],"isStart":true})],"blendedInto":[]});
            var Q9;
            Q9=makeQuery(id+"F3.opChamfer","BLEND_EDGE",EDGE,{"blendedFrom":[makeQuery(id+"F1.opExtrude","CAP_EDGE",EDGE,{"disambiguationData":[OSD([sQuery(id+"F0.wireOp",EDGE,"E1")])],"isStart":true}),makeQuery(id+"F1.opExtrude","CAP_EDGE",EDGE,{"disambiguationData":[OSD([sQuery(id+"F0.wireOp",EDGE,"E4.1.0")])],"isStart":true})],"blendedInto":[]});
            chamfer(context, id + "F9", {"entities" : qUnion([Q0, Q1, Q2, Q3, Q4, Q5, Q6, Q7, Q8, Q9]), "width" : 0.5 * mm, "tangentPropagation" : true});
        }
        {
            var Q0;
            {var subQ0=sQuery(id+"F0.wireOp",EDGE,"E7.1.1");Q0=makeQuery(id+"F3.opChamfer","BLEND_EDGE",EDGE,{"blendedFrom":[makeQuery(id+"F1.opExtrude","CAP_EDGE",EDGE,{"disambiguationData":[OSD([subQ0])],"isStart":true}),makeQuery(id+"F2.opChamfer","BLEND_FACE",FACE,{"disambiguationData":[OSD([subQ0])]})],"blendedInto":[makeQuery(id+"F2.opChamfer","BLEND_FACE",FACE,{"disambiguationData":[OSD([subQ0])]})]});}
            var Q1;
            {var subQ0=sQuery(id+"F0.wireOp",EDGE,"E4.1.0");Q1=makeQuery(id+"F3.opChamfer","BLEND_EDGE",EDGE,{"blendedFrom":[makeQuery(id+"F1.opExtrude","CAP_EDGE",EDGE,{"disambiguationData":[OSD([subQ0])],"isStart":true}),makeQuery(id+"F2.opChamfer","BLEND_FACE",FACE,{"disambiguationData":[OSD([subQ0])]})],"blendedInto":[makeQuery(id+"F2.opChamfer","BLEND_FACE",FACE,{"disambiguationData":[OSD([subQ0])]})]});}
            var Q2;
            {var subQ0=sQuery(id+"F0.wireOp",EDGE,"E5");Q2=makeQuery(id+"F3.opChamfer","BLEND_EDGE",EDGE,{"blendedFrom":[makeQuery(id+"F1.opExtrude","CAP_EDGE",EDGE,{"disambiguationData":[OSD([subQ0])],"isStart":true}),makeQuery(id+"F2.opChamfer","BLEND_FACE",FACE,{"disambiguationData":[OSD([subQ0])]})],"blendedInto":[makeQuery(id+"F2.opChamfer","BLEND_FACE",FACE,{"disambiguationData":[OSD([subQ0])]})]});}
            var Q3;
            {var subQ0=sQuery(id+"F0.wireOp",EDGE,"E2");Q3=makeQuery(id+"F3.opChamfer","BLEND_EDGE",EDGE,{"blendedFrom":[makeQuery(id+"F1.opExtrude","CAP_EDGE",EDGE,{"disambiguationData":[OSD([subQ0])],"isStart":true}),makeQuery(id+"F2.opChamfer","BLEND_FACE",FACE,{"disambiguationData":[OSD([subQ0])]})],"blendedInto":[makeQuery(id+"F2.opChamfer","BLEND_FACE",FACE,{"disambiguationData":[OSD([subQ0])]})]});}
            var Q4;
            {var subQ0=sQuery(id+"F0.wireOp",EDGE,"E4.2.0");Q4=makeQuery(id+"F3.opChamfer","BLEND_EDGE",EDGE,{"blendedFrom":[makeQuery(id+"F1.opExtrude","CAP_EDGE",EDGE,{"disambiguationData":[OSD([subQ0])],"isStart":true}),makeQuery(id+"F2.opChamfer","BLEND_FACE",FACE,{"disambiguationData":[OSD([subQ0])]})],"blendedInto":[makeQuery(id+"F2.opChamfer","BLEND_FACE",FACE,{"disambiguationData":[OSD([subQ0])]})]});}
            var Q5;
            {var subQ0=sQuery(id+"F0.wireOp",EDGE,"E7.2.1");Q5=makeQuery(id+"F3.opChamfer","BLEND_EDGE",EDGE,{"blendedFrom":[makeQuery(id+"F1.opExtrude","CAP_EDGE",EDGE,{"disambiguationData":[OSD([subQ0])],"isStart":true}),makeQuery(id+"F2.opChamfer","BLEND_FACE",FACE,{"disambiguationData":[OSD([subQ0])]})],"blendedInto":[makeQuery(id+"F2.opChamfer","BLEND_FACE",FACE,{"disambiguationData":[OSD([subQ0])]})]});}
            var Q6;
            {var subQ0=sQuery(id+"F0.wireOp",EDGE,"E7.4.1");Q6=makeQuery(id+"F3.opChamfer","BLEND_EDGE",EDGE,{"blendedFrom":[makeQuery(id+"F1.opExtrude","CAP_EDGE",EDGE,{"disambiguationData":[OSD([subQ0])],"isStart":true}),makeQuery(id+"F2.opChamfer","BLEND_FACE",FACE,{"disambiguationData":[OSD([subQ0])]})],"blendedInto":[makeQuery(id+"F2.opChamfer","BLEND_FACE",FACE,{"disambiguationData":[OSD([subQ0])]})]});}
            var Q7;
            {var subQ0=sQuery(id+"F0.wireOp",EDGE,"E4.4.0");Q7=makeQuery(id+"F3.opChamfer","BLEND_EDGE",EDGE,{"blendedFrom":[makeQuery(id+"F1.opExtrude","CAP_EDGE",EDGE,{"disambiguationData":[OSD([subQ0])],"isStart":true}),makeQuery(id+"F2.opChamfer","BLEND_FACE",FACE,{"disambiguationData":[OSD([subQ0])]})],"blendedInto":[makeQuery(id+"F2.opChamfer","BLEND_FACE",FACE,{"disambiguationData":[OSD([subQ0])]})]});}
            var Q8;
            {var subQ0=sQuery(id+"F0.wireOp",EDGE,"E4.3.0");Q8=makeQuery(id+"F3.opChamfer","BLEND_EDGE",EDGE,{"blendedFrom":[makeQuery(id+"F1.opExtrude","CAP_EDGE",EDGE,{"disambiguationData":[OSD([subQ0])],"isStart":true}),makeQuery(id+"F2.opChamfer","BLEND_FACE",FACE,{"disambiguationData":[OSD([subQ0])]})],"blendedInto":[makeQuery(id+"F2.opChamfer","BLEND_FACE",FACE,{"disambiguationData":[OSD([subQ0])]})]});}
            var Q9;
            {var subQ0=sQuery(id+"F0.wireOp",EDGE,"E7.3.1");Q9=makeQuery(id+"F3.opChamfer","BLEND_EDGE",EDGE,{"blendedFrom":[makeQuery(id+"F1.opExtrude","CAP_EDGE",EDGE,{"disambiguationData":[OSD([subQ0])],"isStart":true}),makeQuery(id+"F2.opChamfer","BLEND_FACE",FACE,{"disambiguationData":[OSD([subQ0])]})],"blendedInto":[makeQuery(id+"F2.opChamfer","BLEND_FACE",FACE,{"disambiguationData":[OSD([subQ0])]})]});}
            fillet(context, id + "F10", {"entities" : qUnion([Q0, Q1, Q2, Q3, Q4, Q5, Q6, Q7, Q8, Q9]), "radius" : 1 * mm, "tangentPropagation" : true, "allowEdgeOverflow" : false});
        }
        {
            var Q0;
            {var subQ0=sQuery(id+"F0.wireOp",EDGE,"E6");var subQ1=makeQuery(id+"F2.opChamfer","BLEND_FACE",FACE,{"disambiguationData":[OSD([subQ0])]});Q0=makeQuery(id+"F8.opChamfer","BLEND_EDGE",EDGE,{"blendedFrom":[makeQuery(id+"F3.opChamfer","BLEND_EDGE",EDGE,{"blendedFrom":[makeQuery(id+"F1.opExtrude","CAP_EDGE",EDGE,{"disambiguationData":[OSD([subQ0])],"isStart":true}),subQ1],"blendedInto":[subQ1]}),subQ1],"blendedInto":[subQ1]});}
            var Q1;
            {var subQ0=sQuery(id+"F0.wireOp",EDGE,"E7.4.0");var subQ1=makeQuery(id+"F2.opChamfer","BLEND_FACE",FACE,{"disambiguationData":[OSD([subQ0])]});Q1=makeQuery(id+"F8.opChamfer","BLEND_EDGE",EDGE,{"blendedFrom":[makeQuery(id+"F3.opChamfer","BLEND_EDGE",EDGE,{"blendedFrom":[makeQuery(id+"F1.opExtrude","CAP_EDGE",EDGE,{"disambiguationData":[OSD([subQ0])],"isStart":true}),subQ1],"blendedInto":[subQ1]}),subQ1],"blendedInto":[subQ1]});}
            var Q2;
            {var subQ0=sQuery(id+"F0.wireOp",EDGE,"E7.3.0");var subQ1=makeQuery(id+"F2.opChamfer","BLEND_FACE",FACE,{"disambiguationData":[OSD([subQ0])]});Q2=makeQuery(id+"F8.opChamfer","BLEND_EDGE",EDGE,{"blendedFrom":[makeQuery(id+"F3.opChamfer","BLEND_EDGE",EDGE,{"blendedFrom":[makeQuery(id+"F1.opExtrude","CAP_EDGE",EDGE,{"disambiguationData":[OSD([subQ0])],"isStart":true}),subQ1],"blendedInto":[subQ1]}),subQ1],"blendedInto":[subQ1]});}
            var Q3;
            {var subQ0=sQuery(id+"F0.wireOp",EDGE,"E7.1.0");var subQ1=makeQuery(id+"F2.opChamfer","BLEND_FACE",FACE,{"disambiguationData":[OSD([subQ0])]});Q3=makeQuery(id+"F8.opChamfer","BLEND_EDGE",EDGE,{"blendedFrom":[makeQuery(id+"F3.opChamfer","BLEND_EDGE",EDGE,{"blendedFrom":[makeQuery(id+"F1.opExtrude","CAP_EDGE",EDGE,{"disambiguationData":[OSD([subQ0])],"isStart":true}),subQ1],"blendedInto":[subQ1]}),subQ1],"blendedInto":[subQ1]});}
            var Q4;
            {var subQ0=sQuery(id+"F0.wireOp",EDGE,"E7.2.0");var subQ1=makeQuery(id+"F2.opChamfer","BLEND_FACE",FACE,{"disambiguationData":[OSD([subQ0])]});Q4=makeQuery(id+"F8.opChamfer","BLEND_EDGE",EDGE,{"blendedFrom":[makeQuery(id+"F3.opChamfer","BLEND_EDGE",EDGE,{"blendedFrom":[makeQuery(id+"F1.opExtrude","CAP_EDGE",EDGE,{"disambiguationData":[OSD([subQ0])],"isStart":true}),subQ1],"blendedInto":[subQ1]}),subQ1],"blendedInto":[subQ1]});}
            var Q5;
            {var subQ0=sQuery(id+"F0.wireOp",EDGE,"E3.4.0");Q5=makeQuery(id+"F3.opChamfer","BLEND_EDGE",EDGE,{"blendedFrom":[makeQuery(id+"F1.opExtrude","CAP_EDGE",EDGE,{"disambiguationData":[OSD([subQ0])],"isStart":true}),makeQuery(id+"F2.opChamfer","BLEND_FACE",FACE,{"disambiguationData":[OSD([subQ0])]})],"blendedInto":[makeQuery(id+"F2.opChamfer","BLEND_FACE",FACE,{"disambiguationData":[OSD([subQ0])]})]});}
            var Q6;
            {var subQ0=sQuery(id+"F0.wireOp",EDGE,"E1");Q6=makeQuery(id+"F3.opChamfer","BLEND_EDGE",EDGE,{"blendedFrom":[makeQuery(id+"F1.opExtrude","CAP_EDGE",EDGE,{"disambiguationData":[OSD([subQ0])],"isStart":true}),makeQuery(id+"F2.opChamfer","BLEND_FACE",FACE,{"disambiguationData":[OSD([subQ0])]})],"blendedInto":[makeQuery(id+"F2.opChamfer","BLEND_FACE",FACE,{"disambiguationData":[OSD([subQ0])]})]});}
            var Q7;
            {var subQ0=sQuery(id+"F0.wireOp",EDGE,"E3.1.0");Q7=makeQuery(id+"F3.opChamfer","BLEND_EDGE",EDGE,{"blendedFrom":[makeQuery(id+"F1.opExtrude","CAP_EDGE",EDGE,{"disambiguationData":[OSD([subQ0])],"isStart":true}),makeQuery(id+"F2.opChamfer","BLEND_FACE",FACE,{"disambiguationData":[OSD([subQ0])]})],"blendedInto":[makeQuery(id+"F2.opChamfer","BLEND_FACE",FACE,{"disambiguationData":[OSD([subQ0])]})]});}
            var Q8;
            {var subQ0=sQuery(id+"F0.wireOp",EDGE,"E3.2.0");Q8=makeQuery(id+"F3.opChamfer","BLEND_EDGE",EDGE,{"blendedFrom":[makeQuery(id+"F1.opExtrude","CAP_EDGE",EDGE,{"disambiguationData":[OSD([subQ0])],"isStart":true}),makeQuery(id+"F2.opChamfer","BLEND_FACE",FACE,{"disambiguationData":[OSD([subQ0])]})],"blendedInto":[makeQuery(id+"F2.opChamfer","BLEND_FACE",FACE,{"disambiguationData":[OSD([subQ0])]})]});}
            var Q9;
            {var subQ0=sQuery(id+"F0.wireOp",EDGE,"E3.3.0");Q9=makeQuery(id+"F3.opChamfer","BLEND_EDGE",EDGE,{"blendedFrom":[makeQuery(id+"F1.opExtrude","CAP_EDGE",EDGE,{"disambiguationData":[OSD([subQ0])],"isStart":true}),makeQuery(id+"F2.opChamfer","BLEND_FACE",FACE,{"disambiguationData":[OSD([subQ0])]})],"blendedInto":[makeQuery(id+"F2.opChamfer","BLEND_FACE",FACE,{"disambiguationData":[OSD([subQ0])]})]});}
            fillet(context, id + "F11", {"entities" : qUnion([Q0, Q1, Q2, Q3, Q4, Q5, Q6, Q7, Q8, Q9]), "radius" : 1 * mm, "tangentPropagation" : true, "allowEdgeOverflow" : false});
        }
    });
